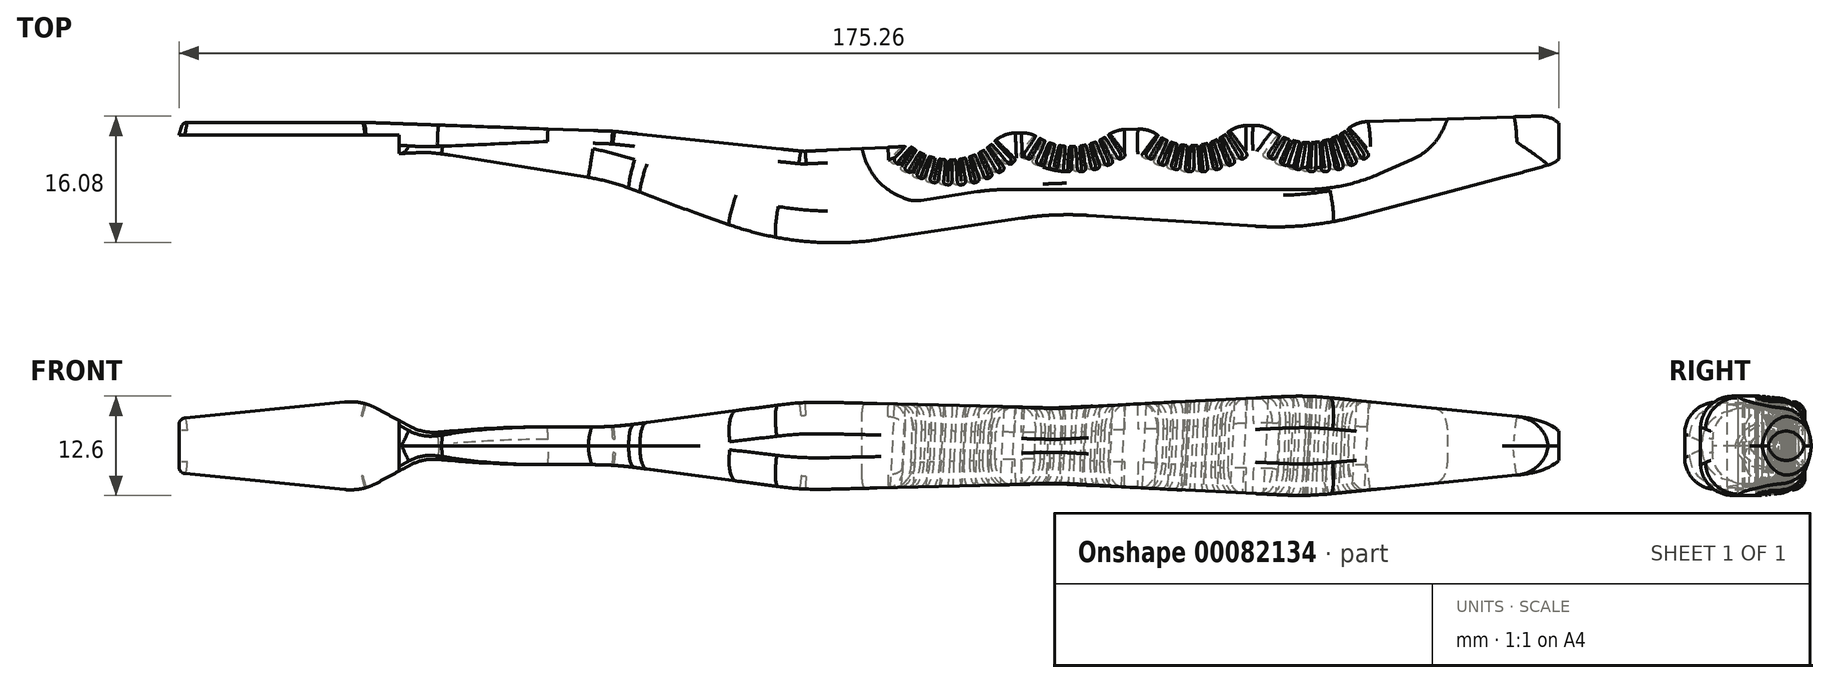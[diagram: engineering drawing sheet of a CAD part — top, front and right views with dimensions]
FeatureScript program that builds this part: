
annotation { "Feature Type Name" : "Feature", "Feature Type Description" : "" }
export const myFeature = defineFeature(function(context is Context, id is Id, definition is map)
    precondition{}
    {
        {
            var Q0;
            Q0=qCreatedBy(makeId("Front.planeOp"),FACE);
            var sketch = newSketch(context, id + "F0", { "sketchPlane" : qUnion([Q0])});
            skLineSegment(sketch, "E0", {"start": v(0, 0) * mm, "end": v(-220, 0) * mm, "construction": true});
            skLineSegment(sketch, "E1", {"start": v(-220, 0) * mm, "end": v(-220, 5) * mm});
            skLineSegment(sketch, "E2", {"start": v(-190, 0) * mm, "end": v(-190, 8) * mm, "construction": true});
            skLineSegment(sketch, "E3", {"start": v(-180, 0) * mm, "end": v(-180, 3) * mm, "construction": true});
            skLineSegment(sketch, "E4", {"start": v(-150, 0) * mm, "end": v(-150, 3) * mm, "construction": true});
            skLineSegment(sketch, "E5", {"start": v(-120, 0) * mm, "end": v(-120, 7) * mm, "construction": true});
            skLineSegment(sketch, "E6", {"start": v(-80, 0) * mm, "end": v(-80, 6) * mm, "construction": true});
            skLineSegment(sketch, "E7", {"start": v(-40, 0) * mm, "end": v(-40, 8) * mm, "construction": true});
            skLineSegment(sketch, "E8", {"start": v(0, 0) * mm, "end": v(0, 4) * mm});
            skLineSegment(sketch, "E9", {"start": v(0, 4) * mm, "end": v(-40, 8) * mm});
            skLineSegment(sketch, "E10", {"start": v(-40, 8) * mm, "end": v(-80, 6) * mm});
            skLineSegment(sketch, "E11", {"start": v(-80, 6) * mm, "end": v(-120, 7) * mm});
            skLineSegment(sketch, "E12", {"start": v(-120, 7) * mm, "end": v(-150, 3) * mm});
            skLineSegment(sketch, "E13", {"start": v(-150, 3) * mm, "end": v(-180, 3) * mm});
            skLineSegment(sketch, "E14", {"start": v(-180, 3) * mm, "end": v(-190, 8) * mm});
            skLineSegment(sketch, "E15", {"start": v(-190, 8) * mm, "end": v(-220, 5) * mm});
            skLineSegment(sketch, "E16.MirrorCS", {"start": v(0, 0) * mm, "end": v(0, -4) * mm});
            skLineSegment(sketch, "E17.MirrorCS", {"start": v(-220, 0) * mm, "end": v(-220, -5) * mm});
            skLineSegment(sketch, "E18.MirrorCS", {"start": v(-190, -8) * mm, "end": v(-220, -5) * mm});
            skLineSegment(sketch, "E19.MirrorCS", {"start": v(-180, -3) * mm, "end": v(-190, -8) * mm});
            skLineSegment(sketch, "E20.MirrorCS", {"start": v(-150, -3) * mm, "end": v(-180, -3) * mm});
            skLineSegment(sketch, "E21.MirrorCS", {"start": v(-120, -7) * mm, "end": v(-150, -3) * mm});
            skLineSegment(sketch, "E22.MirrorCS", {"start": v(-80, -6) * mm, "end": v(-120, -7) * mm});
            skLineSegment(sketch, "E23.MirrorCS", {"start": v(0, -4) * mm, "end": v(-40, -8) * mm});
            skLineSegment(sketch, "E24.MirrorCS", {"start": v(-40, -8) * mm, "end": v(-80, -6) * mm});
            skSolve(sketch);
        }
        {
            var Q0;
            Q0=makeQuery(id+"F0.imprint","IMPRINT",FACE,{"disambiguationData":[TD([[makeQuery(id+"F0.imprint","IMPRINT",EDGE,{"derivedFrom":sQuery(id+"F0.wireOp",EDGE,"E1")}),-1.0]])]});
            extrude(context, id + "F1", {"entities" : qUnion([Q0]), "depth" : 25 * mm});
        }
        {
            var Q0;
            Q0=makeQuery(id+"F1.opExtrude","SWEPT_FACE",FACE,{"disambiguationData":[OSD([sQuery(id+"F0.wireOp",EDGE,"E20.MirrorCS")])]});
            var sketch = newSketch(context, id + "F2", { "sketchPlane" : qUnion([Q0])});
            skLineSegment(sketch, "E25.0", {"start": v(-190, 0) * mm, "end": v(-220, 0) * mm, "construction": true});
            skLineSegment(sketch, "E25.4", {"start": v(-80, 0) * mm, "end": v(-120, 0) * mm, "construction": true});
            skLineSegment(sketch, "E25.5", {"start": v(-40, 0) * mm, "end": v(-80, 0) * mm, "construction": true});
            skLineSegment(sketch, "E25.6", {"start": v(0, 0) * mm, "end": v(-40, 0) * mm, "construction": true});
            skLineSegment(sketch, "E26", {"start": v(-220, 7.68) * mm, "end": v(-218.46, 2.68) * mm});
            skLineSegment(sketch, "E27", {"start": v(-218.46, 2.68) * mm, "end": v(-190, 2.68) * mm});
            skLineSegment(sketch, "E28", {"start": v(-119.9, 7.3) * mm, "end": v(-102.9, 6.47) * mm});
            skLineSegment(sketch, "E29", {"start": v(-119.9, 23.1) * mm, "end": v(-80, 17.11) * mm});
            skLineSegment(sketch, "E30", {"start": v(-80, 17.11) * mm, "end": v(-40, 19.71) * mm});
            skLineSegment(sketch, "E31", {"start": v(-40, 19.71) * mm, "end": v(0, 9.1) * mm});
            skLineSegment(sketch, "E32", {"start": v(0, 9.1) * mm, "end": v(0, 1.58) * mm});
            skArc(sketch, "E33", {"start": v(-88.51, 4.45) * mm, "mid": v(-95.27, 8.57) * mm, "end": v(-102.9, 6.47) * mm});
            skArc(sketch, "E34", {"start": v(-32.26, 2.63) * mm, "mid": v(-39.34, 5.9) * mm, "end": v(-46.62, 3.1) * mm});
            skLineSegment(sketch, "E35", {"start": v(-88.51, 4.45) * mm, "end": v(-83.73, 4.3) * mm});
            skLineSegment(sketch, "E36", {"start": v(-70.5, 3.87) * mm, "end": v(-64.85, 3.69) * mm});
            skArc(sketch, "E37.trimOffspring", {"start": v(-70.5, 3.87) * mm, "mid": v(-77.03, 6.54) * mm, "end": v(-83.73, 4.3) * mm});
            skLineSegment(sketch, "E38.trimOffspring", {"start": v(-51.47, 3.25) * mm, "end": v(-46.62, 3.1) * mm});
            skLineSegment(sketch, "E39.trimOffspring", {"start": v(-32.26, 2.63) * mm, "end": v(0, 1.58) * mm});
            skArc(sketch, "E40.trimOffspring", {"start": v(-51.47, 3.25) * mm, "mid": v(-58.07, 6.39) * mm, "end": v(-64.85, 3.69) * mm});
            skPoint(sketch, "E41.center.orphan", {"position": v(-77.66, -2.25) * mm});
            skPoint(sketch, "E42.center.orphan", {"position": v(-58.66, -3.17) * mm});
            skLineSegment(sketch, "E43.top", {"start": v(-229.41, 31.75) * mm, "end": v(15.55, 31.75) * mm});
            skLineSegment(sketch, "E43.left", {"start": v(-229.41, -17.07) * mm, "end": v(-229.41, 31.75) * mm});
            skLineSegment(sketch, "E43.right", {"start": v(15.55, -17.07) * mm, "end": v(15.55, 31.75) * mm});
            skLineSegment(sketch, "E44", {"start": v(-220, 7.68) * mm, "end": v(-180, 7.68) * mm});
            skLineSegment(sketch, "E45", {"start": v(-180, 7.68) * mm, "end": v(-150, 12.5) * mm});
            skLineSegment(sketch, "E46", {"start": v(-150, 12.5) * mm, "end": v(-119.9, 23.1) * mm});
            skLineSegment(sketch, "E47", {"start": v(-119.9, 7.3) * mm, "end": v(-150, 4.12) * mm});
            skLineSegment(sketch, "E48", {"start": v(-150, 4.12) * mm, "end": v(-190, 2.68) * mm});
            skLineSegment(sketch, "E49", {"start": v(15.55, -17.07) * mm, "end": v(-229.41, -17.07) * mm});
            skSolve(sketch);
        }
        {
            var Q0;
            Q0=makeQuery(id+"F2.imprint","IMPRINT",FACE,{"disambiguationData":[TD([[makeQuery(id+"F2.imprint","IMPRINT",EDGE,{"derivedFrom":sQuery(id+"F2.wireOp",EDGE,"E26")}),-1.0]])]});
            var Q1;
            {var subQ0=sQuery(id+"F2.wireOp",EDGE,"E45");Q1=makeQuery(id+"F2.imprint","IMPRINT",FACE,{"disambiguationData":[TD([[makeQuery(id+"F2.imprint","IMPRINT",EDGE,{"derivedFrom":subQ0}),1.0]])]});}
            var Q2;
            {var subQ1=sQuery(id+"F0.wireOp",EDGE,"E20.MirrorCS");var subQ6=makeQuery(id+"F1.opExtrude","CAP_EDGE",EDGE,{"disambiguationData":[OSD([subQ1])],"isStart":true});Q2=makeQuery(id+"F2.imprint","IMPRINT",FACE,{"disambiguationData":[TD([[makeQuery(id+"F2.imprint","IMPRINT",EDGE,{"derivedFrom":subQ6}),-1.0]])]});}
            extrude(context, id + "F3", {"entities" : qUnion([Q0, Q1, Q2]), "operationType" : NewBodyOperationType.REMOVE, "endBound" : BoundingType.SYMMETRIC, "oppositeDirection" : true, "depth" : 40 * mm});
        }
        {
            var Q0;
            Q0=makeQuery(id+"F3.boolean.opBoolean","COPY",EDGE,{"derivedFrom":makeQuery(id+"F3.opExtrude","SWEPT_EDGE",EDGE,{"disambiguationData":[OSD([sQuery(id+"F2.wireOp",EDGE,"E29"),sQuery(id+"F2.wireOp",EDGE,"E46")])]})});
            var Q1;
            Q1=makeQuery(id+"F3.boolean.opBoolean","COPY",EDGE,{"derivedFrom":makeQuery(id+"F3.opExtrude","SWEPT_EDGE",EDGE,{"disambiguationData":[OSD([sQuery(id+"F2.wireOp",EDGE,"E29"),sQuery(id+"F2.wireOp",EDGE,"E30")])]})});
            var Q2;
            Q2=makeQuery(id+"F3.boolean.opBoolean","COPY",EDGE,{"derivedFrom":makeQuery(id+"F3.opExtrude","SWEPT_EDGE",EDGE,{"disambiguationData":[OSD([sQuery(id+"F2.wireOp",EDGE,"E30"),sQuery(id+"F2.wireOp",EDGE,"E31")])]})});
            var Q3;
            Q3=makeQuery(id+"F3.boolean.opBoolean","COPY",EDGE,{"derivedFrom":makeQuery(id+"F3.opExtrude","SWEPT_EDGE",EDGE,{"disambiguationData":[OSD([sQuery(id+"F0.wireOp",EDGE,"E20.MirrorCS"),sQuery(id+"F0.wireOp",EDGE,"E21.MirrorCS"),sQuery(id+"F2.wireOp",EDGE,"E45"),sQuery(id+"F2.wireOp",EDGE,"E46")])]})});
            var Q4;
            Q4=makeQuery(id+"F3.boolean.opBoolean","COPY",EDGE,{"derivedFrom":makeQuery(id+"F3.opExtrude","SWEPT_EDGE",EDGE,{"disambiguationData":[OSD([sQuery(id+"F0.wireOp",EDGE,"E19.MirrorCS"),sQuery(id+"F0.wireOp",EDGE,"E20.MirrorCS"),sQuery(id+"F2.wireOp",EDGE,"E44"),sQuery(id+"F2.wireOp",EDGE,"E45")])]})});
            fillet(context, id + "F4", {"entities" : qUnion([Q0, Q1, Q2, Q3, Q4]), "radius" : 50 * mm, "tangentPropagation" : true, "allowEdgeOverflow" : false});
        }
        {
            var Q0;
            Q0=makeQuery(id+"F3.boolean.opBoolean","COPY",EDGE,{"derivedFrom":makeQuery(id+"F3.opExtrude","SWEPT_EDGE",EDGE,{"disambiguationData":[OSD([sQuery(id+"F2.wireOp",EDGE,"E27"),sQuery(id+"F2.wireOp",EDGE,"E48")])]})});
            var Q1;
            Q1=makeQuery(id+"F3.boolean.opBoolean","COPY",EDGE,{"derivedFrom":makeQuery(id+"F3.opExtrude","SWEPT_EDGE",EDGE,{"disambiguationData":[OSD([sQuery(id+"F0.wireOp",EDGE,"E20.MirrorCS"),sQuery(id+"F0.wireOp",EDGE,"E21.MirrorCS"),sQuery(id+"F2.wireOp",EDGE,"E47"),sQuery(id+"F2.wireOp",EDGE,"E48")])]})});
            var Q2;
            Q2=makeQuery(id+"F3.boolean.opBoolean","COPY",EDGE,{"derivedFrom":makeQuery(id+"F3.opExtrude","SWEPT_EDGE",EDGE,{"disambiguationData":[OSD([sQuery(id+"F2.wireOp",EDGE,"E28"),sQuery(id+"F2.wireOp",EDGE,"E47")])]})});
            fillet(context, id + "F5", {"entities" : qUnion([Q0, Q1, Q2]), "radius" : 5 * mm, "tangentPropagation" : true, "allowEdgeOverflow" : false});
        }
        {
            var Q0;
            Q0=makeQuery(id+"F1.opExtrude","SWEPT_EDGE",EDGE,{"disambiguationData":[OSD([sQuery(id+"F0.wireOp",EDGE,"E20.MirrorCS"),sQuery(id+"F0.wireOp",EDGE,"E21.MirrorCS")])]});
            var Q1;
            Q1=makeQuery(id+"F1.opExtrude","SWEPT_EDGE",EDGE,{"disambiguationData":[OSD([sQuery(id+"F0.wireOp",EDGE,"E21.MirrorCS"),sQuery(id+"F0.wireOp",EDGE,"E22.MirrorCS")])]});
            var Q2;
            Q2=makeQuery(id+"F1.opExtrude","SWEPT_EDGE",EDGE,{"disambiguationData":[OSD([sQuery(id+"F0.wireOp",EDGE,"E22.MirrorCS"),sQuery(id+"F0.wireOp",EDGE,"E24.MirrorCS")])]});
            var Q3;
            Q3=makeQuery(id+"F1.opExtrude","SWEPT_EDGE",EDGE,{"disambiguationData":[OSD([sQuery(id+"F0.wireOp",EDGE,"E23.MirrorCS"),sQuery(id+"F0.wireOp",EDGE,"E24.MirrorCS")])]});
            var Q4;
            Q4=makeQuery(id+"F1.opExtrude","SWEPT_EDGE",EDGE,{"disambiguationData":[OSD([sQuery(id+"F0.wireOp",EDGE,"E12"),sQuery(id+"F0.wireOp",EDGE,"E13")])]});
            var Q5;
            Q5=makeQuery(id+"F1.opExtrude","SWEPT_EDGE",EDGE,{"disambiguationData":[OSD([sQuery(id+"F0.wireOp",EDGE,"E11"),sQuery(id+"F0.wireOp",EDGE,"E12")])]});
            var Q6;
            Q6=makeQuery(id+"F1.opExtrude","SWEPT_EDGE",EDGE,{"disambiguationData":[OSD([sQuery(id+"F0.wireOp",EDGE,"E10"),sQuery(id+"F0.wireOp",EDGE,"E11")])]});
            var Q7;
            Q7=makeQuery(id+"F1.opExtrude","SWEPT_EDGE",EDGE,{"disambiguationData":[OSD([sQuery(id+"F0.wireOp",EDGE,"E9"),sQuery(id+"F0.wireOp",EDGE,"E10")])]});
            fillet(context, id + "F6", {"entities" : qUnion([Q0, Q1, Q2, Q3, Q4, Q5, Q6, Q7]), "radius" : 50 * mm, "tangentPropagation" : true, "allowEdgeOverflow" : false});
        }
        {
            var Q0;
            Q0=makeQuery(id+"F1.opExtrude","SWEPT_EDGE",EDGE,{"disambiguationData":[OSD([sQuery(id+"F0.wireOp",EDGE,"E18.MirrorCS"),sQuery(id+"F0.wireOp",EDGE,"E19.MirrorCS")])]});
            var Q1;
            Q1=makeQuery(id+"F1.opExtrude","SWEPT_EDGE",EDGE,{"disambiguationData":[OSD([sQuery(id+"F0.wireOp",EDGE,"E19.MirrorCS"),sQuery(id+"F0.wireOp",EDGE,"E20.MirrorCS")])]});
            var Q2;
            Q2=makeQuery(id+"F1.opExtrude","SWEPT_EDGE",EDGE,{"disambiguationData":[OSD([sQuery(id+"F0.wireOp",EDGE,"E13"),sQuery(id+"F0.wireOp",EDGE,"E14")])]});
            var Q3;
            Q3=makeQuery(id+"F1.opExtrude","SWEPT_EDGE",EDGE,{"disambiguationData":[OSD([sQuery(id+"F0.wireOp",EDGE,"E14"),sQuery(id+"F0.wireOp",EDGE,"E15")])]});
            fillet(context, id + "F7", {"entities" : qUnion([Q0, Q1, Q2, Q3]), "radius" : 10 * mm, "tangentPropagation" : true, "allowEdgeOverflow" : false});
        }
        {
            var Q0;
            Q0=makeQuery(id+"F6.opFillet","BLEND_EDGE",EDGE,{"blendedFrom":[makeQuery(id+"F1.opExtrude","SWEPT_EDGE",EDGE,{"disambiguationData":[OSD([sQuery(id+"F0.wireOp",EDGE,"E21.MirrorCS"),sQuery(id+"F0.wireOp",EDGE,"E22.MirrorCS")])]}),makeQuery(id+"F4.opFillet","BLEND_FACE",FACE,{"disambiguationData":[OSD([sQuery(id+"F2.wireOp",EDGE,"E29"),sQuery(id+"F2.wireOp",EDGE,"E46")])]})],"blendedInto":[makeQuery(id+"F4.opFillet","BLEND_FACE",FACE,{"disambiguationData":[OSD([sQuery(id+"F2.wireOp",EDGE,"E29"),sQuery(id+"F2.wireOp",EDGE,"E46")])]})]});
            var Q1;
            Q1=makeQuery(id+"F3.boolean.opBoolean","INTERSECT",EDGE,{"derivedFrom":[makeQuery(id+"F1.opExtrude","SWEPT_FACE",FACE,{"disambiguationData":[OSD([sQuery(id+"F0.wireOp",EDGE,"E11")])]}),makeQuery(id+"F3.opExtrude","SWEPT_FACE",FACE,{"disambiguationData":[OSD([sQuery(id+"F2.wireOp",EDGE,"E29")])]})]});
            fillet(context, id + "F8", {"entities" : qUnion([Q0, Q1]), "radius" : 5 * mm, "tangentPropagation" : true, "allowEdgeOverflow" : false});
        }
        {
            var Q0;
            Q0=makeQuery(id+"F3.boolean.opBoolean","INTERSECT",EDGE,{"derivedFrom":[makeQuery(id+"F1.opExtrude","SWEPT_FACE",FACE,{"disambiguationData":[OSD([sQuery(id+"F0.wireOp",EDGE,"E22.MirrorCS")])]}),makeQuery(id+"F3.opExtrude","SWEPT_FACE",FACE,{"disambiguationData":[OSD([sQuery(id+"F2.wireOp",EDGE,"E33")])]})]});
            var Q1;
            Q1=makeQuery(id+"F6.opFillet","BLEND_EDGE",EDGE,{"blendedFrom":[makeQuery(id+"F1.opExtrude","SWEPT_EDGE",EDGE,{"disambiguationData":[OSD([sQuery(id+"F0.wireOp",EDGE,"E22.MirrorCS"),sQuery(id+"F0.wireOp",EDGE,"E24.MirrorCS")])]}),makeQuery(id+"F3.boolean.opBoolean","COPY",FACE,{"derivedFrom":makeQuery(id+"F3.opExtrude","SWEPT_FACE",FACE,{"disambiguationData":[OSD([sQuery(id+"F2.wireOp",EDGE,"E37.trimOffspring")])]})})],"blendedInto":[makeQuery(id+"F3.boolean.opBoolean","COPY",FACE,{"derivedFrom":makeQuery(id+"F3.opExtrude","SWEPT_FACE",FACE,{"disambiguationData":[OSD([sQuery(id+"F2.wireOp",EDGE,"E37.trimOffspring")])]})})]});
            var Q2;
            Q2=makeQuery(id+"F3.boolean.opBoolean","INTERSECT",EDGE,{"derivedFrom":[makeQuery(id+"F1.opExtrude","SWEPT_FACE",FACE,{"disambiguationData":[OSD([sQuery(id+"F0.wireOp",EDGE,"E24.MirrorCS")])]}),makeQuery(id+"F3.opExtrude","SWEPT_FACE",FACE,{"disambiguationData":[OSD([sQuery(id+"F2.wireOp",EDGE,"E40.trimOffspring")])]})]});
            var Q3;
            Q3=makeQuery(id+"F6.opFillet","BLEND_EDGE",EDGE,{"blendedFrom":[makeQuery(id+"F1.opExtrude","SWEPT_EDGE",EDGE,{"disambiguationData":[OSD([sQuery(id+"F0.wireOp",EDGE,"E23.MirrorCS"),sQuery(id+"F0.wireOp",EDGE,"E24.MirrorCS")])]}),makeQuery(id+"F3.boolean.opBoolean","COPY",FACE,{"derivedFrom":makeQuery(id+"F3.opExtrude","SWEPT_FACE",FACE,{"disambiguationData":[OSD([sQuery(id+"F2.wireOp",EDGE,"E34")])]})})],"blendedInto":[makeQuery(id+"F3.boolean.opBoolean","COPY",FACE,{"derivedFrom":makeQuery(id+"F3.opExtrude","SWEPT_FACE",FACE,{"disambiguationData":[OSD([sQuery(id+"F2.wireOp",EDGE,"E34")])]})})]});
            var Q4;
            Q4=makeQuery(id+"F3.boolean.opBoolean","INTERSECT",EDGE,{"derivedFrom":[makeQuery(id+"F1.opExtrude","SWEPT_FACE",FACE,{"disambiguationData":[OSD([sQuery(id+"F0.wireOp",EDGE,"E22.MirrorCS")])]}),makeQuery(id+"F3.opExtrude","SWEPT_FACE",FACE,{"disambiguationData":[OSD([sQuery(id+"F2.wireOp",EDGE,"E35")])]})]});
            var Q5;
            Q5=makeQuery(id+"F3.boolean.opBoolean","INTERSECT",EDGE,{"derivedFrom":[makeQuery(id+"F1.opExtrude","SWEPT_FACE",FACE,{"disambiguationData":[OSD([sQuery(id+"F0.wireOp",EDGE,"E24.MirrorCS")])]}),makeQuery(id+"F3.opExtrude","SWEPT_FACE",FACE,{"disambiguationData":[OSD([sQuery(id+"F2.wireOp",EDGE,"E36")])]})]});
            var Q6;
            Q6=makeQuery(id+"F3.boolean.opBoolean","INTERSECT",EDGE,{"derivedFrom":[makeQuery(id+"F1.opExtrude","SWEPT_FACE",FACE,{"disambiguationData":[OSD([sQuery(id+"F0.wireOp",EDGE,"E24.MirrorCS")])]}),makeQuery(id+"F3.opExtrude","SWEPT_FACE",FACE,{"disambiguationData":[OSD([sQuery(id+"F2.wireOp",EDGE,"E38.trimOffspring")])]})]});
            var Q7;
            Q7=makeQuery(id+"F3.boolean.opBoolean","INTERSECT",EDGE,{"derivedFrom":[makeQuery(id+"F1.opExtrude","SWEPT_FACE",FACE,{"disambiguationData":[OSD([sQuery(id+"F0.wireOp",EDGE,"E23.MirrorCS")])]}),makeQuery(id+"F3.opExtrude","SWEPT_FACE",FACE,{"disambiguationData":[OSD([sQuery(id+"F2.wireOp",EDGE,"E39.trimOffspring")])]})]});
            var Q8;
            Q8=makeQuery(id+"F3.boolean.opBoolean","INTERSECT",EDGE,{"derivedFrom":[makeQuery(id+"F1.opExtrude","SWEPT_FACE",FACE,{"disambiguationData":[OSD([sQuery(id+"F0.wireOp",EDGE,"E11")])]}),makeQuery(id+"F3.opExtrude","SWEPT_FACE",FACE,{"disambiguationData":[OSD([sQuery(id+"F2.wireOp",EDGE,"E33")])]})]});
            var Q9;
            Q9=makeQuery(id+"F3.boolean.opBoolean","INTERSECT",EDGE,{"derivedFrom":[makeQuery(id+"F1.opExtrude","SWEPT_FACE",FACE,{"disambiguationData":[OSD([sQuery(id+"F0.wireOp",EDGE,"E11")])]}),makeQuery(id+"F3.opExtrude","SWEPT_FACE",FACE,{"disambiguationData":[OSD([sQuery(id+"F2.wireOp",EDGE,"E35")])]})]});
            var Q10;
            Q10=makeQuery(id+"F3.boolean.opBoolean","INTERSECT",EDGE,{"derivedFrom":[makeQuery(id+"F1.opExtrude","SWEPT_FACE",FACE,{"disambiguationData":[OSD([sQuery(id+"F0.wireOp",EDGE,"E10")])]}),makeQuery(id+"F3.opExtrude","SWEPT_FACE",FACE,{"disambiguationData":[OSD([sQuery(id+"F2.wireOp",EDGE,"E37.trimOffspring")])]})]});
            var Q11;
            Q11=makeQuery(id+"F3.boolean.opBoolean","INTERSECT",EDGE,{"derivedFrom":[makeQuery(id+"F1.opExtrude","SWEPT_FACE",FACE,{"disambiguationData":[OSD([sQuery(id+"F0.wireOp",EDGE,"E10")])]}),makeQuery(id+"F3.opExtrude","SWEPT_FACE",FACE,{"disambiguationData":[OSD([sQuery(id+"F2.wireOp",EDGE,"E36")])]})]});
            var Q12;
            Q12=makeQuery(id+"F3.boolean.opBoolean","INTERSECT",EDGE,{"derivedFrom":[makeQuery(id+"F1.opExtrude","SWEPT_FACE",FACE,{"disambiguationData":[OSD([sQuery(id+"F0.wireOp",EDGE,"E10")])]}),makeQuery(id+"F3.opExtrude","SWEPT_FACE",FACE,{"disambiguationData":[OSD([sQuery(id+"F2.wireOp",EDGE,"E40.trimOffspring")])]})]});
            var Q13;
            Q13=makeQuery(id+"F3.boolean.opBoolean","INTERSECT",EDGE,{"derivedFrom":[makeQuery(id+"F1.opExtrude","SWEPT_FACE",FACE,{"disambiguationData":[OSD([sQuery(id+"F0.wireOp",EDGE,"E10")])]}),makeQuery(id+"F3.opExtrude","SWEPT_FACE",FACE,{"disambiguationData":[OSD([sQuery(id+"F2.wireOp",EDGE,"E38.trimOffspring")])]})]});
            var Q14;
            Q14=makeQuery(id+"F6.opFillet","BLEND_EDGE",EDGE,{"blendedFrom":[makeQuery(id+"F1.opExtrude","SWEPT_EDGE",EDGE,{"disambiguationData":[OSD([sQuery(id+"F0.wireOp",EDGE,"E9"),sQuery(id+"F0.wireOp",EDGE,"E10")])]}),makeQuery(id+"F3.boolean.opBoolean","COPY",FACE,{"derivedFrom":makeQuery(id+"F3.opExtrude","SWEPT_FACE",FACE,{"disambiguationData":[OSD([sQuery(id+"F2.wireOp",EDGE,"E34")])]})})],"blendedInto":[makeQuery(id+"F3.boolean.opBoolean","COPY",FACE,{"derivedFrom":makeQuery(id+"F3.opExtrude","SWEPT_FACE",FACE,{"disambiguationData":[OSD([sQuery(id+"F2.wireOp",EDGE,"E34")])]})})]});
            var Q15;
            Q15=makeQuery(id+"F3.boolean.opBoolean","INTERSECT",EDGE,{"derivedFrom":[makeQuery(id+"F1.opExtrude","SWEPT_FACE",FACE,{"disambiguationData":[OSD([sQuery(id+"F0.wireOp",EDGE,"E9")])]}),makeQuery(id+"F3.opExtrude","SWEPT_FACE",FACE,{"disambiguationData":[OSD([sQuery(id+"F2.wireOp",EDGE,"E39.trimOffspring")])]})]});
            fillet(context, id + "F9", {"entities" : qUnion([Q0, Q1, Q2, Q3, Q4, Q5, Q6, Q7, Q8, Q9, Q10, Q11, Q12, Q13, Q14, Q15]), "radius" : 4 * mm, "tangentPropagation" : true, "allowEdgeOverflow" : false});
        }
        {
            var Q0;
            Q0=makeQuery(id+"F3.boolean.opBoolean","INTERSECT",EDGE,{"derivedFrom":[makeQuery(id+"F1.opExtrude","SWEPT_FACE",FACE,{"disambiguationData":[OSD([sQuery(id+"F0.wireOp",EDGE,"E22.MirrorCS")])]}),makeQuery(id+"F3.opExtrude","SWEPT_FACE",FACE,{"disambiguationData":[OSD([sQuery(id+"F2.wireOp",EDGE,"E28")])]})]});
            fillet(context, id + "F10", {"entities" : qUnion([Q0]), "radius" : 2 * mm, "tangentPropagation" : true, "allowEdgeOverflow" : false});
        }
        {
            var Q0;
            Q0=makeQuery(id+"F3.boolean.opBoolean","COPY",EDGE,{"derivedFrom":makeQuery(id+"F3.opExtrude","SWEPT_EDGE",EDGE,{"disambiguationData":[OSD([sQuery(id+"F2.wireOp",EDGE,"E33"),sQuery(id+"F2.wireOp",EDGE,"E35")])]})});
            var Q1;
            Q1=makeQuery(id+"F3.boolean.opBoolean","COPY",EDGE,{"derivedFrom":makeQuery(id+"F3.opExtrude","SWEPT_EDGE",EDGE,{"disambiguationData":[OSD([sQuery(id+"F2.wireOp",EDGE,"E35"),sQuery(id+"F2.wireOp",EDGE,"E37.trimOffspring")])]})});
            var Q2;
            Q2=makeQuery(id+"F3.boolean.opBoolean","COPY",EDGE,{"derivedFrom":makeQuery(id+"F3.opExtrude","SWEPT_EDGE",EDGE,{"disambiguationData":[OSD([sQuery(id+"F2.wireOp",EDGE,"E36"),sQuery(id+"F2.wireOp",EDGE,"E37.trimOffspring")])]})});
            var Q3;
            Q3=makeQuery(id+"F3.boolean.opBoolean","COPY",EDGE,{"derivedFrom":makeQuery(id+"F3.opExtrude","SWEPT_EDGE",EDGE,{"disambiguationData":[OSD([sQuery(id+"F2.wireOp",EDGE,"E36"),sQuery(id+"F2.wireOp",EDGE,"E40.trimOffspring")])]})});
            var Q4;
            Q4=makeQuery(id+"F3.boolean.opBoolean","COPY",EDGE,{"derivedFrom":makeQuery(id+"F3.opExtrude","SWEPT_EDGE",EDGE,{"disambiguationData":[OSD([sQuery(id+"F2.wireOp",EDGE,"E38.trimOffspring"),sQuery(id+"F2.wireOp",EDGE,"E40.trimOffspring")])]})});
            var Q5;
            Q5=makeQuery(id+"F3.boolean.opBoolean","COPY",EDGE,{"derivedFrom":makeQuery(id+"F3.opExtrude","SWEPT_EDGE",EDGE,{"disambiguationData":[OSD([sQuery(id+"F2.wireOp",EDGE,"E34"),sQuery(id+"F2.wireOp",EDGE,"E38.trimOffspring")])]})});
            var Q6;
            Q6=makeQuery(id+"F3.boolean.opBoolean","COPY",EDGE,{"derivedFrom":makeQuery(id+"F3.opExtrude","SWEPT_EDGE",EDGE,{"disambiguationData":[OSD([sQuery(id+"F2.wireOp",EDGE,"E34"),sQuery(id+"F2.wireOp",EDGE,"E39.trimOffspring")])]})});
            fillet(context, id + "F11", {"entities" : qUnion([Q0, Q1, Q2, Q3, Q4, Q5, Q6]), "radius" : 5 * mm, "tangentPropagation" : true, "allowEdgeOverflow" : false});
        }
        {
            var Q0;
            Q0=makeQuery(id+"F8.opFillet","BLEND_EDGE",EDGE,{"blendedFrom":[makeQuery(id+"F3.boolean.opBoolean","INTERSECT",EDGE,{"derivedFrom":[makeQuery(id+"F1.opExtrude","SWEPT_FACE",FACE,{"disambiguationData":[OSD([sQuery(id+"F0.wireOp",EDGE,"E18.MirrorCS")])]}),makeQuery(id+"F3.opExtrude","SWEPT_FACE",FACE,{"disambiguationData":[OSD([sQuery(id+"F2.wireOp",EDGE,"E44")])]})]}),makeQuery(id+"F3.boolean.opBoolean","COPY",FACE,{"derivedFrom":makeQuery(id+"F3.opExtrude","SWEPT_FACE",FACE,{"disambiguationData":[OSD([sQuery(id+"F2.wireOp",EDGE,"E26")])]})})],"blendedInto":[makeQuery(id+"F3.boolean.opBoolean","COPY",FACE,{"derivedFrom":makeQuery(id+"F3.opExtrude","SWEPT_FACE",FACE,{"disambiguationData":[OSD([sQuery(id+"F2.wireOp",EDGE,"E26")])]})})]});
            fillet(context, id + "F12", {"entities" : qUnion([Q0]), "radius" : 1 * mm, "tangentPropagation" : true, "allowEdgeOverflow" : false});
        }
        {
            var Q0;
            Q0=qCreatedBy(makeId("Top.planeOp"),FACE);
            var sketch = newSketch(context, id + "F13", { "sketchPlane" : qUnion([Q0])});
            skLineSegment(sketch, "E50", {"start": v(-111.36, -3.91) * mm, "end": v(-110.38, -7.71) * mm});
            skLineSegment(sketch, "E51", {"start": v(-104.93, -14.29) * mm, "end": v(-104.14, -14.66) * mm});
            skLineSegment(sketch, "E52", {"start": v(-101.27, -15.07) * mm, "end": v(-92.35, -13.7) * mm});
            skLineSegment(sketch, "E53", {"start": v(-87.82, -13.36) * mm, "end": v(-74.2, -13.36) * mm});
            skLineSegment(sketch, "E54", {"start": v(-74.2, -13.36) * mm, "end": v(-53.16, -13.36) * mm});
            skLineSegment(sketch, "E55", {"start": v(-53.16, -13.36) * mm, "end": v(-40.43, -13.36) * mm});
            skLineSegment(sketch, "E56", {"start": v(-28.35, -10.83) * mm, "end": v(-23.32, -8.61) * mm});
            skLineSegment(sketch, "E57", {"start": v(-18.04, -3.12) * mm, "end": v(-16.8, 0) * mm});
            skPoint(sketch, "E58.visualSharp", {"position": v(-109.21, -12.29) * mm});
            skArc(sketch, "E58.filletArc", {"start": v(-110.38, -7.71) * mm, "mid": v(-108.4, -11.61) * mm, "end": v(-104.93, -14.29) * mm});
            skPoint(sketch, "E59.visualSharp", {"position": v(-102.77, -15.3) * mm});
            skArc(sketch, "E59.filletArc", {"start": v(-104.14, -14.66) * mm, "mid": v(-102.74, -15.07) * mm, "end": v(-101.27, -15.07) * mm});
            skPoint(sketch, "E60.visualSharp", {"position": v(-19.55, -6.95) * mm});
            skArc(sketch, "E60.filletArc", {"start": v(-23.32, -8.61) * mm, "mid": v(-20.13, -6.39) * mm, "end": v(-18.04, -3.12) * mm});
            skPoint(sketch, "E61.visualSharp", {"position": v(-34.12, -13.36) * mm});
            skArc(sketch, "E61.filletArc", {"start": v(-40.43, -13.36) * mm, "mid": v(-34.26, -12.72) * mm, "end": v(-28.35, -10.83) * mm});
            skPoint(sketch, "E62.visualSharp", {"position": v(-90.1, -13.36) * mm});
            skArc(sketch, "E62.filletArc", {"start": v(-87.82, -13.36) * mm, "mid": v(-90.1, -13.45) * mm, "end": v(-92.35, -13.7) * mm});
            skLineSegment(sketch, "E63", {"start": v(-111.36, -3.91) * mm, "end": v(-16.8, 0) * mm});
            skSolve(sketch);
        }
        {
            var Q0;
            Q0=makeQuery(id+"F13.imprint","IMPRINT",FACE,{"disambiguationData":[TD([[makeQuery(id+"F13.imprint","IMPRINT",EDGE,{"derivedFrom":sQuery(id+"F13.wireOp",EDGE,"E50")}),1.0]])]});
            extrude(context, id + "F14", {"entities" : qUnion([Q0]), "endBound" : BoundingType.SYMMETRIC, "depth" : 40 * mm});
        }
        {
            var Q0;
            Q0=makeQuery(id+"F14.opExtrude","SWEPT_BODY",BODY,{"disambiguationData":[OSD([sQuery(id+"F13.wireOp",EDGE,"E50"),sQuery(id+"F13.wireOp",EDGE,"E51"),sQuery(id+"F13.wireOp",EDGE,"E52"),sQuery(id+"F13.wireOp",EDGE,"E53"),sQuery(id+"F13.wireOp",EDGE,"E54"),sQuery(id+"F13.wireOp",EDGE,"E55"),sQuery(id+"F13.wireOp",EDGE,"E56"),sQuery(id+"F13.wireOp",EDGE,"E57"),sQuery(id+"F13.wireOp",EDGE,"E58.filletArc"),sQuery(id+"F13.wireOp",EDGE,"E59.filletArc"),sQuery(id+"F13.wireOp",EDGE,"E60.filletArc"),sQuery(id+"F13.wireOp",EDGE,"E61.filletArc"),sQuery(id+"F13.wireOp",EDGE,"E62.filletArc"),sQuery(id+"F13.wireOp",EDGE,"E63")])]});
            var Q1;
            Q1=makeQuery(id+"F1.opExtrude","SWEPT_BODY",BODY,{"disambiguationData":[OSD([sQuery(id+"F0.wireOp",EDGE,"E1"),sQuery(id+"F0.wireOp",EDGE,"E8"),sQuery(id+"F0.wireOp",EDGE,"E9"),sQuery(id+"F0.wireOp",EDGE,"E10"),sQuery(id+"F0.wireOp",EDGE,"E11"),sQuery(id+"F0.wireOp",EDGE,"E12"),sQuery(id+"F0.wireOp",EDGE,"E13"),sQuery(id+"F0.wireOp",EDGE,"E14"),sQuery(id+"F0.wireOp",EDGE,"E15"),sQuery(id+"F0.wireOp",EDGE,"E16.MirrorCS"),sQuery(id+"F0.wireOp",EDGE,"E17.MirrorCS"),sQuery(id+"F0.wireOp",EDGE,"E18.MirrorCS"),sQuery(id+"F0.wireOp",EDGE,"E19.MirrorCS"),sQuery(id+"F0.wireOp",EDGE,"E20.MirrorCS"),sQuery(id+"F0.wireOp",EDGE,"E21.MirrorCS"),sQuery(id+"F0.wireOp",EDGE,"E22.MirrorCS"),sQuery(id+"F0.wireOp",EDGE,"E23.MirrorCS"),sQuery(id+"F0.wireOp",EDGE,"E24.MirrorCS")])]});
            booleanBodies(context, id + "F15", {"operationType" : BooleanOperationType.INTERSECTION, "tools" : qUnion([Q0, Q1]), "keepTools" : true});
        }
        {
            var Q0;
            Q0=makeQuery(id+"F15.opBoolean","INTERSECT",BODY,{"derivedFrom":[makeQuery(id+"F1.opExtrude","SWEPT_BODY",BODY,{"disambiguationData":[OSD([sQuery(id+"F0.wireOp",EDGE,"E1"),sQuery(id+"F0.wireOp",EDGE,"E8"),sQuery(id+"F0.wireOp",EDGE,"E9"),sQuery(id+"F0.wireOp",EDGE,"E10"),sQuery(id+"F0.wireOp",EDGE,"E11"),sQuery(id+"F0.wireOp",EDGE,"E12"),sQuery(id+"F0.wireOp",EDGE,"E13"),sQuery(id+"F0.wireOp",EDGE,"E14"),sQuery(id+"F0.wireOp",EDGE,"E15"),sQuery(id+"F0.wireOp",EDGE,"E16.MirrorCS"),sQuery(id+"F0.wireOp",EDGE,"E17.MirrorCS"),sQuery(id+"F0.wireOp",EDGE,"E18.MirrorCS"),sQuery(id+"F0.wireOp",EDGE,"E19.MirrorCS"),sQuery(id+"F0.wireOp",EDGE,"E20.MirrorCS"),sQuery(id+"F0.wireOp",EDGE,"E21.MirrorCS"),sQuery(id+"F0.wireOp",EDGE,"E22.MirrorCS"),sQuery(id+"F0.wireOp",EDGE,"E23.MirrorCS"),sQuery(id+"F0.wireOp",EDGE,"E24.MirrorCS")])]}),makeQuery(id+"F14.opExtrude","SWEPT_BODY",BODY,{"disambiguationData":[OSD([sQuery(id+"F13.wireOp",EDGE,"E50"),sQuery(id+"F13.wireOp",EDGE,"E51"),sQuery(id+"F13.wireOp",EDGE,"E52"),sQuery(id+"F13.wireOp",EDGE,"E53"),sQuery(id+"F13.wireOp",EDGE,"E54"),sQuery(id+"F13.wireOp",EDGE,"E55"),sQuery(id+"F13.wireOp",EDGE,"E56"),sQuery(id+"F13.wireOp",EDGE,"E57"),sQuery(id+"F13.wireOp",EDGE,"E58.filletArc"),sQuery(id+"F13.wireOp",EDGE,"E59.filletArc"),sQuery(id+"F13.wireOp",EDGE,"E60.filletArc"),sQuery(id+"F13.wireOp",EDGE,"E61.filletArc"),sQuery(id+"F13.wireOp",EDGE,"E62.filletArc"),sQuery(id+"F13.wireOp",EDGE,"E63")])]})]});
            var Q1;
            Q1=makeQuery(id+"F1.opExtrude","SWEPT_BODY",BODY,{"disambiguationData":[OSD([sQuery(id+"F0.wireOp",EDGE,"E1"),sQuery(id+"F0.wireOp",EDGE,"E8"),sQuery(id+"F0.wireOp",EDGE,"E9"),sQuery(id+"F0.wireOp",EDGE,"E10"),sQuery(id+"F0.wireOp",EDGE,"E11"),sQuery(id+"F0.wireOp",EDGE,"E12"),sQuery(id+"F0.wireOp",EDGE,"E13"),sQuery(id+"F0.wireOp",EDGE,"E14"),sQuery(id+"F0.wireOp",EDGE,"E15"),sQuery(id+"F0.wireOp",EDGE,"E16.MirrorCS"),sQuery(id+"F0.wireOp",EDGE,"E17.MirrorCS"),sQuery(id+"F0.wireOp",EDGE,"E18.MirrorCS"),sQuery(id+"F0.wireOp",EDGE,"E19.MirrorCS"),sQuery(id+"F0.wireOp",EDGE,"E20.MirrorCS"),sQuery(id+"F0.wireOp",EDGE,"E21.MirrorCS"),sQuery(id+"F0.wireOp",EDGE,"E22.MirrorCS"),sQuery(id+"F0.wireOp",EDGE,"E23.MirrorCS"),sQuery(id+"F0.wireOp",EDGE,"E24.MirrorCS")])]});
            booleanBodies(context, id + "F16", {"operationType" : BooleanOperationType.SUBTRACTION, "tools" : qUnion([Q0]), "targets" : qUnion([Q1]), "keepTools" : true});
        }
        {
            var Q0;
            Q0=makeQuery(id+"F15.opBoolean","COPY",FACE,{"derivedFrom":makeQuery(id+"F1.opExtrude","SWEPT_FACE",FACE,{"disambiguationData":[OSD([sQuery(id+"F0.wireOp",EDGE,"E24.MirrorCS")])]})});
            var sketch = newSketch(context, id + "F17", { "sketchPlane" : qUnion([Q0])});
            skEllipticalArc(sketch, "E64.0", {});
            skLineSegment(sketch, "E65", {"start": v(-96.12, -1.34) * mm, "end": v(-105.56, 8.28) * mm});
            skLineSegment(sketch, "E66", {"start": v(-96.12, -1.34) * mm, "end": v(-104.6, 9.15) * mm});
            skLineSegment(sketch, "E67.anchor1", {"start": v(-96.12, -1.34) * mm, "end": v(-96.12, -1.34) * mm});
            skLineSegment(sketch, "E67.anchor2", {"start": v(-96.12, -1.34) * mm, "end": v(-96.12, -1.34) * mm});
            skPoint(sketch, "E68.visualSharp", {"position": v(-104.91, 9.54) * mm});
            skArc(sketch, "E68.filletArc", {"start": v(-104.6, 9.15) * mm, "mid": v(-104.94, 9.33) * mm, "end": v(-105.31, 9.2) * mm});
            skPoint(sketch, "E69.visualSharp", {"position": v(-105.91, 8.65) * mm});
            skArc(sketch, "E69.filletArc", {"start": v(-105.54, 9) * mm, "mid": v(-105.7, 8.65) * mm, "end": v(-105.56, 8.28) * mm});
            skLineSegment(sketch, "E70.1.0", {"start": v(-96.12, -1.34) * mm, "end": v(-102.8, 10.37) * mm});
            skLineSegment(sketch, "E70.1.1", {"start": v(-96.12, -1.34) * mm, "end": v(-103.89, 9.68) * mm});
            skArc(sketch, "E70.1.2", {"start": v(-102.8, 10.37) * mm, "mid": v(-103.1, 10.6) * mm, "end": v(-103.5, 10.55) * mm});
            skEllipticalArc(sketch, "E70.1.3", {});
            skArc(sketch, "E70.1.4", {"start": v(-103.75, 10.38) * mm, "mid": v(-103.97, 10.06) * mm, "end": v(-103.89, 9.68) * mm});
            skLineSegment(sketch, "E70.2.0", {"start": v(-96.12, -1.34) * mm, "end": v(-100.83, 11.3) * mm});
            skLineSegment(sketch, "E70.2.1", {"start": v(-96.12, -1.34) * mm, "end": v(-102.01, 10.78) * mm});
            skArc(sketch, "E70.2.2", {"start": v(-100.83, 11.3) * mm, "mid": v(-101.1, 11.58) * mm, "end": v(-101.49, 11.58) * mm});
            skEllipticalArc(sketch, "E70.2.3", {});
            skArc(sketch, "E70.2.4", {"start": v(-101.77, 11.46) * mm, "mid": v(-102.03, 11.17) * mm, "end": v(-102.01, 10.78) * mm});
            skLineSegment(sketch, "E70.3.0", {"start": v(-96.12, -1.34) * mm, "end": v(-98.73, 11.88) * mm});
            skLineSegment(sketch, "E70.3.1", {"start": v(-96.12, -1.34) * mm, "end": v(-99.99, 11.57) * mm});
            skArc(sketch, "E70.3.2", {"start": v(-98.73, 11.88) * mm, "mid": v(-98.95, 12.2) * mm, "end": v(-99.34, 12.27) * mm});
            skEllipticalArc(sketch, "E70.3.3", {});
            skArc(sketch, "E70.3.4", {"start": v(-99.64, 12.2) * mm, "mid": v(-99.94, 11.96) * mm, "end": v(-99.99, 11.57) * mm});
            skLineSegment(sketch, "E70.4.0", {"start": v(-96.12, -1.34) * mm, "end": v(-96.57, 12.13) * mm});
            skLineSegment(sketch, "E70.4.1", {"start": v(-96.12, -1.34) * mm, "end": v(-97.86, 12.03) * mm});
            skArc(sketch, "E70.4.2", {"start": v(-96.57, 12.13) * mm, "mid": v(-96.74, 12.49) * mm, "end": v(-97.1, 12.61) * mm});
            skEllipticalArc(sketch, "E70.4.3", {});
            skArc(sketch, "E70.4.4", {"start": v(-97.41, 12.59) * mm, "mid": v(-97.76, 12.4) * mm, "end": v(-97.86, 12.03) * mm});
            skLineSegment(sketch, "E70.5.0", {"start": v(-96.12, -1.34) * mm, "end": v(-94.4, 12.03) * mm});
            skLineSegment(sketch, "E70.5.1", {"start": v(-96.12, -1.34) * mm, "end": v(-95.69, 12.13) * mm});
            skArc(sketch, "E70.5.2", {"start": v(-94.4, 12.03) * mm, "mid": v(-94.5, 12.4) * mm, "end": v(-94.85, 12.6) * mm});
            skEllipticalArc(sketch, "E70.5.3", {});
            skArc(sketch, "E70.5.4", {"start": v(-95.16, 12.61) * mm, "mid": v(-95.52, 12.49) * mm, "end": v(-95.69, 12.13) * mm});
            skLineSegment(sketch, "E70.6.0", {"start": v(-96.12, -1.34) * mm, "end": v(-92.27, 11.58) * mm});
            skLineSegment(sketch, "E70.6.1", {"start": v(-96.12, -1.34) * mm, "end": v(-93.53, 11.89) * mm});
            skArc(sketch, "E70.6.2", {"start": v(-92.27, 11.58) * mm, "mid": v(-92.32, 11.97) * mm, "end": v(-92.63, 12.2) * mm});
            skEllipticalArc(sketch, "E70.6.3", {});
            skArc(sketch, "E70.6.4", {"start": v(-92.92, 12.28) * mm, "mid": v(-93.3, 12.21) * mm, "end": v(-93.53, 11.89) * mm});
            skLineSegment(sketch, "E70.7.0", {"start": v(-96.12, -1.34) * mm, "end": v(-90.24, 10.8) * mm});
            skLineSegment(sketch, "E70.7.1", {"start": v(-96.12, -1.34) * mm, "end": v(-91.43, 11.3) * mm});
            skArc(sketch, "E70.7.2", {"start": v(-90.24, 10.8) * mm, "mid": v(-90.23, 11.18) * mm, "end": v(-90.5, 11.47) * mm});
            skEllipticalArc(sketch, "E70.7.3", {});
            skArc(sketch, "E70.7.4", {"start": v(-90.78, 11.59) * mm, "mid": v(-91.17, 11.58) * mm, "end": v(-91.43, 11.3) * mm});
            skLineSegment(sketch, "E70.8.0", {"start": v(-96.12, -1.34) * mm, "end": v(-88.37, 9.69) * mm});
            skLineSegment(sketch, "E70.8.1", {"start": v(-96.12, -1.34) * mm, "end": v(-89.46, 10.38) * mm});
            skArc(sketch, "E70.8.2", {"start": v(-88.37, 9.69) * mm, "mid": v(-88.29, 10.07) * mm, "end": v(-88.5, 10.4) * mm});
            skEllipticalArc(sketch, "E70.8.3", {});
            skArc(sketch, "E70.8.4", {"start": v(-88.77, 10.56) * mm, "mid": v(-89.15, 10.62) * mm, "end": v(-89.46, 10.38) * mm});
            skLineSegment(sketch, "E70.9.0", {"start": v(-96.12, -1.34) * mm, "end": v(-86.7, 8.3) * mm});
            skLineSegment(sketch, "E70.9.1", {"start": v(-96.12, -1.34) * mm, "end": v(-87.67, 9.15) * mm});
            skArc(sketch, "E70.9.2", {"start": v(-86.7, 8.3) * mm, "mid": v(-86.56, 8.66) * mm, "end": v(-86.72, 9.02) * mm});
            skEllipticalArc(sketch, "E70.9.3", {});
            skArc(sketch, "E70.9.4", {"start": v(-86.95, 9.22) * mm, "mid": v(-87.32, 9.34) * mm, "end": v(-87.67, 9.15) * mm});
            skPoint(sketch, "E71.center", {"position": v(-77.09, -3.64) * mm});
            skLineSegment(sketch, "E71.anchor1", {"start": v(-77.09, -3.64) * mm, "end": v(-77.09, -3.64) * mm});
            skLineSegment(sketch, "E71.anchor2", {"start": v(-77.09, -3.64) * mm, "end": v(-64.03, -3.64) * mm, "construction": true});
            skPoint(sketch, "E72.visualSharp", {"position": v(-86.02, 7.41) * mm});
            skPoint(sketch, "E73.visualSharp", {"position": v(-87.02, 6.48) * mm});
            skLineSegment(sketch, "E74.1.0", {"start": v(-77.09, -3.64) * mm, "end": v(-83.87, 8.25) * mm});
            skLineSegment(sketch, "E74.1.1", {"start": v(-77.09, -3.64) * mm, "end": v(-84.98, 7.54) * mm});
            skArc(sketch, "E74.1.2", {"start": v(-83.87, 8.25) * mm, "mid": v(-84.19, 8.5) * mm, "end": v(-84.58, 8.42) * mm});
            skEllipticalArc(sketch, "E74.1.3", {});
            skArc(sketch, "E74.1.4", {"start": v(-84.85, 8.24) * mm, "mid": v(-85.06, 7.92) * mm, "end": v(-84.98, 7.54) * mm});
            skLineSegment(sketch, "E74.2.0", {"start": v(-77.09, -3.64) * mm, "end": v(-81.87, 9.19) * mm});
            skLineSegment(sketch, "E74.2.1", {"start": v(-77.09, -3.64) * mm, "end": v(-83.07, 8.67) * mm});
            skArc(sketch, "E74.2.2", {"start": v(-81.87, 9.19) * mm, "mid": v(-82.14, 9.47) * mm, "end": v(-82.54, 9.47) * mm});
            skEllipticalArc(sketch, "E74.2.3", {});
            skArc(sketch, "E74.2.4", {"start": v(-82.84, 9.34) * mm, "mid": v(-83.1, 9.05) * mm, "end": v(-83.07, 8.67) * mm});
            skLineSegment(sketch, "E74.3.0", {"start": v(-77.09, -3.64) * mm, "end": v(-79.74, 9.79) * mm});
            skLineSegment(sketch, "E74.3.1", {"start": v(-77.09, -3.64) * mm, "end": v(-81.02, 9.47) * mm});
            skArc(sketch, "E74.3.2", {"start": v(-79.74, 9.79) * mm, "mid": v(-79.97, 10.12) * mm, "end": v(-80.36, 10.18) * mm});
            skEllipticalArc(sketch, "E74.3.3", {});
            skArc(sketch, "E74.3.4", {"start": v(-80.67, 10.1) * mm, "mid": v(-80.97, 9.85) * mm, "end": v(-81.02, 9.47) * mm});
            skLineSegment(sketch, "E74.4.0", {"start": v(-77.09, -3.64) * mm, "end": v(-77.55, 10.04) * mm});
            skLineSegment(sketch, "E74.4.1", {"start": v(-77.09, -3.64) * mm, "end": v(-78.86, 9.93) * mm});
            skArc(sketch, "E74.4.2", {"start": v(-77.55, 10.04) * mm, "mid": v(-77.71, 10.4) * mm, "end": v(-78.1, 10.52) * mm});
            skEllipticalArc(sketch, "E74.4.3", {});
            skArc(sketch, "E74.4.4", {"start": v(-78.42, 10.49) * mm, "mid": v(-78.75, 10.3) * mm, "end": v(-78.86, 9.93) * mm});
            skLineSegment(sketch, "E74.5.0", {"start": v(-77.09, -3.64) * mm, "end": v(-75.34, 9.94) * mm});
            skLineSegment(sketch, "E74.5.1", {"start": v(-77.09, -3.64) * mm, "end": v(-76.65, 10.04) * mm});
            skArc(sketch, "E74.5.2", {"start": v(-75.34, 9.94) * mm, "mid": v(-75.45, 10.32) * mm, "end": v(-75.8, 10.5) * mm});
            skEllipticalArc(sketch, "E74.5.3", {});
            skArc(sketch, "E74.5.4", {"start": v(-76.12, 10.52) * mm, "mid": v(-76.49, 10.39) * mm, "end": v(-76.65, 10.04) * mm});
            skLineSegment(sketch, "E74.6.0", {"start": v(-77.09, -3.64) * mm, "end": v(-73.18, 9.48) * mm});
            skLineSegment(sketch, "E74.6.1", {"start": v(-77.09, -3.64) * mm, "end": v(-74.45, 9.79) * mm});
            skArc(sketch, "E74.6.2", {"start": v(-73.18, 9.48) * mm, "mid": v(-73.22, 9.87) * mm, "end": v(-73.54, 10.1) * mm});
            skEllipticalArc(sketch, "E74.6.3", {});
            skArc(sketch, "E74.6.4", {"start": v(-73.86, 10.18) * mm, "mid": v(-74.24, 10.1) * mm, "end": v(-74.45, 9.79) * mm});
            skLineSegment(sketch, "E74.7.0", {"start": v(-77.09, -3.64) * mm, "end": v(-71.12, 8.68) * mm});
            skLineSegment(sketch, "E74.7.1", {"start": v(-77.09, -3.64) * mm, "end": v(-72.33, 9.19) * mm});
            skArc(sketch, "E74.7.2", {"start": v(-71.12, 8.68) * mm, "mid": v(-71.1, 9.07) * mm, "end": v(-71.37, 9.36) * mm});
            skEllipticalArc(sketch, "E74.7.3", {});
            skArc(sketch, "E74.7.4", {"start": v(-71.68, 9.48) * mm, "mid": v(-72.06, 9.47) * mm, "end": v(-72.33, 9.19) * mm});
            skLineSegment(sketch, "E74.8.0", {"start": v(-77.09, -3.64) * mm, "end": v(-69.21, 7.56) * mm});
            skLineSegment(sketch, "E74.8.1", {"start": v(-77.09, -3.64) * mm, "end": v(-70.33, 8.25) * mm});
            skArc(sketch, "E74.8.2", {"start": v(-69.21, 7.56) * mm, "mid": v(-69.13, 7.94) * mm, "end": v(-69.36, 8.27) * mm});
            skEllipticalArc(sketch, "E74.8.3", {});
            skArc(sketch, "E74.8.4", {"start": v(-69.64, 8.44) * mm, "mid": v(-70.02, 8.5) * mm, "end": v(-70.33, 8.25) * mm});
            skPoint(sketch, "E75.1.0.0", {"position": v(-57.78, -3.64) * mm});
            skLineSegment(sketch, "E75.1.0.1", {"start": v(-57.78, -3.64) * mm, "end": v(-51.81, 8.68) * mm});
            skLineSegment(sketch, "E75.1.0.2", {"start": v(-57.78, -3.64) * mm, "end": v(-62.56, 9.19) * mm});
            skLineSegment(sketch, "E75.1.0.3", {"start": v(-57.78, -3.64) * mm, "end": v(-57.34, 10.04) * mm});
            skLineSegment(sketch, "E75.1.0.4", {"start": v(-57.78, -3.64) * mm, "end": v(-51.02, 8.25) * mm});
            skLineSegment(sketch, "E75.1.0.5", {"start": v(-57.78, -3.64) * mm, "end": v(-55.15, 9.79) * mm});
            skLineSegment(sketch, "E75.1.0.6", {"start": v(-57.78, -3.64) * mm, "end": v(-49.9, 7.56) * mm});
            skLineSegment(sketch, "E75.1.0.7", {"start": v(-57.78, -3.64) * mm, "end": v(-58.24, 10.04) * mm});
            skLineSegment(sketch, "E75.1.0.8", {"start": v(-57.78, -3.64) * mm, "end": v(-53.02, 9.19) * mm});
            skLineSegment(sketch, "E75.1.0.9", {"start": v(-57.78, -3.64) * mm, "end": v(-65.67, 7.54) * mm});
            skLineSegment(sketch, "E75.1.0.10", {"start": v(-57.78, -3.64) * mm, "end": v(-53.87, 9.48) * mm});
            skLineSegment(sketch, "E75.1.0.11", {"start": v(-57.78, -3.64) * mm, "end": v(-60.44, 9.79) * mm});
            skLineSegment(sketch, "E75.1.0.12", {"start": v(-57.78, -3.64) * mm, "end": v(-61.7, 9.47) * mm});
            skLineSegment(sketch, "E75.1.0.13", {"start": v(-57.78, -3.64) * mm, "end": v(-56.03, 9.94) * mm});
            skLineSegment(sketch, "E75.1.0.14", {"start": v(-57.78, -3.64) * mm, "end": v(-63.77, 8.67) * mm});
            skLineSegment(sketch, "E75.1.0.15", {"start": v(-57.78, -3.64) * mm, "end": v(-59.55, 9.93) * mm});
            skLineSegment(sketch, "E75.1.0.16", {"start": v(-57.78, -3.64) * mm, "end": v(-64.56, 8.25) * mm});
            skPoint(sketch, "E75.1.0.17", {"position": v(-57.78, -3.64) * mm});
            skArc(sketch, "E75.1.0.18", {"start": v(-52.37, 9.48) * mm, "mid": v(-52.76, 9.47) * mm, "end": v(-53.02, 9.19) * mm});
            skEllipticalArc(sketch, "E75.1.0.19", {});
            skArc(sketch, "E75.1.0.20", {"start": v(-65.54, 8.24) * mm, "mid": v(-65.75, 7.92) * mm, "end": v(-65.67, 7.54) * mm});
            skEllipticalArc(sketch, "E75.1.0.21", {});
            skArc(sketch, "E75.1.0.22", {"start": v(-64.56, 8.25) * mm, "mid": v(-64.88, 8.5) * mm, "end": v(-65.27, 8.42) * mm});
            skArc(sketch, "E75.1.0.23", {"start": v(-51.81, 8.68) * mm, "mid": v(-51.8, 9.07) * mm, "end": v(-52.07, 9.36) * mm});
            skArc(sketch, "E75.1.0.24", {"start": v(-60.44, 9.79) * mm, "mid": v(-60.66, 10.12) * mm, "end": v(-61.05, 10.18) * mm});
            skArc(sketch, "E75.1.0.25", {"start": v(-62.56, 9.19) * mm, "mid": v(-62.84, 9.47) * mm, "end": v(-63.23, 9.47) * mm});
            skArc(sketch, "E75.1.0.26", {"start": v(-53.87, 9.48) * mm, "mid": v(-53.92, 9.87) * mm, "end": v(-54.23, 10.1) * mm});
            skEllipticalArc(sketch, "E75.1.0.27", {});
            skEllipticalArc(sketch, "E75.1.0.28", {});
            skArc(sketch, "E75.1.0.29", {"start": v(-54.55, 10.18) * mm, "mid": v(-54.93, 10.1) * mm, "end": v(-55.15, 9.79) * mm});
            skArc(sketch, "E75.1.0.30", {"start": v(-59.1, 10.49) * mm, "mid": v(-59.45, 10.3) * mm, "end": v(-59.55, 9.93) * mm});
            skArc(sketch, "E75.1.0.31", {"start": v(-56.03, 9.94) * mm, "mid": v(-56.14, 10.32) * mm, "end": v(-56.5, 10.5) * mm});
            skEllipticalArc(sketch, "E75.1.0.32", {});
            skArc(sketch, "E75.1.0.33", {"start": v(-61.37, 10.1) * mm, "mid": v(-61.67, 9.85) * mm, "end": v(-61.7, 9.47) * mm});
            skEllipticalArc(sketch, "E75.1.0.34", {});
            skArc(sketch, "E75.1.0.35", {"start": v(-50.33, 8.44) * mm, "mid": v(-50.71, 8.5) * mm, "end": v(-51.02, 8.25) * mm});
            skArc(sketch, "E75.1.0.36", {"start": v(-56.82, 10.52) * mm, "mid": v(-57.18, 10.39) * mm, "end": v(-57.34, 10.04) * mm});
            skArc(sketch, "E75.1.0.37", {"start": v(-58.24, 10.04) * mm, "mid": v(-58.4, 10.4) * mm, "end": v(-58.78, 10.52) * mm});
            skArc(sketch, "E75.1.0.38", {"start": v(-49.9, 7.56) * mm, "mid": v(-49.82, 7.94) * mm, "end": v(-50.05, 8.27) * mm});
            skArc(sketch, "E75.1.0.39", {"start": v(-63.53, 9.34) * mm, "mid": v(-63.79, 9.05) * mm, "end": v(-63.77, 8.67) * mm});
            skEllipticalArc(sketch, "E75.1.0.40", {});
            skPoint(sketch, "E75.2.0.0", {"position": v(-38.48, -3.64) * mm});
            skLineSegment(sketch, "E75.2.0.1", {"start": v(-38.48, -3.64) * mm, "end": v(-32.5, 8.68) * mm});
            skLineSegment(sketch, "E75.2.0.2", {"start": v(-38.48, -3.64) * mm, "end": v(-43.26, 9.19) * mm});
            skLineSegment(sketch, "E75.2.0.3", {"start": v(-38.48, -3.64) * mm, "end": v(-38.04, 10.04) * mm});
            skLineSegment(sketch, "E75.2.0.4", {"start": v(-38.48, -3.64) * mm, "end": v(-31.71, 8.25) * mm});
            skLineSegment(sketch, "E75.2.0.5", {"start": v(-38.48, -3.64) * mm, "end": v(-35.84, 9.79) * mm});
            skLineSegment(sketch, "E75.2.0.6", {"start": v(-38.48, -3.64) * mm, "end": v(-30.6, 7.56) * mm});
            skLineSegment(sketch, "E75.2.0.7", {"start": v(-38.48, -3.64) * mm, "end": v(-38.93, 10.04) * mm});
            skLineSegment(sketch, "E75.2.0.8", {"start": v(-38.48, -3.64) * mm, "end": v(-33.71, 9.19) * mm});
            skLineSegment(sketch, "E75.2.0.9", {"start": v(-38.48, -3.64) * mm, "end": v(-46.36, 7.54) * mm});
            skLineSegment(sketch, "E75.2.0.10", {"start": v(-38.48, -3.64) * mm, "end": v(-34.56, 9.48) * mm});
            skLineSegment(sketch, "E75.2.0.11", {"start": v(-38.48, -3.64) * mm, "end": v(-41.13, 9.79) * mm});
            skLineSegment(sketch, "E75.2.0.12", {"start": v(-38.48, -3.64) * mm, "end": v(-42.4, 9.47) * mm});
            skLineSegment(sketch, "E75.2.0.13", {"start": v(-38.48, -3.64) * mm, "end": v(-36.73, 9.94) * mm});
            skLineSegment(sketch, "E75.2.0.14", {"start": v(-38.48, -3.64) * mm, "end": v(-44.46, 8.67) * mm});
            skLineSegment(sketch, "E75.2.0.15", {"start": v(-38.48, -3.64) * mm, "end": v(-40.24, 9.93) * mm});
            skLineSegment(sketch, "E75.2.0.16", {"start": v(-38.48, -3.64) * mm, "end": v(-45.26, 8.25) * mm});
            skPoint(sketch, "E75.2.0.17", {"position": v(-38.48, -3.64) * mm});
            skArc(sketch, "E75.2.0.18", {"start": v(-33.06, 9.48) * mm, "mid": v(-33.45, 9.47) * mm, "end": v(-33.71, 9.19) * mm});
            skEllipticalArc(sketch, "E75.2.0.19", {});
            skArc(sketch, "E75.2.0.20", {"start": v(-46.24, 8.24) * mm, "mid": v(-46.45, 7.92) * mm, "end": v(-46.36, 7.54) * mm});
            skEllipticalArc(sketch, "E75.2.0.21", {});
            skArc(sketch, "E75.2.0.22", {"start": v(-45.26, 8.25) * mm, "mid": v(-45.57, 8.5) * mm, "end": v(-45.96, 8.42) * mm});
            skArc(sketch, "E75.2.0.23", {"start": v(-32.5, 8.68) * mm, "mid": v(-32.49, 9.07) * mm, "end": v(-32.76, 9.36) * mm});
            skArc(sketch, "E75.2.0.24", {"start": v(-41.13, 9.79) * mm, "mid": v(-41.35, 10.12) * mm, "end": v(-41.74, 10.18) * mm});
            skArc(sketch, "E75.2.0.25", {"start": v(-43.26, 9.19) * mm, "mid": v(-43.53, 9.47) * mm, "end": v(-43.92, 9.47) * mm});
            skArc(sketch, "E75.2.0.26", {"start": v(-34.56, 9.48) * mm, "mid": v(-34.6, 9.87) * mm, "end": v(-34.93, 10.1) * mm});
            skEllipticalArc(sketch, "E75.2.0.27", {});
            skEllipticalArc(sketch, "E75.2.0.28", {});
            skArc(sketch, "E75.2.0.29", {"start": v(-35.25, 10.18) * mm, "mid": v(-35.63, 10.1) * mm, "end": v(-35.84, 9.79) * mm});
            skArc(sketch, "E75.2.0.30", {"start": v(-39.8, 10.49) * mm, "mid": v(-40.14, 10.3) * mm, "end": v(-40.24, 9.93) * mm});
            skArc(sketch, "E75.2.0.31", {"start": v(-36.73, 9.94) * mm, "mid": v(-36.83, 10.32) * mm, "end": v(-37.19, 10.5) * mm});
            skEllipticalArc(sketch, "E75.2.0.32", {});
            skArc(sketch, "E75.2.0.33", {"start": v(-42.06, 10.1) * mm, "mid": v(-42.36, 9.85) * mm, "end": v(-42.4, 9.47) * mm});
            skEllipticalArc(sketch, "E75.2.0.34", {});
            skArc(sketch, "E75.2.0.35", {"start": v(-31.02, 8.44) * mm, "mid": v(-31.4, 8.5) * mm, "end": v(-31.71, 8.25) * mm});
            skArc(sketch, "E75.2.0.36", {"start": v(-37.51, 10.52) * mm, "mid": v(-37.87, 10.39) * mm, "end": v(-38.04, 10.04) * mm});
            skArc(sketch, "E75.2.0.37", {"start": v(-38.93, 10.04) * mm, "mid": v(-39.1, 10.4) * mm, "end": v(-39.48, 10.52) * mm});
            skArc(sketch, "E75.2.0.38", {"start": v(-30.6, 7.56) * mm, "mid": v(-30.52, 7.94) * mm, "end": v(-30.74, 8.27) * mm});
            skArc(sketch, "E75.2.0.39", {"start": v(-44.22, 9.34) * mm, "mid": v(-44.48, 9.05) * mm, "end": v(-44.46, 8.67) * mm});
            skEllipticalArc(sketch, "E75.2.0.40", {});
            skLineSegment(sketch, "E75.direction1", {"start": v(-77.09, -3.64) * mm, "end": v(-57.78, -3.64) * mm, "construction": true});
            skLineSegment(sketch, "E76", {"start": v(-59.1, 10.49) * mm, "end": v(-58.78, 10.52) * mm});
            skLineSegment(sketch, "E77", {"start": v(-39.8, 10.49) * mm, "end": v(-39.48, 10.52) * mm});
            const initialGuessF17  = {"E64.0": [-0.09612256447526175, -0.0013360511020651194, 0, 1, 0.014, 0.013965054578359462, 0.7180546312957505, 0.7398930087092236], "E70.1.3": [-0.09612256447526175, -0.0013360511020651198, 0.16086763624185027, 0.9869759893786473, 0.014, 0.013965054578359462, 0.718054631295751, 0.7398930087092235], "E70.2.3": [-0.09612256447526175, -0.001336051102065118, 0.317544988877609, 0.9482432072199195, 0.014, 0.013965054578359462, 0.718054631295751, 0.7398930087092231], "E70.3.3": [-0.09612256447526175, -0.001336051102065118, 0.4659509228975692, 0.8848105658562762, 0.014, 0.013965054578359462, 0.718054631295751, 0.7398930087092234], "E70.4.3": [-0.09612256447526175, -0.001336051102065118, 0.6022197573798352, 0.7983303600774383, 0.014, 0.01396505457835946, 0.7180546312957504, 0.739893008709224], "E70.5.3": [-0.09612256447526175, -0.0013360511020651194, 0.722801958829093, 0.6910552281206084, 0.014, 0.013965054578359462, 0.718054631295748, 0.7398930087092209], "E70.6.3": [-0.09612256447526175, -0.0013360511020651194, 0.8245565995005028, 0.5657794749018097, 0.014, 0.013965054578359462, 0.7180546312957475, 0.7398930087092203], "E70.7.3": [-0.09612256447526175, -0.0013360511020651194, 0.904833172352311, 0.4257662859020819, 0.014, 0.013965054578359462, 0.718054631295746, 0.7398930087092198], "E70.8.3": [-0.09612256447526175, -0.0013360511020651194, 0.9615406315095817, 0.2746627276427487, 0.014, 0.013965054578359462, 0.7180546312957461, 0.7398930087092197], "E70.9.3": [-0.09612256447526175, -0.0013360511020651194, 0.9932018598715668, 0.11640474881919785, 0.014, 0.013965054578359462, 0.7180546312957454, 0.7398930087092193], "E74.1.3": [-0.07708931073374041, -0.003644061778911401, 0.160867636241799, 0.9869759893786557, 0.014323932052886448, 0.014046620573596253, 0.7265398216981758, 0.7495844923670351], "E74.2.3": [-0.07708931075018732, -0.0036440627026220612, 0.3175448508741828, 0.9482432534341034, 0.014323932052886448, 0.014046620573596253, 0.7265398216981759, 0.7495844923670342], "E74.3.3": [-0.07708931091501504, -0.0036440636116565443, 0.4659506653542021, 0.8848107014813827, 0.014323932052886448, 0.014046620573596253, 0.726539821698176, 0.749584492367036], "E74.4.3": [-0.07708931122393015, -0.003644064482336354, 0.602219408822693, 0.7983306230110719, 0.014323932052886448, 0.014046620573596253, 0.7265398216981779, 0.7495844923670363], "E74.5.3": [-0.07708931166888604, -0.0036440652919820377, 0.7228015565357182, 0.6910556488948941, 0.014323932052886448, 0.014046620573596253, 0.7265398216981772, 0.7495844923670363], "E74.6.3": [-0.07708931223829249, -0.003644066019503976, 0.8245561877942955, 0.5657800749143952, 0.014323932052886448, 0.014046620573596253, 0.7265398216981775, 0.749584492367036], "E74.7.3": [-0.07708931291731765, -0.0036440666459516824, 0.9048328005664158, 0.4257670760159087, 0.014323932052886448, 0.014046620573596253, 0.7265398216981768, 0.7495844923670354], "E74.8.3": [-0.07708931368827424, -0.003644067155007466, 0.9615403516961704, 0.27466370721303013, 0.014323932052886448, 0.014046620573596253, 0.7265398216981767, 0.7495844923670362], "E75.1.0.19": [-0.057782832917317645, -0.0036440666459516824, 0.904832800566416, 0.4257670760159088, 0.014323932052886448, 0.014046620573596253, 0.7265398216981768, 0.7495844923670354], "E75.1.0.21": [-0.05778283073374041, -0.003644061778911401, 0.160867636241799, 0.9869759893786557, 0.014323932052886448, 0.014046620573596253, 0.7265398216981755, 0.7495844923670351], "E75.1.0.27": [-0.05778283166888604, -0.0036440652919820377, 0.7228015565357182, 0.6910556488948941, 0.014323932052886448, 0.014046620573596253, 0.7265398216981772, 0.7495844923670363], "E75.1.0.28": [-0.05778283091501504, -0.0036440636116565443, 0.4659506653542021, 0.8848107014813827, 0.014323932052886448, 0.014046620573596253, 0.726539821698176, 0.749584492367036], "E75.1.0.32": [-0.057782833688274235, -0.003644067155007466, 0.9615403516961704, 0.27466370721303013, 0.014323932052886448, 0.014046620573596253, 0.7265398216981767, 0.7495844923670362], "E75.1.0.34": [-0.05778283075018732, -0.0036440627026220612, 0.3175448508741828, 0.9482432534341034, 0.014323932052886448, 0.014046620573596253, 0.7265398216981759, 0.7495844923670342], "E75.1.0.40": [-0.05778283223829249, -0.003644066019503976, 0.8245561877942955, 0.5657800749143952, 0.014323932052886448, 0.014046620573596253, 0.7265398216981775, 0.749584492367036], "E75.2.0.19": [-0.038476352917317644, -0.0036440666459516824, 0.904832800566416, 0.4257670760159088, 0.014323932052886448, 0.014046620573596253, 0.7265398216981768, 0.7495844923670354], "E75.2.0.21": [-0.03847635073374041, -0.003644061778911401, 0.160867636241799, 0.9869759893786557, 0.014323932052886448, 0.014046620573596253, 0.7265398216981755, 0.7495844923670351], "E75.2.0.27": [-0.038476351668886036, -0.0036440652919820377, 0.7228015565357182, 0.6910556488948941, 0.014323932052886448, 0.014046620573596253, 0.7265398216981772, 0.7495844923670363], "E75.2.0.28": [-0.03847635091501504, -0.0036440636116565443, 0.4659506653542021, 0.8848107014813827, 0.014323932052886448, 0.014046620573596253, 0.726539821698176, 0.749584492367036], "E75.2.0.32": [-0.038476353688274234, -0.003644067155007466, 0.9615403516961704, 0.27466370721303013, 0.014323932052886448, 0.014046620573596253, 0.7265398216981767, 0.7495844923670362], "E75.2.0.34": [-0.03847635075018732, -0.0036440627026220612, 0.3175448508741828, 0.9482432534341034, 0.014323932052886448, 0.014046620573596253, 0.7265398216981759, 0.7495844923670342], "E75.2.0.40": [-0.03847635223829249, -0.003644066019503976, 0.8245561877942955, 0.5657800749143952, 0.014323932052886448, 0.014046620573596253, 0.7265398216981775, 0.749584492367036]};
            skSetInitialGuess(sketch, initialGuessF17);
            skSolve(sketch);
        }
        {
            var Q0;
            Q0=qSketchRegion(id+"F17",true);
            extrude(context, id + "F18", {"entities" : qUnion([Q0]), "operationType" : NewBodyOperationType.REMOVE, "endBound" : BoundingType.SYMMETRIC, "oppositeDirection" : true, "depth" : 40 * mm});
        }
        {
            var Q0;
            Q0=qCreatedBy(makeId("Top.planeOp"),FACE);
            var sketch = newSketch(context, id + "F19", { "sketchPlane" : qUnion([Q0])});
            skLineSegment(sketch, "E78", {"start": v(-184.13, -4.68) * mm, "end": v(-184.13, -15.98) * mm});
            skLineSegment(sketch, "E79", {"start": v(-184.13, -4.68) * mm, "end": v(-231.1, -4.68) * mm});
            skLineSegment(sketch, "E80", {"start": v(-231.1, -15.98) * mm, "end": v(-231.1, -4.68) * mm});
            skLineSegment(sketch, "E81", {"start": v(-231.1, -15.98) * mm, "end": v(-184.13, -15.98) * mm});
            skPoint(sketch, "E82.0", {"position": v(-184.13, -7.66) * mm});
            skSolve(sketch);
        }
        {
            var Q0;
            Q0=makeQuery(id+"F19.imprint","IMPRINT",FACE,{"disambiguationData":[TD([[makeQuery(id+"F19.imprint","IMPRINT",EDGE,{"derivedFrom":sQuery(id+"F19.wireOp",EDGE,"E78")}),-1.0]])]});
            extrude(context, id + "F20", {"entities" : qUnion([Q0]), "endBound" : BoundingType.SYMMETRIC, "depth" : 30 * mm});
        }
        {
            var Q0;
            Q0=makeQuery(id+"F1.opExtrude","SWEPT_BODY",BODY,{"disambiguationData":[OSD([sQuery(id+"F0.wireOp",EDGE,"E1"),sQuery(id+"F0.wireOp",EDGE,"E8"),sQuery(id+"F0.wireOp",EDGE,"E9"),sQuery(id+"F0.wireOp",EDGE,"E10"),sQuery(id+"F0.wireOp",EDGE,"E11"),sQuery(id+"F0.wireOp",EDGE,"E12"),sQuery(id+"F0.wireOp",EDGE,"E13"),sQuery(id+"F0.wireOp",EDGE,"E14"),sQuery(id+"F0.wireOp",EDGE,"E15"),sQuery(id+"F0.wireOp",EDGE,"E16.MirrorCS"),sQuery(id+"F0.wireOp",EDGE,"E17.MirrorCS"),sQuery(id+"F0.wireOp",EDGE,"E18.MirrorCS"),sQuery(id+"F0.wireOp",EDGE,"E19.MirrorCS"),sQuery(id+"F0.wireOp",EDGE,"E20.MirrorCS"),sQuery(id+"F0.wireOp",EDGE,"E21.MirrorCS"),sQuery(id+"F0.wireOp",EDGE,"E22.MirrorCS"),sQuery(id+"F0.wireOp",EDGE,"E23.MirrorCS"),sQuery(id+"F0.wireOp",EDGE,"E24.MirrorCS")])]});
            var Q1;
            Q1=makeQuery(id+"F20.opExtrude","SWEPT_BODY",BODY,{"disambiguationData":[OSD([sQuery(id+"F19.wireOp",EDGE,"E78"),sQuery(id+"F19.wireOp",EDGE,"E79"),sQuery(id+"F19.wireOp",EDGE,"E80"),sQuery(id+"F19.wireOp",EDGE,"E81")])]});
            booleanBodies(context, id + "F21", {"operationType" : BooleanOperationType.INTERSECTION, "tools" : qUnion([Q0, Q1]), "keepTools" : true});
        }
        {
            var Q0;
            Q0=makeQuery(id+"F21.opBoolean","INTERSECT",BODY,{"derivedFrom":[makeQuery(id+"F1.opExtrude","SWEPT_BODY",BODY,{"disambiguationData":[OSD([sQuery(id+"F0.wireOp",EDGE,"E1"),sQuery(id+"F0.wireOp",EDGE,"E8"),sQuery(id+"F0.wireOp",EDGE,"E9"),sQuery(id+"F0.wireOp",EDGE,"E10"),sQuery(id+"F0.wireOp",EDGE,"E11"),sQuery(id+"F0.wireOp",EDGE,"E12"),sQuery(id+"F0.wireOp",EDGE,"E13"),sQuery(id+"F0.wireOp",EDGE,"E14"),sQuery(id+"F0.wireOp",EDGE,"E15"),sQuery(id+"F0.wireOp",EDGE,"E16.MirrorCS"),sQuery(id+"F0.wireOp",EDGE,"E17.MirrorCS"),sQuery(id+"F0.wireOp",EDGE,"E18.MirrorCS"),sQuery(id+"F0.wireOp",EDGE,"E19.MirrorCS"),sQuery(id+"F0.wireOp",EDGE,"E20.MirrorCS"),sQuery(id+"F0.wireOp",EDGE,"E21.MirrorCS"),sQuery(id+"F0.wireOp",EDGE,"E22.MirrorCS"),sQuery(id+"F0.wireOp",EDGE,"E23.MirrorCS"),sQuery(id+"F0.wireOp",EDGE,"E24.MirrorCS")])]}),makeQuery(id+"F20.opExtrude","SWEPT_BODY",BODY,{"disambiguationData":[OSD([sQuery(id+"F19.wireOp",EDGE,"E78"),sQuery(id+"F19.wireOp",EDGE,"E79"),sQuery(id+"F19.wireOp",EDGE,"E80"),sQuery(id+"F19.wireOp",EDGE,"E81")])]})]});
            var Q1;
            Q1=makeQuery(id+"F1.opExtrude","SWEPT_BODY",BODY,{"disambiguationData":[OSD([sQuery(id+"F0.wireOp",EDGE,"E1"),sQuery(id+"F0.wireOp",EDGE,"E8"),sQuery(id+"F0.wireOp",EDGE,"E9"),sQuery(id+"F0.wireOp",EDGE,"E10"),sQuery(id+"F0.wireOp",EDGE,"E11"),sQuery(id+"F0.wireOp",EDGE,"E12"),sQuery(id+"F0.wireOp",EDGE,"E13"),sQuery(id+"F0.wireOp",EDGE,"E14"),sQuery(id+"F0.wireOp",EDGE,"E15"),sQuery(id+"F0.wireOp",EDGE,"E16.MirrorCS"),sQuery(id+"F0.wireOp",EDGE,"E17.MirrorCS"),sQuery(id+"F0.wireOp",EDGE,"E18.MirrorCS"),sQuery(id+"F0.wireOp",EDGE,"E19.MirrorCS"),sQuery(id+"F0.wireOp",EDGE,"E20.MirrorCS"),sQuery(id+"F0.wireOp",EDGE,"E21.MirrorCS"),sQuery(id+"F0.wireOp",EDGE,"E22.MirrorCS"),sQuery(id+"F0.wireOp",EDGE,"E23.MirrorCS"),sQuery(id+"F0.wireOp",EDGE,"E24.MirrorCS")])]});
            booleanBodies(context, id + "F22", {"operationType" : BooleanOperationType.SUBTRACTION, "tools" : qUnion([Q0]), "targets" : qUnion([Q1]), "keepTools" : true});
        }
        {
            var Q0;
            Q0=makeQuery(id+"F21.opBoolean","COPY",FACE,{"derivedFrom":makeQuery(id+"F3.boolean.opBoolean","COPY",FACE,{"derivedFrom":makeQuery(id+"F3.opExtrude","SWEPT_FACE",FACE,{"disambiguationData":[OSD([sQuery(id+"F2.wireOp",EDGE,"E44")])]})})});
            var sketch = newSketch(context, id + "F23", { "sketchPlane" : qUnion([Q0])});
            skCircle(sketch, "E83.2.0.1", {"center": v(-215.28, 3.65) * mm, "radius": 0.5 * mm});
            skCircle(sketch, "E83.2.0.2", {"center": v(-212.5, 3.65) * mm, "radius": 0.5 * mm});
            skCircle(sketch, "E83.2.0.3", {"center": v(-209.71, 3.65) * mm, "radius": 0.5 * mm});
            skCircle(sketch, "E83.2.0.4", {"center": v(-206.93, 3.65) * mm, "radius": 0.5 * mm});
            skCircle(sketch, "E83.2.0.5", {"center": v(-204.15, 3.65) * mm, "radius": 0.5 * mm});
            skCircle(sketch, "E83.2.0.6", {"center": v(-201.36, 3.65) * mm, "radius": 0.5 * mm});
            skCircle(sketch, "E83.2.0.7", {"center": v(-198.58, 3.65) * mm, "radius": 0.5 * mm});
            skCircle(sketch, "E83.2.0.8", {"center": v(-195.8, 3.65) * mm, "radius": 0.5 * mm});
            skCircle(sketch, "E83.2.0.9", {"center": v(-193.01, 3.65) * mm, "radius": 0.5 * mm});
            skCircle(sketch, "E83.2.0.10", {"center": v(-190.23, 3.65) * mm, "radius": 0.5 * mm});
            skCircle(sketch, "E83.2.0.11", {"center": v(-187.45, 3.65) * mm, "radius": 0.5 * mm});
            skCircle(sketch, "E83.3.0.0", {"center": v(-218.08, 1.23) * mm, "radius": 0.5 * mm});
            skCircle(sketch, "E83.3.0.1", {"center": v(-215.3, 1.23) * mm, "radius": 0.5 * mm});
            skCircle(sketch, "E83.3.0.2", {"center": v(-212.51, 1.23) * mm, "radius": 0.5 * mm});
            skCircle(sketch, "E83.3.0.3", {"center": v(-209.73, 1.23) * mm, "radius": 0.5 * mm});
            skCircle(sketch, "E83.3.0.4", {"center": v(-206.94, 1.23) * mm, "radius": 0.5 * mm});
            skCircle(sketch, "E83.3.0.5", {"center": v(-204.16, 1.23) * mm, "radius": 0.5 * mm});
            skCircle(sketch, "E83.3.0.6", {"center": v(-201.38, 1.23) * mm, "radius": 0.5 * mm});
            skCircle(sketch, "E83.3.0.7", {"center": v(-198.6, 1.23) * mm, "radius": 0.5 * mm});
            skCircle(sketch, "E83.3.0.8", {"center": v(-195.81, 1.23) * mm, "radius": 0.5 * mm});
            skCircle(sketch, "E83.3.0.9", {"center": v(-193.03, 1.23) * mm, "radius": 0.5 * mm});
            skCircle(sketch, "E83.3.0.10", {"center": v(-190.25, 1.23) * mm, "radius": 0.5 * mm});
            skCircle(sketch, "E83.3.0.11", {"center": v(-187.46, 1.23) * mm, "radius": 0.5 * mm});
            skCircle(sketch, "E83.4.0.0", {"center": v(-218.1, -1.2) * mm, "radius": 0.5 * mm});
            skCircle(sketch, "E83.4.0.1", {"center": v(-215.3, -1.2) * mm, "radius": 0.5 * mm});
            skCircle(sketch, "E83.4.0.2", {"center": v(-212.53, -1.2) * mm, "radius": 0.5 * mm});
            skCircle(sketch, "E83.4.0.3", {"center": v(-209.74, -1.2) * mm, "radius": 0.5 * mm});
            skCircle(sketch, "E83.4.0.4", {"center": v(-206.96, -1.2) * mm, "radius": 0.5 * mm});
            skCircle(sketch, "E83.4.0.5", {"center": v(-204.18, -1.2) * mm, "radius": 0.5 * mm});
            skCircle(sketch, "E83.4.0.6", {"center": v(-201.4, -1.2) * mm, "radius": 0.5 * mm});
            skCircle(sketch, "E83.4.0.7", {"center": v(-198.61, -1.2) * mm, "radius": 0.5 * mm});
            skCircle(sketch, "E83.4.0.8", {"center": v(-195.83, -1.2) * mm, "radius": 0.5 * mm});
            skCircle(sketch, "E83.4.0.9", {"center": v(-193.04, -1.2) * mm, "radius": 0.5 * mm});
            skCircle(sketch, "E83.4.0.10", {"center": v(-190.26, -1.2) * mm, "radius": 0.5 * mm});
            skCircle(sketch, "E83.4.0.11", {"center": v(-187.48, -1.2) * mm, "radius": 0.5 * mm});
            skCircle(sketch, "E83.5.0.1", {"center": v(-215.33, -3.62) * mm, "radius": 0.5 * mm});
            skCircle(sketch, "E83.5.0.2", {"center": v(-212.54, -3.62) * mm, "radius": 0.5 * mm});
            skCircle(sketch, "E83.5.0.3", {"center": v(-209.76, -3.62) * mm, "radius": 0.5 * mm});
            skCircle(sketch, "E83.5.0.4", {"center": v(-206.98, -3.62) * mm, "radius": 0.5 * mm});
            skCircle(sketch, "E83.5.0.5", {"center": v(-204.2, -3.62) * mm, "radius": 0.5 * mm});
            skCircle(sketch, "E83.5.0.6", {"center": v(-201.41, -3.62) * mm, "radius": 0.5 * mm});
            skCircle(sketch, "E83.5.0.7", {"center": v(-198.63, -3.62) * mm, "radius": 0.5 * mm});
            skCircle(sketch, "E83.5.0.8", {"center": v(-195.84, -3.62) * mm, "radius": 0.5 * mm});
            skCircle(sketch, "E83.5.0.9", {"center": v(-193.06, -3.62) * mm, "radius": 0.5 * mm});
            skCircle(sketch, "E83.5.0.10", {"center": v(-190.28, -3.62) * mm, "radius": 0.5 * mm});
            skCircle(sketch, "E83.5.0.11", {"center": v(-187.5, -3.62) * mm, "radius": 0.5 * mm});
            skCircle(sketch, "E84", {"center": v(-199.98, 5.12) * mm, "radius": 0.53 * mm});
            skCircle(sketch, "E85", {"center": v(-197.32, 5.26) * mm, "radius": 0.53 * mm});
            skCircle(sketch, "E86", {"center": v(-194.56, 5.64) * mm, "radius": 0.52 * mm});
            skCircle(sketch, "E87", {"center": v(-192.15, 5.67) * mm, "radius": 0.52 * mm});
            skCircle(sketch, "E88", {"center": v(-189.5, 5.2) * mm, "radius": 0.53 * mm});
            skCircle(sketch, "E89", {"center": v(-217.48, 3.14) * mm, "radius": 0.5 * mm});
            skLineSegment(sketch, "E90", {"start": v(-185.17, 0) * mm, "end": v(-221.81, 0.11) * mm, "construction": true});
            skCircle(sketch, "E91.MirrorC", {"center": v(-189.53, -5.17) * mm, "radius": 0.53 * mm});
            skCircle(sketch, "E92.MirrorC", {"center": v(-192.18, -5.63) * mm, "radius": 0.52 * mm});
            skCircle(sketch, "E93.MirrorC", {"center": v(-194.6, -5.58) * mm, "radius": 0.52 * mm});
            skCircle(sketch, "E94.MirrorC", {"center": v(-197.35, -5.19) * mm, "radius": 0.53 * mm});
            skCircle(sketch, "E95.MirrorC", {"center": v(-200, -5.03) * mm, "radius": 0.53 * mm});
            skCircle(sketch, "E96.MirrorC", {"center": v(-217.5, -2.94) * mm, "radius": 0.5 * mm});
            skCircle(sketch, "E97", {"center": v(-213.9, 2.44) * mm, "radius": 0.5 * mm});
            skLineSegment(sketch, "E98", {"start": v(-215.28, 3.65) * mm, "end": v(-212.51, 1.23) * mm, "construction": true});
            skLineSegment(sketch, "E99", {"start": v(-215.3, 1.23) * mm, "end": v(-212.5, 3.65) * mm, "construction": true});
            skCircle(sketch, "E100.1.0.0", {"center": v(-211.1, 2.44) * mm, "radius": 0.5 * mm});
            skCircle(sketch, "E100.2.0.0", {"center": v(-208.3, 2.44) * mm, "radius": 0.5 * mm});
            skCircle(sketch, "E100.3.0.0", {"center": v(-205.5, 2.44) * mm, "radius": 0.5 * mm});
            skCircle(sketch, "E100.4.0.0", {"center": v(-202.7, 2.44) * mm, "radius": 0.5 * mm});
            skCircle(sketch, "E100.5.0.0", {"center": v(-199.9, 2.44) * mm, "radius": 0.5 * mm});
            skCircle(sketch, "E100.6.0.0", {"center": v(-197.1, 2.44) * mm, "radius": 0.5 * mm});
            skCircle(sketch, "E100.7.0.0", {"center": v(-194.3, 2.44) * mm, "radius": 0.5 * mm});
            skCircle(sketch, "E100.8.0.0", {"center": v(-191.5, 2.44) * mm, "radius": 0.5 * mm});
            skCircle(sketch, "E100.9.0.0", {"center": v(-188.7, 2.44) * mm, "radius": 0.5 * mm});
            skCircle(sketch, "E100.10.0.0", {"center": v(-185.9, 2.44) * mm, "radius": 0.5 * mm});
            skLineSegment(sketch, "E100.direction1", {"start": v(-213.9, 2.44) * mm, "end": v(-211.1, 2.44) * mm, "construction": true});
            skCircle(sketch, "E101.1.0.0", {"center": v(-213.93, 0.01) * mm, "radius": 0.5 * mm});
            skCircle(sketch, "E101.1.0.1", {"center": v(-211.13, 0.01) * mm, "radius": 0.5 * mm});
            skCircle(sketch, "E101.1.0.2", {"center": v(-208.34, 0.01) * mm, "radius": 0.5 * mm});
            skCircle(sketch, "E101.1.0.3", {"center": v(-205.54, 0.01) * mm, "radius": 0.5 * mm});
            skCircle(sketch, "E101.1.0.4", {"center": v(-202.74, 0.01) * mm, "radius": 0.5 * mm});
            skCircle(sketch, "E101.1.0.5", {"center": v(-199.94, 0.01) * mm, "radius": 0.5 * mm});
            skCircle(sketch, "E101.1.0.6", {"center": v(-197.14, 0.01) * mm, "radius": 0.5 * mm});
            skCircle(sketch, "E101.1.0.7", {"center": v(-194.34, 0.01) * mm, "radius": 0.5 * mm});
            skCircle(sketch, "E101.1.0.8", {"center": v(-191.54, 0.01) * mm, "radius": 0.5 * mm});
            skCircle(sketch, "E101.1.0.9", {"center": v(-188.74, 0.01) * mm, "radius": 0.5 * mm});
            skCircle(sketch, "E101.1.0.10", {"center": v(-185.95, 0.01) * mm, "radius": 0.5 * mm});
            skCircle(sketch, "E101.2.0.0", {"center": v(-213.97, -2.42) * mm, "radius": 0.5 * mm});
            skCircle(sketch, "E101.2.0.1", {"center": v(-211.17, -2.42) * mm, "radius": 0.5 * mm});
            skCircle(sketch, "E101.2.0.2", {"center": v(-208.37, -2.42) * mm, "radius": 0.5 * mm});
            skCircle(sketch, "E101.2.0.3", {"center": v(-205.58, -2.42) * mm, "radius": 0.5 * mm});
            skCircle(sketch, "E101.2.0.4", {"center": v(-202.78, -2.42) * mm, "radius": 0.5 * mm});
            skCircle(sketch, "E101.2.0.5", {"center": v(-199.98, -2.42) * mm, "radius": 0.5 * mm});
            skCircle(sketch, "E101.2.0.6", {"center": v(-197.18, -2.42) * mm, "radius": 0.5 * mm});
            skCircle(sketch, "E101.2.0.7", {"center": v(-194.38, -2.42) * mm, "radius": 0.5 * mm});
            skCircle(sketch, "E101.2.0.8", {"center": v(-191.58, -2.42) * mm, "radius": 0.5 * mm});
            skCircle(sketch, "E101.2.0.9", {"center": v(-188.78, -2.42) * mm, "radius": 0.5 * mm});
            skCircle(sketch, "E101.2.0.10", {"center": v(-185.99, -2.42) * mm, "radius": 0.5 * mm});
            skLineSegment(sketch, "E101.direction1", {"start": v(-213.9, 2.44) * mm, "end": v(-213.93, 0.01) * mm, "construction": true});
            skCircle(sketch, "E102", {"center": v(-202.7, 4.67) * mm, "radius": 0.5 * mm});
            skCircle(sketch, "E103", {"center": v(-205.5, 4.47) * mm, "radius": 0.5 * mm});
            skCircle(sketch, "E104", {"center": v(-208.3, 4.47) * mm, "radius": 0.5 * mm});
            skCircle(sketch, "E105", {"center": v(-216.69, 0.1) * mm, "radius": 0.51 * mm});
            skCircle(sketch, "E106", {"center": v(-216.67, 2.07) * mm, "radius": 0.54 * mm});
            skCircle(sketch, "E107", {"center": v(-216.67, -1.73) * mm, "radius": 0.54 * mm});
            skCircle(sketch, "E108.MirrorC", {"center": v(-208.32, -4.33) * mm, "radius": 0.5 * mm});
            skCircle(sketch, "E109.MirrorC", {"center": v(-205.52, -4.35) * mm, "radius": 0.5 * mm});
            skCircle(sketch, "E110.MirrorC", {"center": v(-202.73, -4.56) * mm, "radius": 0.5 * mm});
            skSolve(sketch);
        }
        {
            var Q0;
            Q0=makeQuery(id+"F23.imprint","IMPRINT",FACE,{"disambiguationData":[TD([[makeQuery(id+"F23.imprint","IMPRINT",EDGE,{"derivedFrom":sQuery(id+"F23.wireOp",EDGE,"E83.2.0.1")}),1.0]])]});
            var Q1;
            Q1=makeQuery(id+"F23.imprint","IMPRINT",FACE,{"disambiguationData":[TD([[makeQuery(id+"F23.imprint","IMPRINT",EDGE,{"derivedFrom":sQuery(id+"F23.wireOp",EDGE,"E83.2.0.2")}),1.0]])]});
            var Q2;
            Q2=makeQuery(id+"F23.imprint","IMPRINT",FACE,{"disambiguationData":[TD([[makeQuery(id+"F23.imprint","IMPRINT",EDGE,{"derivedFrom":sQuery(id+"F23.wireOp",EDGE,"E83.2.0.3")}),1.0]])]});
            var Q3;
            Q3=makeQuery(id+"F23.imprint","IMPRINT",FACE,{"disambiguationData":[TD([[makeQuery(id+"F23.imprint","IMPRINT",EDGE,{"derivedFrom":sQuery(id+"F23.wireOp",EDGE,"E83.2.0.4")}),1.0]])]});
            var Q4;
            Q4=makeQuery(id+"F23.imprint","IMPRINT",FACE,{"disambiguationData":[TD([[makeQuery(id+"F23.imprint","IMPRINT",EDGE,{"derivedFrom":sQuery(id+"F23.wireOp",EDGE,"E83.2.0.5")}),1.0]])]});
            var Q5;
            Q5=makeQuery(id+"F23.imprint","IMPRINT",FACE,{"disambiguationData":[TD([[makeQuery(id+"F23.imprint","IMPRINT",EDGE,{"derivedFrom":sQuery(id+"F23.wireOp",EDGE,"E83.2.0.6")}),1.0]])]});
            var Q6;
            Q6=makeQuery(id+"F23.imprint","IMPRINT",FACE,{"disambiguationData":[TD([[makeQuery(id+"F23.imprint","IMPRINT",EDGE,{"derivedFrom":sQuery(id+"F23.wireOp",EDGE,"E83.2.0.7")}),1.0]])]});
            var Q7;
            Q7=makeQuery(id+"F23.imprint","IMPRINT",FACE,{"disambiguationData":[TD([[makeQuery(id+"F23.imprint","IMPRINT",EDGE,{"derivedFrom":sQuery(id+"F23.wireOp",EDGE,"E83.2.0.8")}),1.0]])]});
            var Q8;
            Q8=makeQuery(id+"F23.imprint","IMPRINT",FACE,{"disambiguationData":[TD([[makeQuery(id+"F23.imprint","IMPRINT",EDGE,{"derivedFrom":sQuery(id+"F23.wireOp",EDGE,"E83.2.0.9")}),1.0]])]});
            var Q9;
            Q9=makeQuery(id+"F23.imprint","IMPRINT",FACE,{"disambiguationData":[TD([[makeQuery(id+"F23.imprint","IMPRINT",EDGE,{"derivedFrom":sQuery(id+"F23.wireOp",EDGE,"E83.2.0.10")}),1.0]])]});
            var Q10;
            Q10=makeQuery(id+"F23.imprint","IMPRINT",FACE,{"disambiguationData":[TD([[makeQuery(id+"F23.imprint","IMPRINT",EDGE,{"derivedFrom":sQuery(id+"F23.wireOp",EDGE,"E83.2.0.11")}),1.0]])]});
            var Q11;
            Q11=makeQuery(id+"F23.imprint","IMPRINT",FACE,{"disambiguationData":[TD([[makeQuery(id+"F23.imprint","IMPRINT",EDGE,{"derivedFrom":sQuery(id+"F23.wireOp",EDGE,"E83.3.0.0")}),1.0]])]});
            var Q12;
            Q12=makeQuery(id+"F23.imprint","IMPRINT",FACE,{"disambiguationData":[TD([[makeQuery(id+"F23.imprint","IMPRINT",EDGE,{"derivedFrom":sQuery(id+"F23.wireOp",EDGE,"E83.3.0.1")}),1.0]])]});
            var Q13;
            Q13=makeQuery(id+"F23.imprint","IMPRINT",FACE,{"disambiguationData":[TD([[makeQuery(id+"F23.imprint","IMPRINT",EDGE,{"derivedFrom":sQuery(id+"F23.wireOp",EDGE,"E83.4.0.0")}),1.0]])]});
            var Q14;
            Q14=makeQuery(id+"F23.imprint","IMPRINT",FACE,{"disambiguationData":[TD([[makeQuery(id+"F23.imprint","IMPRINT",EDGE,{"derivedFrom":sQuery(id+"F23.wireOp",EDGE,"E83.4.0.1")}),1.0]])]});
            var Q15;
            Q15=makeQuery(id+"F23.imprint","IMPRINT",FACE,{"disambiguationData":[TD([[makeQuery(id+"F23.imprint","IMPRINT",EDGE,{"derivedFrom":sQuery(id+"F23.wireOp",EDGE,"E83.5.0.1")}),1.0]])]});
            var Q16;
            Q16=makeQuery(id+"F23.imprint","IMPRINT",FACE,{"disambiguationData":[TD([[makeQuery(id+"F23.imprint","IMPRINT",EDGE,{"derivedFrom":sQuery(id+"F23.wireOp",EDGE,"E83.5.0.2")}),1.0]])]});
            var Q17;
            Q17=makeQuery(id+"F23.imprint","IMPRINT",FACE,{"disambiguationData":[TD([[makeQuery(id+"F23.imprint","IMPRINT",EDGE,{"derivedFrom":sQuery(id+"F23.wireOp",EDGE,"E83.5.0.3")}),1.0]])]});
            var Q18;
            Q18=makeQuery(id+"F23.imprint","IMPRINT",FACE,{"disambiguationData":[TD([[makeQuery(id+"F23.imprint","IMPRINT",EDGE,{"derivedFrom":sQuery(id+"F23.wireOp",EDGE,"E83.5.0.4")}),1.0]])]});
            var Q19;
            Q19=makeQuery(id+"F23.imprint","IMPRINT",FACE,{"disambiguationData":[TD([[makeQuery(id+"F23.imprint","IMPRINT",EDGE,{"derivedFrom":sQuery(id+"F23.wireOp",EDGE,"E83.5.0.5")}),1.0]])]});
            var Q20;
            Q20=makeQuery(id+"F23.imprint","IMPRINT",FACE,{"disambiguationData":[TD([[makeQuery(id+"F23.imprint","IMPRINT",EDGE,{"derivedFrom":sQuery(id+"F23.wireOp",EDGE,"E83.5.0.6")}),1.0]])]});
            var Q21;
            Q21=makeQuery(id+"F23.imprint","IMPRINT",FACE,{"disambiguationData":[TD([[makeQuery(id+"F23.imprint","IMPRINT",EDGE,{"derivedFrom":sQuery(id+"F23.wireOp",EDGE,"E83.5.0.7")}),1.0]])]});
            var Q22;
            Q22=makeQuery(id+"F23.imprint","IMPRINT",FACE,{"disambiguationData":[TD([[makeQuery(id+"F23.imprint","IMPRINT",EDGE,{"derivedFrom":sQuery(id+"F23.wireOp",EDGE,"E83.5.0.8")}),1.0]])]});
            var Q23;
            Q23=makeQuery(id+"F23.imprint","IMPRINT",FACE,{"disambiguationData":[TD([[makeQuery(id+"F23.imprint","IMPRINT",EDGE,{"derivedFrom":sQuery(id+"F23.wireOp",EDGE,"E83.5.0.9")}),1.0]])]});
            var Q24;
            Q24=makeQuery(id+"F23.imprint","IMPRINT",FACE,{"disambiguationData":[TD([[makeQuery(id+"F23.imprint","IMPRINT",EDGE,{"derivedFrom":sQuery(id+"F23.wireOp",EDGE,"E83.5.0.10")}),1.0]])]});
            var Q25;
            Q25=makeQuery(id+"F23.imprint","IMPRINT",FACE,{"disambiguationData":[TD([[makeQuery(id+"F23.imprint","IMPRINT",EDGE,{"derivedFrom":sQuery(id+"F23.wireOp",EDGE,"E83.5.0.11")}),1.0]])]});
            var Q26;
            Q26=makeQuery(id+"F23.imprint","IMPRINT",FACE,{"disambiguationData":[TD([[makeQuery(id+"F23.imprint","IMPRINT",EDGE,{"derivedFrom":sQuery(id+"F23.wireOp",EDGE,"E84")}),1.0]])]});
            var Q27;
            Q27=makeQuery(id+"F23.imprint","IMPRINT",FACE,{"disambiguationData":[TD([[makeQuery(id+"F23.imprint","IMPRINT",EDGE,{"derivedFrom":sQuery(id+"F23.wireOp",EDGE,"E85")}),1.0]])]});
            var Q28;
            Q28=makeQuery(id+"F23.imprint","IMPRINT",FACE,{"disambiguationData":[TD([[makeQuery(id+"F23.imprint","IMPRINT",EDGE,{"derivedFrom":sQuery(id+"F23.wireOp",EDGE,"E86")}),1.0]])]});
            var Q29;
            Q29=makeQuery(id+"F23.imprint","IMPRINT",FACE,{"disambiguationData":[TD([[makeQuery(id+"F23.imprint","IMPRINT",EDGE,{"derivedFrom":sQuery(id+"F23.wireOp",EDGE,"E87")}),1.0]])]});
            var Q30;
            Q30=makeQuery(id+"F23.imprint","IMPRINT",FACE,{"disambiguationData":[TD([[makeQuery(id+"F23.imprint","IMPRINT",EDGE,{"derivedFrom":sQuery(id+"F23.wireOp",EDGE,"E88")}),1.0]])]});
            var Q31;
            Q31=makeQuery(id+"F23.imprint","IMPRINT",FACE,{"disambiguationData":[TD([[makeQuery(id+"F23.imprint","IMPRINT",EDGE,{"derivedFrom":sQuery(id+"F23.wireOp",EDGE,"E89")}),1.0]])]});
            var Q32;
            Q32=makeQuery(id+"F23.imprint","IMPRINT",FACE,{"disambiguationData":[TD([[makeQuery(id+"F23.imprint","IMPRINT",EDGE,{"derivedFrom":sQuery(id+"F23.wireOp",EDGE,"E91.MirrorC")}),-1.0]])]});
            var Q33;
            Q33=makeQuery(id+"F23.imprint","IMPRINT",FACE,{"disambiguationData":[TD([[makeQuery(id+"F23.imprint","IMPRINT",EDGE,{"derivedFrom":sQuery(id+"F23.wireOp",EDGE,"E92.MirrorC")}),-1.0]])]});
            var Q34;
            Q34=makeQuery(id+"F23.imprint","IMPRINT",FACE,{"disambiguationData":[TD([[makeQuery(id+"F23.imprint","IMPRINT",EDGE,{"derivedFrom":sQuery(id+"F23.wireOp",EDGE,"E93.MirrorC")}),-1.0]])]});
            var Q35;
            Q35=makeQuery(id+"F23.imprint","IMPRINT",FACE,{"disambiguationData":[TD([[makeQuery(id+"F23.imprint","IMPRINT",EDGE,{"derivedFrom":sQuery(id+"F23.wireOp",EDGE,"E94.MirrorC")}),-1.0]])]});
            var Q36;
            Q36=makeQuery(id+"F23.imprint","IMPRINT",FACE,{"disambiguationData":[TD([[makeQuery(id+"F23.imprint","IMPRINT",EDGE,{"derivedFrom":sQuery(id+"F23.wireOp",EDGE,"E96.MirrorC")}),-1.0]])]});
            var Q37;
            Q37=makeQuery(id+"F23.imprint","IMPRINT",FACE,{"disambiguationData":[TD([[makeQuery(id+"F23.imprint","IMPRINT",EDGE,{"derivedFrom":sQuery(id+"F23.wireOp",EDGE,"E95.MirrorC")}),-1.0]])]});
            var Q38;
            Q38=makeQuery(id+"F23.imprint","IMPRINT",FACE,{"disambiguationData":[TD([[makeQuery(id+"F23.imprint","IMPRINT",EDGE,{"derivedFrom":sQuery(id+"F23.wireOp",EDGE,"E97")}),1.0]])]});
            var Q39;
            Q39=makeQuery(id+"F23.imprint","IMPRINT",FACE,{"disambiguationData":[TD([[makeQuery(id+"F23.imprint","IMPRINT",EDGE,{"derivedFrom":sQuery(id+"F23.wireOp",EDGE,"E100.1.0.0")}),1.0]])]});
            var Q40;
            Q40=makeQuery(id+"F23.imprint","IMPRINT",FACE,{"disambiguationData":[TD([[makeQuery(id+"F23.imprint","IMPRINT",EDGE,{"derivedFrom":sQuery(id+"F23.wireOp",EDGE,"E100.2.0.0")}),1.0]])]});
            var Q41;
            Q41=makeQuery(id+"F23.imprint","IMPRINT",FACE,{"disambiguationData":[TD([[makeQuery(id+"F23.imprint","IMPRINT",EDGE,{"derivedFrom":sQuery(id+"F23.wireOp",EDGE,"E100.3.0.0")}),1.0]])]});
            var Q42;
            Q42=makeQuery(id+"F23.imprint","IMPRINT",FACE,{"disambiguationData":[TD([[makeQuery(id+"F23.imprint","IMPRINT",EDGE,{"derivedFrom":sQuery(id+"F23.wireOp",EDGE,"E100.4.0.0")}),1.0]])]});
            var Q43;
            Q43=makeQuery(id+"F23.imprint","IMPRINT",FACE,{"disambiguationData":[TD([[makeQuery(id+"F23.imprint","IMPRINT",EDGE,{"derivedFrom":sQuery(id+"F23.wireOp",EDGE,"E100.9.0.0")}),1.0]])]});
            var Q44;
            Q44=makeQuery(id+"F23.imprint","IMPRINT",FACE,{"disambiguationData":[TD([[makeQuery(id+"F23.imprint","IMPRINT",EDGE,{"derivedFrom":sQuery(id+"F23.wireOp",EDGE,"E101.2.0.0")}),1.0]])]});
            var Q45;
            Q45=makeQuery(id+"F23.imprint","IMPRINT",FACE,{"disambiguationData":[TD([[makeQuery(id+"F23.imprint","IMPRINT",EDGE,{"derivedFrom":sQuery(id+"F23.wireOp",EDGE,"E101.2.0.1")}),1.0]])]});
            var Q46;
            Q46=makeQuery(id+"F23.imprint","IMPRINT",FACE,{"disambiguationData":[TD([[makeQuery(id+"F23.imprint","IMPRINT",EDGE,{"derivedFrom":sQuery(id+"F23.wireOp",EDGE,"E101.2.0.2")}),1.0]])]});
            var Q47;
            Q47=makeQuery(id+"F23.imprint","IMPRINT",FACE,{"disambiguationData":[TD([[makeQuery(id+"F23.imprint","IMPRINT",EDGE,{"derivedFrom":sQuery(id+"F23.wireOp",EDGE,"E101.2.0.3")}),1.0]])]});
            var Q48;
            Q48=makeQuery(id+"F23.imprint","IMPRINT",FACE,{"disambiguationData":[TD([[makeQuery(id+"F23.imprint","IMPRINT",EDGE,{"derivedFrom":sQuery(id+"F23.wireOp",EDGE,"E101.2.0.4")}),1.0]])]});
            var Q49;
            Q49=makeQuery(id+"F23.imprint","IMPRINT",FACE,{"disambiguationData":[TD([[makeQuery(id+"F23.imprint","IMPRINT",EDGE,{"derivedFrom":sQuery(id+"F23.wireOp",EDGE,"E101.2.0.9")}),1.0]])]});
            var Q50;
            Q50=makeQuery(id+"F23.imprint","IMPRINT",FACE,{"disambiguationData":[TD([[makeQuery(id+"F23.imprint","IMPRINT",EDGE,{"derivedFrom":sQuery(id+"F23.wireOp",EDGE,"E101.2.0.10")}),1.0]])]});
            var Q51;
            Q51=makeQuery(id+"F23.imprint","IMPRINT",FACE,{"disambiguationData":[TD([[makeQuery(id+"F23.imprint","IMPRINT",EDGE,{"derivedFrom":sQuery(id+"F23.wireOp",EDGE,"E102")}),1.0]])]});
            var Q52;
            Q52=makeQuery(id+"F23.imprint","IMPRINT",FACE,{"disambiguationData":[TD([[makeQuery(id+"F23.imprint","IMPRINT",EDGE,{"derivedFrom":sQuery(id+"F23.wireOp",EDGE,"E103")}),1.0]])]});
            var Q53;
            Q53=makeQuery(id+"F23.imprint","IMPRINT",FACE,{"disambiguationData":[TD([[makeQuery(id+"F23.imprint","IMPRINT",EDGE,{"derivedFrom":sQuery(id+"F23.wireOp",EDGE,"E104")}),1.0]])]});
            var Q54;
            Q54=makeQuery(id+"F23.imprint","IMPRINT",FACE,{"disambiguationData":[TD([[makeQuery(id+"F23.imprint","IMPRINT",EDGE,{"derivedFrom":sQuery(id+"F23.wireOp",EDGE,"E106")}),1.0]])]});
            var Q55;
            Q55=makeQuery(id+"F23.imprint","IMPRINT",FACE,{"disambiguationData":[TD([[makeQuery(id+"F23.imprint","IMPRINT",EDGE,{"derivedFrom":sQuery(id+"F23.wireOp",EDGE,"E107")}),1.0]])]});
            var Q56;
            Q56=makeQuery(id+"F23.imprint","IMPRINT",FACE,{"disambiguationData":[TD([[makeQuery(id+"F23.imprint","IMPRINT",EDGE,{"derivedFrom":sQuery(id+"F23.wireOp",EDGE,"E108.MirrorC")}),-1.0]])]});
            var Q57;
            Q57=makeQuery(id+"F23.imprint","IMPRINT",FACE,{"disambiguationData":[TD([[makeQuery(id+"F23.imprint","IMPRINT",EDGE,{"derivedFrom":sQuery(id+"F23.wireOp",EDGE,"E109.MirrorC")}),-1.0]])]});
            var Q58;
            Q58=makeQuery(id+"F23.imprint","IMPRINT",FACE,{"disambiguationData":[TD([[makeQuery(id+"F23.imprint","IMPRINT",EDGE,{"derivedFrom":sQuery(id+"F23.wireOp",EDGE,"E110.MirrorC")}),-1.0]])]});
            var Q59;
            Q59=makeQuery(id+"F23.imprint","IMPRINT",FACE,{"disambiguationData":[TD([[makeQuery(id+"F23.imprint","IMPRINT",EDGE,{"derivedFrom":sQuery(id+"F23.wireOp",EDGE,"E83.3.0.6")}),1.0]])]});
            var Q60;
            Q60=makeQuery(id+"F23.imprint","IMPRINT",FACE,{"disambiguationData":[TD([[makeQuery(id+"F23.imprint","IMPRINT",EDGE,{"derivedFrom":sQuery(id+"F23.wireOp",EDGE,"E83.3.0.7")}),1.0]])]});
            var Q61;
            Q61=makeQuery(id+"F23.imprint","IMPRINT",FACE,{"disambiguationData":[TD([[makeQuery(id+"F23.imprint","IMPRINT",EDGE,{"derivedFrom":sQuery(id+"F23.wireOp",EDGE,"E83.3.0.8")}),1.0]])]});
            var Q62;
            Q62=makeQuery(id+"F23.imprint","IMPRINT",FACE,{"disambiguationData":[TD([[makeQuery(id+"F23.imprint","IMPRINT",EDGE,{"derivedFrom":sQuery(id+"F23.wireOp",EDGE,"E83.3.0.9")}),1.0]])]});
            var Q63;
            Q63=makeQuery(id+"F23.imprint","IMPRINT",FACE,{"disambiguationData":[TD([[makeQuery(id+"F23.imprint","IMPRINT",EDGE,{"derivedFrom":sQuery(id+"F23.wireOp",EDGE,"E83.3.0.10")}),1.0]])]});
            var Q64;
            Q64=makeQuery(id+"F23.imprint","IMPRINT",FACE,{"disambiguationData":[TD([[makeQuery(id+"F23.imprint","IMPRINT",EDGE,{"derivedFrom":sQuery(id+"F23.wireOp",EDGE,"E83.4.0.6")}),1.0]])]});
            var Q65;
            Q65=makeQuery(id+"F23.imprint","IMPRINT",FACE,{"disambiguationData":[TD([[makeQuery(id+"F23.imprint","IMPRINT",EDGE,{"derivedFrom":sQuery(id+"F23.wireOp",EDGE,"E83.4.0.7")}),1.0]])]});
            var Q66;
            Q66=makeQuery(id+"F23.imprint","IMPRINT",FACE,{"disambiguationData":[TD([[makeQuery(id+"F23.imprint","IMPRINT",EDGE,{"derivedFrom":sQuery(id+"F23.wireOp",EDGE,"E83.4.0.8")}),1.0]])]});
            var Q67;
            Q67=makeQuery(id+"F23.imprint","IMPRINT",FACE,{"disambiguationData":[TD([[makeQuery(id+"F23.imprint","IMPRINT",EDGE,{"derivedFrom":sQuery(id+"F23.wireOp",EDGE,"E83.4.0.9")}),1.0]])]});
            var Q68;
            Q68=makeQuery(id+"F23.imprint","IMPRINT",FACE,{"disambiguationData":[TD([[makeQuery(id+"F23.imprint","IMPRINT",EDGE,{"derivedFrom":sQuery(id+"F23.wireOp",EDGE,"E83.4.0.10")}),1.0]])]});
            var Q69;
            Q69=makeQuery(id+"F23.imprint","IMPRINT",FACE,{"disambiguationData":[TD([[makeQuery(id+"F23.imprint","IMPRINT",EDGE,{"derivedFrom":sQuery(id+"F23.wireOp",EDGE,"E101.1.0.0")}),1.0]])]});
            var Q70;
            Q70=makeQuery(id+"F23.imprint","IMPRINT",FACE,{"disambiguationData":[TD([[makeQuery(id+"F23.imprint","IMPRINT",EDGE,{"derivedFrom":sQuery(id+"F23.wireOp",EDGE,"E101.1.0.1")}),1.0]])]});
            var Q71;
            Q71=makeQuery(id+"F23.imprint","IMPRINT",FACE,{"disambiguationData":[TD([[makeQuery(id+"F23.imprint","IMPRINT",EDGE,{"derivedFrom":sQuery(id+"F23.wireOp",EDGE,"E101.1.0.2")}),1.0]])]});
            var Q72;
            Q72=makeQuery(id+"F23.imprint","IMPRINT",FACE,{"disambiguationData":[TD([[makeQuery(id+"F23.imprint","IMPRINT",EDGE,{"derivedFrom":sQuery(id+"F23.wireOp",EDGE,"E101.1.0.3")}),1.0]])]});
            var Q73;
            Q73=makeQuery(id+"F23.imprint","IMPRINT",FACE,{"disambiguationData":[TD([[makeQuery(id+"F23.imprint","IMPRINT",EDGE,{"derivedFrom":sQuery(id+"F23.wireOp",EDGE,"E101.1.0.4")}),1.0]])]});
            var Q74;
            Q74=makeQuery(id+"F23.imprint","IMPRINT",FACE,{"disambiguationData":[TD([[makeQuery(id+"F23.imprint","IMPRINT",EDGE,{"derivedFrom":sQuery(id+"F23.wireOp",EDGE,"E101.1.0.5")}),1.0]])]});
            var Q75;
            Q75=makeQuery(id+"F23.imprint","IMPRINT",FACE,{"disambiguationData":[TD([[makeQuery(id+"F23.imprint","IMPRINT",EDGE,{"derivedFrom":sQuery(id+"F23.wireOp",EDGE,"E101.1.0.6")}),1.0]])]});
            var Q76;
            Q76=makeQuery(id+"F23.imprint","IMPRINT",FACE,{"disambiguationData":[TD([[makeQuery(id+"F23.imprint","IMPRINT",EDGE,{"derivedFrom":sQuery(id+"F23.wireOp",EDGE,"E101.1.0.7")}),1.0]])]});
            var Q77;
            Q77=makeQuery(id+"F23.imprint","IMPRINT",FACE,{"disambiguationData":[TD([[makeQuery(id+"F23.imprint","IMPRINT",EDGE,{"derivedFrom":sQuery(id+"F23.wireOp",EDGE,"E101.1.0.8")}),1.0]])]});
            var Q78;
            Q78=makeQuery(id+"F23.imprint","IMPRINT",FACE,{"disambiguationData":[TD([[makeQuery(id+"F23.imprint","IMPRINT",EDGE,{"derivedFrom":sQuery(id+"F23.wireOp",EDGE,"E101.1.0.9")}),1.0]])]});
            var Q79;
            {var subQ0=sQuery(id+"F23.wireOp",EDGE,"E83.3.0.2");var subQ1=makeQuery(id+"F3.opExtrude","SWEPT_FACE",FACE,{"disambiguationData":[OSD([sQuery(id+"F2.wireOp",EDGE,"E44")])]});var subQ2=makeQuery(id+"F21.opBoolean","COPY",EDGE,{"derivedFrom":makeQuery(id+"F8.opFillet","BLEND_EDGE",EDGE,{"blendedFrom":[makeQuery(id+"F3.boolean.opBoolean","INTERSECT",EDGE,{"derivedFrom":[makeQuery(id+"F1.opExtrude","SWEPT_FACE",FACE,{"disambiguationData":[OSD([sQuery(id+"F0.wireOp",EDGE,"E15")])]}),subQ1]}),makeQuery(id+"F3.boolean.opBoolean","COPY",FACE,{"derivedFrom":subQ1})],"blendedInto":[makeQuery(id+"F3.boolean.opBoolean","COPY",FACE,{"derivedFrom":subQ1})]})});var subQ3=makeQuery(id+"F23.imprint","INTERSECT",VERTEX,{"disambiguationData":[OD(0.0)],"derivedFrom":[subQ2,subQ0]});Q79=makeQuery(id+"F23.imprint","IMPRINT",FACE,{"disambiguationData":[TD([[makeQuery(id+"F23.imprint","IMPRINT",EDGE,{"disambiguationData":[TD([[subQ3,1.0]])],"derivedFrom":subQ0}),1.0]])]});}
            var Q80;
            {var subQ0=sQuery(id+"F23.wireOp",EDGE,"E83.3.0.3");var subQ1=makeQuery(id+"F3.opExtrude","SWEPT_FACE",FACE,{"disambiguationData":[OSD([sQuery(id+"F2.wireOp",EDGE,"E44")])]});var subQ2=makeQuery(id+"F21.opBoolean","COPY",EDGE,{"derivedFrom":makeQuery(id+"F8.opFillet","BLEND_EDGE",EDGE,{"blendedFrom":[makeQuery(id+"F3.boolean.opBoolean","INTERSECT",EDGE,{"derivedFrom":[makeQuery(id+"F1.opExtrude","SWEPT_FACE",FACE,{"disambiguationData":[OSD([sQuery(id+"F0.wireOp",EDGE,"E15")])]}),subQ1]}),makeQuery(id+"F3.boolean.opBoolean","COPY",FACE,{"derivedFrom":subQ1})],"blendedInto":[makeQuery(id+"F3.boolean.opBoolean","COPY",FACE,{"derivedFrom":subQ1})]})});var subQ3=makeQuery(id+"F23.imprint","INTERSECT",VERTEX,{"disambiguationData":[OD(0.0)],"derivedFrom":[subQ2,subQ0]});Q80=makeQuery(id+"F23.imprint","IMPRINT",FACE,{"disambiguationData":[TD([[makeQuery(id+"F23.imprint","IMPRINT",EDGE,{"disambiguationData":[TD([[subQ3,1.0]])],"derivedFrom":subQ0}),1.0]])]});}
            var Q81;
            {var subQ0=sQuery(id+"F23.wireOp",EDGE,"E83.3.0.4");var subQ1=makeQuery(id+"F3.opExtrude","SWEPT_FACE",FACE,{"disambiguationData":[OSD([sQuery(id+"F2.wireOp",EDGE,"E44")])]});var subQ2=makeQuery(id+"F21.opBoolean","COPY",EDGE,{"derivedFrom":makeQuery(id+"F8.opFillet","BLEND_EDGE",EDGE,{"blendedFrom":[makeQuery(id+"F3.boolean.opBoolean","INTERSECT",EDGE,{"derivedFrom":[makeQuery(id+"F1.opExtrude","SWEPT_FACE",FACE,{"disambiguationData":[OSD([sQuery(id+"F0.wireOp",EDGE,"E15")])]}),subQ1]}),makeQuery(id+"F3.boolean.opBoolean","COPY",FACE,{"derivedFrom":subQ1})],"blendedInto":[makeQuery(id+"F3.boolean.opBoolean","COPY",FACE,{"derivedFrom":subQ1})]})});var subQ3=makeQuery(id+"F23.imprint","INTERSECT",VERTEX,{"disambiguationData":[OD(0.0)],"derivedFrom":[subQ2,subQ0]});Q81=makeQuery(id+"F23.imprint","IMPRINT",FACE,{"disambiguationData":[TD([[makeQuery(id+"F23.imprint","IMPRINT",EDGE,{"disambiguationData":[TD([[subQ3,1.0]])],"derivedFrom":subQ0}),1.0]])]});}
            var Q82;
            {var subQ0=sQuery(id+"F23.wireOp",EDGE,"E83.3.0.5");var subQ1=makeQuery(id+"F3.opExtrude","SWEPT_FACE",FACE,{"disambiguationData":[OSD([sQuery(id+"F2.wireOp",EDGE,"E44")])]});var subQ2=makeQuery(id+"F21.opBoolean","COPY",EDGE,{"derivedFrom":makeQuery(id+"F8.opFillet","BLEND_EDGE",EDGE,{"blendedFrom":[makeQuery(id+"F3.boolean.opBoolean","INTERSECT",EDGE,{"derivedFrom":[makeQuery(id+"F1.opExtrude","SWEPT_FACE",FACE,{"disambiguationData":[OSD([sQuery(id+"F0.wireOp",EDGE,"E15")])]}),subQ1]}),makeQuery(id+"F3.boolean.opBoolean","COPY",FACE,{"derivedFrom":subQ1})],"blendedInto":[makeQuery(id+"F3.boolean.opBoolean","COPY",FACE,{"derivedFrom":subQ1})]})});var subQ3=makeQuery(id+"F23.imprint","INTERSECT",VERTEX,{"disambiguationData":[OD(0.0)],"derivedFrom":[subQ2,subQ0]});Q82=makeQuery(id+"F23.imprint","IMPRINT",FACE,{"disambiguationData":[TD([[makeQuery(id+"F23.imprint","IMPRINT",EDGE,{"disambiguationData":[TD([[subQ3,-1.0]])],"derivedFrom":subQ0}),1.0]])]});}
            var Q83;
            {var subQ0=sQuery(id+"F23.wireOp",EDGE,"E83.3.0.11");var subQ1=sQuery(id+"F2.wireOp",EDGE,"E44");var subQ2=makeQuery(id+"F21.opBoolean","COPY",EDGE,{"derivedFrom":makeQuery(id+"F8.opFillet","BLEND_EDGE",EDGE,{"disambiguationData":[OD(1.0)],"blendedFrom":[makeQuery(id+"F4.opFillet","BLEND_EDGE",EDGE,{"blendedFrom":[makeQuery(id+"F3.boolean.opBoolean","COPY",EDGE,{"derivedFrom":makeQuery(id+"F3.opExtrude","SWEPT_EDGE",EDGE,{"disambiguationData":[OSD([sQuery(id+"F0.wireOp",EDGE,"E19.MirrorCS"),sQuery(id+"F0.wireOp",EDGE,"E20.MirrorCS"),subQ1,sQuery(id+"F2.wireOp",EDGE,"E45")])]})}),makeQuery(id+"F1.opExtrude","SWEPT_FACE",FACE,{"disambiguationData":[OSD([sQuery(id+"F0.wireOp",EDGE,"E13")])]})],"blendedInto":[makeQuery(id+"F1.opExtrude","SWEPT_FACE",FACE,{"disambiguationData":[OSD([sQuery(id+"F0.wireOp",EDGE,"E13")])]})]}),makeQuery(id+"F3.boolean.opBoolean","COPY",FACE,{"derivedFrom":makeQuery(id+"F3.opExtrude","SWEPT_FACE",FACE,{"disambiguationData":[OSD([subQ1])]})})],"blendedInto":[makeQuery(id+"F3.boolean.opBoolean","COPY",FACE,{"derivedFrom":makeQuery(id+"F3.opExtrude","SWEPT_FACE",FACE,{"disambiguationData":[OSD([subQ1])]})})]})});var subQ3=makeQuery(id+"F23.imprint","INTERSECT",VERTEX,{"disambiguationData":[OD(0.0)],"derivedFrom":[subQ2,subQ0]});Q83=makeQuery(id+"F23.imprint","IMPRINT",FACE,{"disambiguationData":[TD([[makeQuery(id+"F23.imprint","IMPRINT",EDGE,{"disambiguationData":[TD([[subQ3,1.0]])],"derivedFrom":subQ0}),1.0]])]});}
            var Q84;
            {var subQ0=sQuery(id+"F23.wireOp",EDGE,"E83.4.0.2");var subQ1=makeQuery(id+"F3.opExtrude","SWEPT_FACE",FACE,{"disambiguationData":[OSD([sQuery(id+"F2.wireOp",EDGE,"E44")])]});var subQ2=makeQuery(id+"F21.opBoolean","COPY",EDGE,{"derivedFrom":makeQuery(id+"F8.opFillet","BLEND_EDGE",EDGE,{"blendedFrom":[makeQuery(id+"F3.boolean.opBoolean","INTERSECT",EDGE,{"derivedFrom":[makeQuery(id+"F1.opExtrude","SWEPT_FACE",FACE,{"disambiguationData":[OSD([sQuery(id+"F0.wireOp",EDGE,"E18.MirrorCS")])]}),subQ1]}),makeQuery(id+"F3.boolean.opBoolean","COPY",FACE,{"derivedFrom":subQ1})],"blendedInto":[makeQuery(id+"F3.boolean.opBoolean","COPY",FACE,{"derivedFrom":subQ1})]})});var subQ3=makeQuery(id+"F23.imprint","INTERSECT",VERTEX,{"disambiguationData":[OD(0.0)],"derivedFrom":[subQ2,subQ0]});Q84=makeQuery(id+"F23.imprint","IMPRINT",FACE,{"disambiguationData":[TD([[makeQuery(id+"F23.imprint","IMPRINT",EDGE,{"disambiguationData":[TD([[subQ3,-1.0]])],"derivedFrom":subQ0}),1.0]])]});}
            var Q85;
            {var subQ0=sQuery(id+"F23.wireOp",EDGE,"E83.4.0.3");var subQ1=makeQuery(id+"F3.opExtrude","SWEPT_FACE",FACE,{"disambiguationData":[OSD([sQuery(id+"F2.wireOp",EDGE,"E44")])]});var subQ2=makeQuery(id+"F21.opBoolean","COPY",EDGE,{"derivedFrom":makeQuery(id+"F8.opFillet","BLEND_EDGE",EDGE,{"blendedFrom":[makeQuery(id+"F3.boolean.opBoolean","INTERSECT",EDGE,{"derivedFrom":[makeQuery(id+"F1.opExtrude","SWEPT_FACE",FACE,{"disambiguationData":[OSD([sQuery(id+"F0.wireOp",EDGE,"E18.MirrorCS")])]}),subQ1]}),makeQuery(id+"F3.boolean.opBoolean","COPY",FACE,{"derivedFrom":subQ1})],"blendedInto":[makeQuery(id+"F3.boolean.opBoolean","COPY",FACE,{"derivedFrom":subQ1})]})});var subQ3=makeQuery(id+"F23.imprint","INTERSECT",VERTEX,{"disambiguationData":[OD(0.0)],"derivedFrom":[subQ2,subQ0]});Q85=makeQuery(id+"F23.imprint","IMPRINT",FACE,{"disambiguationData":[TD([[makeQuery(id+"F23.imprint","IMPRINT",EDGE,{"disambiguationData":[TD([[subQ3,-1.0]])],"derivedFrom":subQ0}),1.0]])]});}
            var Q86;
            {var subQ0=sQuery(id+"F23.wireOp",EDGE,"E83.4.0.4");var subQ1=makeQuery(id+"F3.opExtrude","SWEPT_FACE",FACE,{"disambiguationData":[OSD([sQuery(id+"F2.wireOp",EDGE,"E44")])]});var subQ2=makeQuery(id+"F21.opBoolean","COPY",EDGE,{"derivedFrom":makeQuery(id+"F8.opFillet","BLEND_EDGE",EDGE,{"blendedFrom":[makeQuery(id+"F3.boolean.opBoolean","INTERSECT",EDGE,{"derivedFrom":[makeQuery(id+"F1.opExtrude","SWEPT_FACE",FACE,{"disambiguationData":[OSD([sQuery(id+"F0.wireOp",EDGE,"E18.MirrorCS")])]}),subQ1]}),makeQuery(id+"F3.boolean.opBoolean","COPY",FACE,{"derivedFrom":subQ1})],"blendedInto":[makeQuery(id+"F3.boolean.opBoolean","COPY",FACE,{"derivedFrom":subQ1})]})});var subQ3=makeQuery(id+"F23.imprint","INTERSECT",VERTEX,{"disambiguationData":[OD(0.0)],"derivedFrom":[subQ2,subQ0]});Q86=makeQuery(id+"F23.imprint","IMPRINT",FACE,{"disambiguationData":[TD([[makeQuery(id+"F23.imprint","IMPRINT",EDGE,{"disambiguationData":[TD([[subQ3,-1.0]])],"derivedFrom":subQ0}),1.0]])]});}
            var Q87;
            {var subQ0=sQuery(id+"F23.wireOp",EDGE,"E83.4.0.5");var subQ1=makeQuery(id+"F3.opExtrude","SWEPT_FACE",FACE,{"disambiguationData":[OSD([sQuery(id+"F2.wireOp",EDGE,"E44")])]});var subQ2=makeQuery(id+"F21.opBoolean","COPY",EDGE,{"derivedFrom":makeQuery(id+"F8.opFillet","BLEND_EDGE",EDGE,{"blendedFrom":[makeQuery(id+"F3.boolean.opBoolean","INTERSECT",EDGE,{"derivedFrom":[makeQuery(id+"F1.opExtrude","SWEPT_FACE",FACE,{"disambiguationData":[OSD([sQuery(id+"F0.wireOp",EDGE,"E18.MirrorCS")])]}),subQ1]}),makeQuery(id+"F3.boolean.opBoolean","COPY",FACE,{"derivedFrom":subQ1})],"blendedInto":[makeQuery(id+"F3.boolean.opBoolean","COPY",FACE,{"derivedFrom":subQ1})]})});var subQ3=makeQuery(id+"F23.imprint","INTERSECT",VERTEX,{"disambiguationData":[OD(0.0)],"derivedFrom":[subQ2,subQ0]});Q87=makeQuery(id+"F23.imprint","IMPRINT",FACE,{"disambiguationData":[TD([[makeQuery(id+"F23.imprint","IMPRINT",EDGE,{"disambiguationData":[TD([[subQ3,1.0]])],"derivedFrom":subQ0}),1.0]])]});}
            var Q88;
            {var subQ0=sQuery(id+"F23.wireOp",EDGE,"E83.4.0.11");var subQ1=sQuery(id+"F2.wireOp",EDGE,"E44");var subQ2=sQuery(id+"F0.wireOp",EDGE,"E20.MirrorCS");var subQ3=makeQuery(id+"F21.opBoolean","COPY",EDGE,{"derivedFrom":makeQuery(id+"F8.opFillet","BLEND_EDGE",EDGE,{"disambiguationData":[OD(0.0)],"blendedFrom":[makeQuery(id+"F4.opFillet","BLEND_EDGE",EDGE,{"blendedFrom":[makeQuery(id+"F3.boolean.opBoolean","COPY",EDGE,{"derivedFrom":makeQuery(id+"F3.opExtrude","SWEPT_EDGE",EDGE,{"disambiguationData":[OSD([sQuery(id+"F0.wireOp",EDGE,"E19.MirrorCS"),subQ2,subQ1,sQuery(id+"F2.wireOp",EDGE,"E45")])]})}),makeQuery(id+"F1.opExtrude","SWEPT_FACE",FACE,{"disambiguationData":[OSD([subQ2])]})],"blendedInto":[makeQuery(id+"F1.opExtrude","SWEPT_FACE",FACE,{"disambiguationData":[OSD([subQ2])]})]}),makeQuery(id+"F3.boolean.opBoolean","COPY",FACE,{"derivedFrom":makeQuery(id+"F3.opExtrude","SWEPT_FACE",FACE,{"disambiguationData":[OSD([subQ1])]})})],"blendedInto":[makeQuery(id+"F3.boolean.opBoolean","COPY",FACE,{"derivedFrom":makeQuery(id+"F3.opExtrude","SWEPT_FACE",FACE,{"disambiguationData":[OSD([subQ1])]})})]})});var subQ4=makeQuery(id+"F23.imprint","INTERSECT",VERTEX,{"disambiguationData":[OD(0.0)],"derivedFrom":[subQ3,subQ0]});Q88=makeQuery(id+"F23.imprint","IMPRINT",FACE,{"disambiguationData":[TD([[makeQuery(id+"F23.imprint","IMPRINT",EDGE,{"disambiguationData":[TD([[subQ4,-1.0]])],"derivedFrom":subQ0}),1.0]])]});}
            var Q89;
            {var subQ0=sQuery(id+"F23.wireOp",EDGE,"E100.5.0.0");var subQ1=makeQuery(id+"F3.opExtrude","SWEPT_FACE",FACE,{"disambiguationData":[OSD([sQuery(id+"F2.wireOp",EDGE,"E44")])]});var subQ2=makeQuery(id+"F21.opBoolean","COPY",EDGE,{"derivedFrom":makeQuery(id+"F8.opFillet","BLEND_EDGE",EDGE,{"blendedFrom":[makeQuery(id+"F3.boolean.opBoolean","INTERSECT",EDGE,{"derivedFrom":[makeQuery(id+"F1.opExtrude","SWEPT_FACE",FACE,{"disambiguationData":[OSD([sQuery(id+"F0.wireOp",EDGE,"E15")])]}),subQ1]}),makeQuery(id+"F3.boolean.opBoolean","COPY",FACE,{"derivedFrom":subQ1})],"blendedInto":[makeQuery(id+"F3.boolean.opBoolean","COPY",FACE,{"derivedFrom":subQ1})]})});var subQ3=makeQuery(id+"F23.imprint","INTERSECT",VERTEX,{"disambiguationData":[OD(0.0)],"derivedFrom":[subQ2,subQ0]});Q89=makeQuery(id+"F23.imprint","IMPRINT",FACE,{"disambiguationData":[TD([[makeQuery(id+"F23.imprint","IMPRINT",EDGE,{"disambiguationData":[TD([[subQ3,-1.0]])],"derivedFrom":subQ0}),1.0]])]});}
            var Q90;
            {var subQ0=sQuery(id+"F23.wireOp",EDGE,"E100.6.0.0");var subQ1=makeQuery(id+"F3.opExtrude","SWEPT_FACE",FACE,{"disambiguationData":[OSD([sQuery(id+"F2.wireOp",EDGE,"E44")])]});var subQ2=makeQuery(id+"F21.opBoolean","COPY",EDGE,{"derivedFrom":makeQuery(id+"F8.opFillet","BLEND_EDGE",EDGE,{"blendedFrom":[makeQuery(id+"F3.boolean.opBoolean","INTERSECT",EDGE,{"derivedFrom":[makeQuery(id+"F1.opExtrude","SWEPT_FACE",FACE,{"disambiguationData":[OSD([sQuery(id+"F0.wireOp",EDGE,"E15")])]}),subQ1]}),makeQuery(id+"F3.boolean.opBoolean","COPY",FACE,{"derivedFrom":subQ1})],"blendedInto":[makeQuery(id+"F3.boolean.opBoolean","COPY",FACE,{"derivedFrom":subQ1})]})});var subQ3=makeQuery(id+"F23.imprint","INTERSECT",VERTEX,{"disambiguationData":[OD(0.0)],"derivedFrom":[subQ2,subQ0]});Q90=makeQuery(id+"F23.imprint","IMPRINT",FACE,{"disambiguationData":[TD([[makeQuery(id+"F23.imprint","IMPRINT",EDGE,{"disambiguationData":[TD([[subQ3,-1.0]])],"derivedFrom":subQ0}),1.0]])]});}
            var Q91;
            {var subQ0=sQuery(id+"F23.wireOp",EDGE,"E100.7.0.0");var subQ1=makeQuery(id+"F3.opExtrude","SWEPT_FACE",FACE,{"disambiguationData":[OSD([sQuery(id+"F2.wireOp",EDGE,"E44")])]});var subQ2=makeQuery(id+"F21.opBoolean","COPY",EDGE,{"derivedFrom":makeQuery(id+"F8.opFillet","BLEND_EDGE",EDGE,{"blendedFrom":[makeQuery(id+"F3.boolean.opBoolean","INTERSECT",EDGE,{"derivedFrom":[makeQuery(id+"F1.opExtrude","SWEPT_FACE",FACE,{"disambiguationData":[OSD([sQuery(id+"F0.wireOp",EDGE,"E15")])]}),subQ1]}),makeQuery(id+"F3.boolean.opBoolean","COPY",FACE,{"derivedFrom":subQ1})],"blendedInto":[makeQuery(id+"F3.boolean.opBoolean","COPY",FACE,{"derivedFrom":subQ1})]})});var subQ3=makeQuery(id+"F23.imprint","INTERSECT",VERTEX,{"disambiguationData":[OD(0.0)],"derivedFrom":[subQ2,subQ0]});Q91=makeQuery(id+"F23.imprint","IMPRINT",FACE,{"disambiguationData":[TD([[makeQuery(id+"F23.imprint","IMPRINT",EDGE,{"disambiguationData":[TD([[subQ3,-1.0]])],"derivedFrom":subQ0}),1.0]])]});}
            var Q92;
            {var subQ0=sQuery(id+"F23.wireOp",EDGE,"E100.8.0.0");var subQ1=makeQuery(id+"F3.boolean.opBoolean","COPY",FACE,{"derivedFrom":makeQuery(id+"F3.opExtrude","SWEPT_FACE",FACE,{"disambiguationData":[OSD([sQuery(id+"F2.wireOp",EDGE,"E44")])]})});var subQ2=makeQuery(id+"F21.opBoolean","COPY",EDGE,{"derivedFrom":makeQuery(id+"F8.opFillet","BLEND_EDGE",EDGE,{"disambiguationData":[OD(1.0)],"blendedFrom":[makeQuery(id+"F7.opFillet","BLEND_EDGE",EDGE,{"blendedFrom":[makeQuery(id+"F1.opExtrude","SWEPT_EDGE",EDGE,{"disambiguationData":[OSD([sQuery(id+"F0.wireOp",EDGE,"E14"),sQuery(id+"F0.wireOp",EDGE,"E15")])]}),subQ1],"blendedInto":[subQ1]}),subQ1],"blendedInto":[subQ1]})});var subQ3=makeQuery(id+"F23.imprint","INTERSECT",VERTEX,{"disambiguationData":[OD(0.0)],"derivedFrom":[subQ2,subQ0]});Q92=makeQuery(id+"F23.imprint","IMPRINT",FACE,{"disambiguationData":[TD([[makeQuery(id+"F23.imprint","IMPRINT",EDGE,{"disambiguationData":[TD([[subQ3,1.0]])],"derivedFrom":subQ0}),1.0]])]});}
            var Q93;
            {var subQ0=sQuery(id+"F23.wireOp",EDGE,"E101.2.0.5");var subQ1=makeQuery(id+"F3.opExtrude","SWEPT_FACE",FACE,{"disambiguationData":[OSD([sQuery(id+"F2.wireOp",EDGE,"E44")])]});var subQ2=makeQuery(id+"F21.opBoolean","COPY",EDGE,{"derivedFrom":makeQuery(id+"F8.opFillet","BLEND_EDGE",EDGE,{"blendedFrom":[makeQuery(id+"F3.boolean.opBoolean","INTERSECT",EDGE,{"derivedFrom":[makeQuery(id+"F1.opExtrude","SWEPT_FACE",FACE,{"disambiguationData":[OSD([sQuery(id+"F0.wireOp",EDGE,"E18.MirrorCS")])]}),subQ1]}),makeQuery(id+"F3.boolean.opBoolean","COPY",FACE,{"derivedFrom":subQ1})],"blendedInto":[makeQuery(id+"F3.boolean.opBoolean","COPY",FACE,{"derivedFrom":subQ1})]})});var subQ3=makeQuery(id+"F23.imprint","INTERSECT",VERTEX,{"disambiguationData":[OD(0.0)],"derivedFrom":[subQ2,subQ0]});Q93=makeQuery(id+"F23.imprint","IMPRINT",FACE,{"disambiguationData":[TD([[makeQuery(id+"F23.imprint","IMPRINT",EDGE,{"disambiguationData":[TD([[subQ3,1.0]])],"derivedFrom":subQ0}),1.0]])]});}
            var Q94;
            {var subQ0=sQuery(id+"F23.wireOp",EDGE,"E101.2.0.6");var subQ1=makeQuery(id+"F3.opExtrude","SWEPT_FACE",FACE,{"disambiguationData":[OSD([sQuery(id+"F2.wireOp",EDGE,"E44")])]});var subQ2=makeQuery(id+"F21.opBoolean","COPY",EDGE,{"derivedFrom":makeQuery(id+"F8.opFillet","BLEND_EDGE",EDGE,{"blendedFrom":[makeQuery(id+"F3.boolean.opBoolean","INTERSECT",EDGE,{"derivedFrom":[makeQuery(id+"F1.opExtrude","SWEPT_FACE",FACE,{"disambiguationData":[OSD([sQuery(id+"F0.wireOp",EDGE,"E18.MirrorCS")])]}),subQ1]}),makeQuery(id+"F3.boolean.opBoolean","COPY",FACE,{"derivedFrom":subQ1})],"blendedInto":[makeQuery(id+"F3.boolean.opBoolean","COPY",FACE,{"derivedFrom":subQ1})]})});var subQ3=makeQuery(id+"F23.imprint","INTERSECT",VERTEX,{"disambiguationData":[OD(0.0)],"derivedFrom":[subQ2,subQ0]});Q94=makeQuery(id+"F23.imprint","IMPRINT",FACE,{"disambiguationData":[TD([[makeQuery(id+"F23.imprint","IMPRINT",EDGE,{"disambiguationData":[TD([[subQ3,1.0]])],"derivedFrom":subQ0}),1.0]])]});}
            var Q95;
            {var subQ0=sQuery(id+"F23.wireOp",EDGE,"E101.2.0.7");var subQ1=makeQuery(id+"F3.opExtrude","SWEPT_FACE",FACE,{"disambiguationData":[OSD([sQuery(id+"F2.wireOp",EDGE,"E44")])]});var subQ2=makeQuery(id+"F21.opBoolean","COPY",EDGE,{"derivedFrom":makeQuery(id+"F8.opFillet","BLEND_EDGE",EDGE,{"blendedFrom":[makeQuery(id+"F3.boolean.opBoolean","INTERSECT",EDGE,{"derivedFrom":[makeQuery(id+"F1.opExtrude","SWEPT_FACE",FACE,{"disambiguationData":[OSD([sQuery(id+"F0.wireOp",EDGE,"E18.MirrorCS")])]}),subQ1]}),makeQuery(id+"F3.boolean.opBoolean","COPY",FACE,{"derivedFrom":subQ1})],"blendedInto":[makeQuery(id+"F3.boolean.opBoolean","COPY",FACE,{"derivedFrom":subQ1})]})});var subQ3=makeQuery(id+"F23.imprint","INTERSECT",VERTEX,{"disambiguationData":[OD(0.0)],"derivedFrom":[subQ2,subQ0]});Q95=makeQuery(id+"F23.imprint","IMPRINT",FACE,{"disambiguationData":[TD([[makeQuery(id+"F23.imprint","IMPRINT",EDGE,{"disambiguationData":[TD([[subQ3,1.0]])],"derivedFrom":subQ0}),1.0]])]});}
            var Q96;
            {var subQ0=sQuery(id+"F23.wireOp",EDGE,"E101.2.0.8");var subQ1=makeQuery(id+"F3.boolean.opBoolean","COPY",FACE,{"derivedFrom":makeQuery(id+"F3.opExtrude","SWEPT_FACE",FACE,{"disambiguationData":[OSD([sQuery(id+"F2.wireOp",EDGE,"E44")])]})});var subQ2=makeQuery(id+"F21.opBoolean","COPY",EDGE,{"derivedFrom":makeQuery(id+"F8.opFillet","BLEND_EDGE",EDGE,{"disambiguationData":[OD(0.0)],"blendedFrom":[makeQuery(id+"F7.opFillet","BLEND_EDGE",EDGE,{"blendedFrom":[makeQuery(id+"F1.opExtrude","SWEPT_EDGE",EDGE,{"disambiguationData":[OSD([sQuery(id+"F0.wireOp",EDGE,"E18.MirrorCS"),sQuery(id+"F0.wireOp",EDGE,"E19.MirrorCS")])]}),subQ1],"blendedInto":[subQ1]}),subQ1],"blendedInto":[subQ1]})});var subQ3=makeQuery(id+"F23.imprint","INTERSECT",VERTEX,{"disambiguationData":[OD(0.0)],"derivedFrom":[subQ2,subQ0]});Q96=makeQuery(id+"F23.imprint","IMPRINT",FACE,{"disambiguationData":[TD([[makeQuery(id+"F23.imprint","IMPRINT",EDGE,{"disambiguationData":[TD([[subQ3,-1.0]])],"derivedFrom":subQ0}),1.0]])]});}
            var Q97;
            {var subQ0=sQuery(id+"F23.wireOp",EDGE,"E105");var subQ1=makeQuery(id+"F3.opExtrude","SWEPT_FACE",FACE,{"disambiguationData":[OSD([sQuery(id+"F2.wireOp",EDGE,"E44")])]});var subQ2=makeQuery(id+"F21.opBoolean","COPY",EDGE,{"derivedFrom":makeQuery(id+"F8.opFillet","BLEND_EDGE",EDGE,{"blendedFrom":[makeQuery(id+"F3.boolean.opBoolean","INTERSECT",EDGE,{"derivedFrom":[makeQuery(id+"F1.opExtrude","SWEPT_FACE",FACE,{"disambiguationData":[OSD([sQuery(id+"F0.wireOp",EDGE,"E15")])]}),subQ1]}),makeQuery(id+"F3.boolean.opBoolean","COPY",FACE,{"derivedFrom":subQ1})],"blendedInto":[makeQuery(id+"F3.boolean.opBoolean","COPY",FACE,{"derivedFrom":subQ1})]})});var subQ3=makeQuery(id+"F23.imprint","INTERSECT",VERTEX,{"disambiguationData":[OD(0.0)],"derivedFrom":[subQ2,subQ0]});Q97=makeQuery(id+"F23.imprint","IMPRINT",FACE,{"disambiguationData":[TD([[makeQuery(id+"F23.imprint","IMPRINT",EDGE,{"disambiguationData":[TD([[subQ3,1.0]])],"derivedFrom":subQ0}),1.0]])]});}
            var Q98;
            {var subQ0=sQuery(id+"F23.wireOp",EDGE,"E105");var subQ1=makeQuery(id+"F3.opExtrude","SWEPT_FACE",FACE,{"disambiguationData":[OSD([sQuery(id+"F2.wireOp",EDGE,"E44")])]});var subQ2=makeQuery(id+"F21.opBoolean","COPY",EDGE,{"derivedFrom":makeQuery(id+"F8.opFillet","BLEND_EDGE",EDGE,{"blendedFrom":[makeQuery(id+"F3.boolean.opBoolean","INTERSECT",EDGE,{"derivedFrom":[makeQuery(id+"F1.opExtrude","SWEPT_FACE",FACE,{"disambiguationData":[OSD([sQuery(id+"F0.wireOp",EDGE,"E18.MirrorCS")])]}),subQ1]}),makeQuery(id+"F3.boolean.opBoolean","COPY",FACE,{"derivedFrom":subQ1})],"blendedInto":[makeQuery(id+"F3.boolean.opBoolean","COPY",FACE,{"derivedFrom":subQ1})]})});var subQ3=makeQuery(id+"F23.imprint","INTERSECT",VERTEX,{"disambiguationData":[OD(0.0)],"derivedFrom":[subQ2,subQ0]});Q98=makeQuery(id+"F23.imprint","IMPRINT",FACE,{"disambiguationData":[TD([[makeQuery(id+"F23.imprint","IMPRINT",EDGE,{"disambiguationData":[TD([[subQ3,-1.0]])],"derivedFrom":subQ0}),1.0]])]});}
            var Q99;
            {var subQ0=sQuery(id+"F23.wireOp",EDGE,"E83.3.0.2");var subQ1=makeQuery(id+"F3.opExtrude","SWEPT_FACE",FACE,{"disambiguationData":[OSD([sQuery(id+"F2.wireOp",EDGE,"E44")])]});var subQ2=makeQuery(id+"F21.opBoolean","COPY",EDGE,{"derivedFrom":makeQuery(id+"F8.opFillet","BLEND_EDGE",EDGE,{"blendedFrom":[makeQuery(id+"F3.boolean.opBoolean","INTERSECT",EDGE,{"derivedFrom":[makeQuery(id+"F1.opExtrude","SWEPT_FACE",FACE,{"disambiguationData":[OSD([sQuery(id+"F0.wireOp",EDGE,"E15")])]}),subQ1]}),makeQuery(id+"F3.boolean.opBoolean","COPY",FACE,{"derivedFrom":subQ1})],"blendedInto":[makeQuery(id+"F3.boolean.opBoolean","COPY",FACE,{"derivedFrom":subQ1})]})});var subQ3=makeQuery(id+"F23.imprint","INTERSECT",VERTEX,{"disambiguationData":[OD(0.0)],"derivedFrom":[subQ2,subQ0]});Q99=makeQuery(id+"F23.imprint","IMPRINT",FACE,{"disambiguationData":[TD([[makeQuery(id+"F23.imprint","IMPRINT",EDGE,{"disambiguationData":[TD([[subQ3,-1.0]])],"derivedFrom":subQ0}),1.0]])]});}
            var Q100;
            {var subQ0=sQuery(id+"F23.wireOp",EDGE,"E83.3.0.3");var subQ1=makeQuery(id+"F3.opExtrude","SWEPT_FACE",FACE,{"disambiguationData":[OSD([sQuery(id+"F2.wireOp",EDGE,"E44")])]});var subQ2=makeQuery(id+"F21.opBoolean","COPY",EDGE,{"derivedFrom":makeQuery(id+"F8.opFillet","BLEND_EDGE",EDGE,{"blendedFrom":[makeQuery(id+"F3.boolean.opBoolean","INTERSECT",EDGE,{"derivedFrom":[makeQuery(id+"F1.opExtrude","SWEPT_FACE",FACE,{"disambiguationData":[OSD([sQuery(id+"F0.wireOp",EDGE,"E15")])]}),subQ1]}),makeQuery(id+"F3.boolean.opBoolean","COPY",FACE,{"derivedFrom":subQ1})],"blendedInto":[makeQuery(id+"F3.boolean.opBoolean","COPY",FACE,{"derivedFrom":subQ1})]})});var subQ3=makeQuery(id+"F23.imprint","INTERSECT",VERTEX,{"disambiguationData":[OD(0.0)],"derivedFrom":[subQ2,subQ0]});Q100=makeQuery(id+"F23.imprint","IMPRINT",FACE,{"disambiguationData":[TD([[makeQuery(id+"F23.imprint","IMPRINT",EDGE,{"disambiguationData":[TD([[subQ3,-1.0]])],"derivedFrom":subQ0}),1.0]])]});}
            var Q101;
            {var subQ0=sQuery(id+"F23.wireOp",EDGE,"E83.3.0.4");var subQ1=makeQuery(id+"F3.opExtrude","SWEPT_FACE",FACE,{"disambiguationData":[OSD([sQuery(id+"F2.wireOp",EDGE,"E44")])]});var subQ2=makeQuery(id+"F21.opBoolean","COPY",EDGE,{"derivedFrom":makeQuery(id+"F8.opFillet","BLEND_EDGE",EDGE,{"blendedFrom":[makeQuery(id+"F3.boolean.opBoolean","INTERSECT",EDGE,{"derivedFrom":[makeQuery(id+"F1.opExtrude","SWEPT_FACE",FACE,{"disambiguationData":[OSD([sQuery(id+"F0.wireOp",EDGE,"E15")])]}),subQ1]}),makeQuery(id+"F3.boolean.opBoolean","COPY",FACE,{"derivedFrom":subQ1})],"blendedInto":[makeQuery(id+"F3.boolean.opBoolean","COPY",FACE,{"derivedFrom":subQ1})]})});var subQ3=makeQuery(id+"F23.imprint","INTERSECT",VERTEX,{"disambiguationData":[OD(0.0)],"derivedFrom":[subQ2,subQ0]});Q101=makeQuery(id+"F23.imprint","IMPRINT",FACE,{"disambiguationData":[TD([[makeQuery(id+"F23.imprint","IMPRINT",EDGE,{"disambiguationData":[TD([[subQ3,-1.0]])],"derivedFrom":subQ0}),1.0]])]});}
            var Q102;
            {var subQ0=sQuery(id+"F23.wireOp",EDGE,"E83.3.0.5");var subQ1=makeQuery(id+"F3.opExtrude","SWEPT_FACE",FACE,{"disambiguationData":[OSD([sQuery(id+"F2.wireOp",EDGE,"E44")])]});var subQ2=makeQuery(id+"F21.opBoolean","COPY",EDGE,{"derivedFrom":makeQuery(id+"F8.opFillet","BLEND_EDGE",EDGE,{"blendedFrom":[makeQuery(id+"F3.boolean.opBoolean","INTERSECT",EDGE,{"derivedFrom":[makeQuery(id+"F1.opExtrude","SWEPT_FACE",FACE,{"disambiguationData":[OSD([sQuery(id+"F0.wireOp",EDGE,"E15")])]}),subQ1]}),makeQuery(id+"F3.boolean.opBoolean","COPY",FACE,{"derivedFrom":subQ1})],"blendedInto":[makeQuery(id+"F3.boolean.opBoolean","COPY",FACE,{"derivedFrom":subQ1})]})});var subQ3=makeQuery(id+"F23.imprint","INTERSECT",VERTEX,{"disambiguationData":[OD(0.0)],"derivedFrom":[subQ2,subQ0]});Q102=makeQuery(id+"F23.imprint","IMPRINT",FACE,{"disambiguationData":[TD([[makeQuery(id+"F23.imprint","IMPRINT",EDGE,{"disambiguationData":[TD([[subQ3,1.0]])],"derivedFrom":subQ0}),1.0]])]});}
            var Q103;
            {var subQ0=sQuery(id+"F23.wireOp",EDGE,"E83.3.0.11");var subQ1=sQuery(id+"F2.wireOp",EDGE,"E44");var subQ2=makeQuery(id+"F21.opBoolean","COPY",EDGE,{"derivedFrom":makeQuery(id+"F8.opFillet","BLEND_EDGE",EDGE,{"disambiguationData":[OD(1.0)],"blendedFrom":[makeQuery(id+"F4.opFillet","BLEND_EDGE",EDGE,{"blendedFrom":[makeQuery(id+"F3.boolean.opBoolean","COPY",EDGE,{"derivedFrom":makeQuery(id+"F3.opExtrude","SWEPT_EDGE",EDGE,{"disambiguationData":[OSD([sQuery(id+"F0.wireOp",EDGE,"E19.MirrorCS"),sQuery(id+"F0.wireOp",EDGE,"E20.MirrorCS"),subQ1,sQuery(id+"F2.wireOp",EDGE,"E45")])]})}),makeQuery(id+"F1.opExtrude","SWEPT_FACE",FACE,{"disambiguationData":[OSD([sQuery(id+"F0.wireOp",EDGE,"E13")])]})],"blendedInto":[makeQuery(id+"F1.opExtrude","SWEPT_FACE",FACE,{"disambiguationData":[OSD([sQuery(id+"F0.wireOp",EDGE,"E13")])]})]}),makeQuery(id+"F3.boolean.opBoolean","COPY",FACE,{"derivedFrom":makeQuery(id+"F3.opExtrude","SWEPT_FACE",FACE,{"disambiguationData":[OSD([subQ1])]})})],"blendedInto":[makeQuery(id+"F3.boolean.opBoolean","COPY",FACE,{"derivedFrom":makeQuery(id+"F3.opExtrude","SWEPT_FACE",FACE,{"disambiguationData":[OSD([subQ1])]})})]})});var subQ3=makeQuery(id+"F23.imprint","INTERSECT",VERTEX,{"disambiguationData":[OD(0.0)],"derivedFrom":[subQ2,subQ0]});Q103=makeQuery(id+"F23.imprint","IMPRINT",FACE,{"disambiguationData":[TD([[makeQuery(id+"F23.imprint","IMPRINT",EDGE,{"disambiguationData":[TD([[subQ3,-1.0]])],"derivedFrom":subQ0}),1.0]])]});}
            var Q104;
            {var subQ0=sQuery(id+"F23.wireOp",EDGE,"E83.4.0.2");var subQ1=makeQuery(id+"F3.opExtrude","SWEPT_FACE",FACE,{"disambiguationData":[OSD([sQuery(id+"F2.wireOp",EDGE,"E44")])]});var subQ2=makeQuery(id+"F21.opBoolean","COPY",EDGE,{"derivedFrom":makeQuery(id+"F8.opFillet","BLEND_EDGE",EDGE,{"blendedFrom":[makeQuery(id+"F3.boolean.opBoolean","INTERSECT",EDGE,{"derivedFrom":[makeQuery(id+"F1.opExtrude","SWEPT_FACE",FACE,{"disambiguationData":[OSD([sQuery(id+"F0.wireOp",EDGE,"E18.MirrorCS")])]}),subQ1]}),makeQuery(id+"F3.boolean.opBoolean","COPY",FACE,{"derivedFrom":subQ1})],"blendedInto":[makeQuery(id+"F3.boolean.opBoolean","COPY",FACE,{"derivedFrom":subQ1})]})});var subQ3=makeQuery(id+"F23.imprint","INTERSECT",VERTEX,{"disambiguationData":[OD(0.0)],"derivedFrom":[subQ2,subQ0]});Q104=makeQuery(id+"F23.imprint","IMPRINT",FACE,{"disambiguationData":[TD([[makeQuery(id+"F23.imprint","IMPRINT",EDGE,{"disambiguationData":[TD([[subQ3,1.0]])],"derivedFrom":subQ0}),1.0]])]});}
            var Q105;
            {var subQ0=sQuery(id+"F23.wireOp",EDGE,"E83.4.0.3");var subQ1=makeQuery(id+"F3.opExtrude","SWEPT_FACE",FACE,{"disambiguationData":[OSD([sQuery(id+"F2.wireOp",EDGE,"E44")])]});var subQ2=makeQuery(id+"F21.opBoolean","COPY",EDGE,{"derivedFrom":makeQuery(id+"F8.opFillet","BLEND_EDGE",EDGE,{"blendedFrom":[makeQuery(id+"F3.boolean.opBoolean","INTERSECT",EDGE,{"derivedFrom":[makeQuery(id+"F1.opExtrude","SWEPT_FACE",FACE,{"disambiguationData":[OSD([sQuery(id+"F0.wireOp",EDGE,"E18.MirrorCS")])]}),subQ1]}),makeQuery(id+"F3.boolean.opBoolean","COPY",FACE,{"derivedFrom":subQ1})],"blendedInto":[makeQuery(id+"F3.boolean.opBoolean","COPY",FACE,{"derivedFrom":subQ1})]})});var subQ3=makeQuery(id+"F23.imprint","INTERSECT",VERTEX,{"disambiguationData":[OD(0.0)],"derivedFrom":[subQ2,subQ0]});Q105=makeQuery(id+"F23.imprint","IMPRINT",FACE,{"disambiguationData":[TD([[makeQuery(id+"F23.imprint","IMPRINT",EDGE,{"disambiguationData":[TD([[subQ3,1.0]])],"derivedFrom":subQ0}),1.0]])]});}
            var Q106;
            {var subQ0=sQuery(id+"F23.wireOp",EDGE,"E83.4.0.4");var subQ1=makeQuery(id+"F3.opExtrude","SWEPT_FACE",FACE,{"disambiguationData":[OSD([sQuery(id+"F2.wireOp",EDGE,"E44")])]});var subQ2=makeQuery(id+"F21.opBoolean","COPY",EDGE,{"derivedFrom":makeQuery(id+"F8.opFillet","BLEND_EDGE",EDGE,{"blendedFrom":[makeQuery(id+"F3.boolean.opBoolean","INTERSECT",EDGE,{"derivedFrom":[makeQuery(id+"F1.opExtrude","SWEPT_FACE",FACE,{"disambiguationData":[OSD([sQuery(id+"F0.wireOp",EDGE,"E18.MirrorCS")])]}),subQ1]}),makeQuery(id+"F3.boolean.opBoolean","COPY",FACE,{"derivedFrom":subQ1})],"blendedInto":[makeQuery(id+"F3.boolean.opBoolean","COPY",FACE,{"derivedFrom":subQ1})]})});var subQ3=makeQuery(id+"F23.imprint","INTERSECT",VERTEX,{"disambiguationData":[OD(0.0)],"derivedFrom":[subQ2,subQ0]});Q106=makeQuery(id+"F23.imprint","IMPRINT",FACE,{"disambiguationData":[TD([[makeQuery(id+"F23.imprint","IMPRINT",EDGE,{"disambiguationData":[TD([[subQ3,1.0]])],"derivedFrom":subQ0}),1.0]])]});}
            var Q107;
            {var subQ0=sQuery(id+"F23.wireOp",EDGE,"E83.4.0.5");var subQ1=makeQuery(id+"F3.opExtrude","SWEPT_FACE",FACE,{"disambiguationData":[OSD([sQuery(id+"F2.wireOp",EDGE,"E44")])]});var subQ2=makeQuery(id+"F21.opBoolean","COPY",EDGE,{"derivedFrom":makeQuery(id+"F8.opFillet","BLEND_EDGE",EDGE,{"blendedFrom":[makeQuery(id+"F3.boolean.opBoolean","INTERSECT",EDGE,{"derivedFrom":[makeQuery(id+"F1.opExtrude","SWEPT_FACE",FACE,{"disambiguationData":[OSD([sQuery(id+"F0.wireOp",EDGE,"E18.MirrorCS")])]}),subQ1]}),makeQuery(id+"F3.boolean.opBoolean","COPY",FACE,{"derivedFrom":subQ1})],"blendedInto":[makeQuery(id+"F3.boolean.opBoolean","COPY",FACE,{"derivedFrom":subQ1})]})});var subQ3=makeQuery(id+"F23.imprint","INTERSECT",VERTEX,{"disambiguationData":[OD(0.0)],"derivedFrom":[subQ2,subQ0]});Q107=makeQuery(id+"F23.imprint","IMPRINT",FACE,{"disambiguationData":[TD([[makeQuery(id+"F23.imprint","IMPRINT",EDGE,{"disambiguationData":[TD([[subQ3,-1.0]])],"derivedFrom":subQ0}),1.0]])]});}
            var Q108;
            {var subQ0=sQuery(id+"F23.wireOp",EDGE,"E83.4.0.11");var subQ1=sQuery(id+"F2.wireOp",EDGE,"E44");var subQ2=sQuery(id+"F0.wireOp",EDGE,"E20.MirrorCS");var subQ3=makeQuery(id+"F21.opBoolean","COPY",EDGE,{"derivedFrom":makeQuery(id+"F8.opFillet","BLEND_EDGE",EDGE,{"disambiguationData":[OD(0.0)],"blendedFrom":[makeQuery(id+"F4.opFillet","BLEND_EDGE",EDGE,{"blendedFrom":[makeQuery(id+"F3.boolean.opBoolean","COPY",EDGE,{"derivedFrom":makeQuery(id+"F3.opExtrude","SWEPT_EDGE",EDGE,{"disambiguationData":[OSD([sQuery(id+"F0.wireOp",EDGE,"E19.MirrorCS"),subQ2,subQ1,sQuery(id+"F2.wireOp",EDGE,"E45")])]})}),makeQuery(id+"F1.opExtrude","SWEPT_FACE",FACE,{"disambiguationData":[OSD([subQ2])]})],"blendedInto":[makeQuery(id+"F1.opExtrude","SWEPT_FACE",FACE,{"disambiguationData":[OSD([subQ2])]})]}),makeQuery(id+"F3.boolean.opBoolean","COPY",FACE,{"derivedFrom":makeQuery(id+"F3.opExtrude","SWEPT_FACE",FACE,{"disambiguationData":[OSD([subQ1])]})})],"blendedInto":[makeQuery(id+"F3.boolean.opBoolean","COPY",FACE,{"derivedFrom":makeQuery(id+"F3.opExtrude","SWEPT_FACE",FACE,{"disambiguationData":[OSD([subQ1])]})})]})});var subQ4=makeQuery(id+"F23.imprint","INTERSECT",VERTEX,{"disambiguationData":[OD(0.0)],"derivedFrom":[subQ3,subQ0]});Q108=makeQuery(id+"F23.imprint","IMPRINT",FACE,{"disambiguationData":[TD([[makeQuery(id+"F23.imprint","IMPRINT",EDGE,{"disambiguationData":[TD([[subQ4,1.0]])],"derivedFrom":subQ0}),1.0]])]});}
            var Q109;
            {var subQ0=sQuery(id+"F23.wireOp",EDGE,"E100.5.0.0");var subQ1=makeQuery(id+"F3.opExtrude","SWEPT_FACE",FACE,{"disambiguationData":[OSD([sQuery(id+"F2.wireOp",EDGE,"E44")])]});var subQ2=makeQuery(id+"F21.opBoolean","COPY",EDGE,{"derivedFrom":makeQuery(id+"F8.opFillet","BLEND_EDGE",EDGE,{"blendedFrom":[makeQuery(id+"F3.boolean.opBoolean","INTERSECT",EDGE,{"derivedFrom":[makeQuery(id+"F1.opExtrude","SWEPT_FACE",FACE,{"disambiguationData":[OSD([sQuery(id+"F0.wireOp",EDGE,"E15")])]}),subQ1]}),makeQuery(id+"F3.boolean.opBoolean","COPY",FACE,{"derivedFrom":subQ1})],"blendedInto":[makeQuery(id+"F3.boolean.opBoolean","COPY",FACE,{"derivedFrom":subQ1})]})});var subQ3=makeQuery(id+"F23.imprint","INTERSECT",VERTEX,{"disambiguationData":[OD(0.0)],"derivedFrom":[subQ2,subQ0]});Q109=makeQuery(id+"F23.imprint","IMPRINT",FACE,{"disambiguationData":[TD([[makeQuery(id+"F23.imprint","IMPRINT",EDGE,{"disambiguationData":[TD([[subQ3,1.0]])],"derivedFrom":subQ0}),1.0]])]});}
            var Q110;
            {var subQ0=sQuery(id+"F23.wireOp",EDGE,"E100.6.0.0");var subQ1=makeQuery(id+"F3.opExtrude","SWEPT_FACE",FACE,{"disambiguationData":[OSD([sQuery(id+"F2.wireOp",EDGE,"E44")])]});var subQ2=makeQuery(id+"F21.opBoolean","COPY",EDGE,{"derivedFrom":makeQuery(id+"F8.opFillet","BLEND_EDGE",EDGE,{"blendedFrom":[makeQuery(id+"F3.boolean.opBoolean","INTERSECT",EDGE,{"derivedFrom":[makeQuery(id+"F1.opExtrude","SWEPT_FACE",FACE,{"disambiguationData":[OSD([sQuery(id+"F0.wireOp",EDGE,"E15")])]}),subQ1]}),makeQuery(id+"F3.boolean.opBoolean","COPY",FACE,{"derivedFrom":subQ1})],"blendedInto":[makeQuery(id+"F3.boolean.opBoolean","COPY",FACE,{"derivedFrom":subQ1})]})});var subQ3=makeQuery(id+"F23.imprint","INTERSECT",VERTEX,{"disambiguationData":[OD(0.0)],"derivedFrom":[subQ2,subQ0]});Q110=makeQuery(id+"F23.imprint","IMPRINT",FACE,{"disambiguationData":[TD([[makeQuery(id+"F23.imprint","IMPRINT",EDGE,{"disambiguationData":[TD([[subQ3,1.0]])],"derivedFrom":subQ0}),1.0]])]});}
            var Q111;
            {var subQ0=sQuery(id+"F23.wireOp",EDGE,"E100.7.0.0");var subQ1=makeQuery(id+"F3.opExtrude","SWEPT_FACE",FACE,{"disambiguationData":[OSD([sQuery(id+"F2.wireOp",EDGE,"E44")])]});var subQ2=makeQuery(id+"F21.opBoolean","COPY",EDGE,{"derivedFrom":makeQuery(id+"F8.opFillet","BLEND_EDGE",EDGE,{"blendedFrom":[makeQuery(id+"F3.boolean.opBoolean","INTERSECT",EDGE,{"derivedFrom":[makeQuery(id+"F1.opExtrude","SWEPT_FACE",FACE,{"disambiguationData":[OSD([sQuery(id+"F0.wireOp",EDGE,"E15")])]}),subQ1]}),makeQuery(id+"F3.boolean.opBoolean","COPY",FACE,{"derivedFrom":subQ1})],"blendedInto":[makeQuery(id+"F3.boolean.opBoolean","COPY",FACE,{"derivedFrom":subQ1})]})});var subQ3=makeQuery(id+"F23.imprint","INTERSECT",VERTEX,{"disambiguationData":[OD(0.0)],"derivedFrom":[subQ2,subQ0]});Q111=makeQuery(id+"F23.imprint","IMPRINT",FACE,{"disambiguationData":[TD([[makeQuery(id+"F23.imprint","IMPRINT",EDGE,{"disambiguationData":[TD([[subQ3,1.0]])],"derivedFrom":subQ0}),1.0]])]});}
            var Q112;
            {var subQ0=sQuery(id+"F23.wireOp",EDGE,"E100.8.0.0");var subQ1=makeQuery(id+"F3.boolean.opBoolean","COPY",FACE,{"derivedFrom":makeQuery(id+"F3.opExtrude","SWEPT_FACE",FACE,{"disambiguationData":[OSD([sQuery(id+"F2.wireOp",EDGE,"E44")])]})});var subQ2=makeQuery(id+"F21.opBoolean","COPY",EDGE,{"derivedFrom":makeQuery(id+"F8.opFillet","BLEND_EDGE",EDGE,{"disambiguationData":[OD(1.0)],"blendedFrom":[makeQuery(id+"F7.opFillet","BLEND_EDGE",EDGE,{"blendedFrom":[makeQuery(id+"F1.opExtrude","SWEPT_EDGE",EDGE,{"disambiguationData":[OSD([sQuery(id+"F0.wireOp",EDGE,"E14"),sQuery(id+"F0.wireOp",EDGE,"E15")])]}),subQ1],"blendedInto":[subQ1]}),subQ1],"blendedInto":[subQ1]})});var subQ3=makeQuery(id+"F23.imprint","INTERSECT",VERTEX,{"disambiguationData":[OD(0.0)],"derivedFrom":[subQ2,subQ0]});Q112=makeQuery(id+"F23.imprint","IMPRINT",FACE,{"disambiguationData":[TD([[makeQuery(id+"F23.imprint","IMPRINT",EDGE,{"disambiguationData":[TD([[subQ3,-1.0]])],"derivedFrom":subQ0}),1.0]])]});}
            var Q113;
            {var subQ0=sQuery(id+"F23.wireOp",EDGE,"E101.2.0.5");var subQ1=makeQuery(id+"F3.opExtrude","SWEPT_FACE",FACE,{"disambiguationData":[OSD([sQuery(id+"F2.wireOp",EDGE,"E44")])]});var subQ2=makeQuery(id+"F21.opBoolean","COPY",EDGE,{"derivedFrom":makeQuery(id+"F8.opFillet","BLEND_EDGE",EDGE,{"blendedFrom":[makeQuery(id+"F3.boolean.opBoolean","INTERSECT",EDGE,{"derivedFrom":[makeQuery(id+"F1.opExtrude","SWEPT_FACE",FACE,{"disambiguationData":[OSD([sQuery(id+"F0.wireOp",EDGE,"E18.MirrorCS")])]}),subQ1]}),makeQuery(id+"F3.boolean.opBoolean","COPY",FACE,{"derivedFrom":subQ1})],"blendedInto":[makeQuery(id+"F3.boolean.opBoolean","COPY",FACE,{"derivedFrom":subQ1})]})});var subQ3=makeQuery(id+"F23.imprint","INTERSECT",VERTEX,{"disambiguationData":[OD(0.0)],"derivedFrom":[subQ2,subQ0]});Q113=makeQuery(id+"F23.imprint","IMPRINT",FACE,{"disambiguationData":[TD([[makeQuery(id+"F23.imprint","IMPRINT",EDGE,{"disambiguationData":[TD([[subQ3,-1.0]])],"derivedFrom":subQ0}),1.0]])]});}
            var Q114;
            {var subQ0=sQuery(id+"F23.wireOp",EDGE,"E101.2.0.6");var subQ1=makeQuery(id+"F3.opExtrude","SWEPT_FACE",FACE,{"disambiguationData":[OSD([sQuery(id+"F2.wireOp",EDGE,"E44")])]});var subQ2=makeQuery(id+"F21.opBoolean","COPY",EDGE,{"derivedFrom":makeQuery(id+"F8.opFillet","BLEND_EDGE",EDGE,{"blendedFrom":[makeQuery(id+"F3.boolean.opBoolean","INTERSECT",EDGE,{"derivedFrom":[makeQuery(id+"F1.opExtrude","SWEPT_FACE",FACE,{"disambiguationData":[OSD([sQuery(id+"F0.wireOp",EDGE,"E18.MirrorCS")])]}),subQ1]}),makeQuery(id+"F3.boolean.opBoolean","COPY",FACE,{"derivedFrom":subQ1})],"blendedInto":[makeQuery(id+"F3.boolean.opBoolean","COPY",FACE,{"derivedFrom":subQ1})]})});var subQ3=makeQuery(id+"F23.imprint","INTERSECT",VERTEX,{"disambiguationData":[OD(0.0)],"derivedFrom":[subQ2,subQ0]});Q114=makeQuery(id+"F23.imprint","IMPRINT",FACE,{"disambiguationData":[TD([[makeQuery(id+"F23.imprint","IMPRINT",EDGE,{"disambiguationData":[TD([[subQ3,-1.0]])],"derivedFrom":subQ0}),1.0]])]});}
            var Q115;
            {var subQ0=sQuery(id+"F23.wireOp",EDGE,"E101.2.0.7");var subQ1=makeQuery(id+"F3.opExtrude","SWEPT_FACE",FACE,{"disambiguationData":[OSD([sQuery(id+"F2.wireOp",EDGE,"E44")])]});var subQ2=makeQuery(id+"F21.opBoolean","COPY",EDGE,{"derivedFrom":makeQuery(id+"F8.opFillet","BLEND_EDGE",EDGE,{"blendedFrom":[makeQuery(id+"F3.boolean.opBoolean","INTERSECT",EDGE,{"derivedFrom":[makeQuery(id+"F1.opExtrude","SWEPT_FACE",FACE,{"disambiguationData":[OSD([sQuery(id+"F0.wireOp",EDGE,"E18.MirrorCS")])]}),subQ1]}),makeQuery(id+"F3.boolean.opBoolean","COPY",FACE,{"derivedFrom":subQ1})],"blendedInto":[makeQuery(id+"F3.boolean.opBoolean","COPY",FACE,{"derivedFrom":subQ1})]})});var subQ3=makeQuery(id+"F23.imprint","INTERSECT",VERTEX,{"disambiguationData":[OD(0.0)],"derivedFrom":[subQ2,subQ0]});Q115=makeQuery(id+"F23.imprint","IMPRINT",FACE,{"disambiguationData":[TD([[makeQuery(id+"F23.imprint","IMPRINT",EDGE,{"disambiguationData":[TD([[subQ3,-1.0]])],"derivedFrom":subQ0}),1.0]])]});}
            var Q116;
            {var subQ0=sQuery(id+"F23.wireOp",EDGE,"E101.2.0.8");var subQ1=makeQuery(id+"F3.boolean.opBoolean","COPY",FACE,{"derivedFrom":makeQuery(id+"F3.opExtrude","SWEPT_FACE",FACE,{"disambiguationData":[OSD([sQuery(id+"F2.wireOp",EDGE,"E44")])]})});var subQ2=makeQuery(id+"F21.opBoolean","COPY",EDGE,{"derivedFrom":makeQuery(id+"F8.opFillet","BLEND_EDGE",EDGE,{"disambiguationData":[OD(0.0)],"blendedFrom":[makeQuery(id+"F7.opFillet","BLEND_EDGE",EDGE,{"blendedFrom":[makeQuery(id+"F1.opExtrude","SWEPT_EDGE",EDGE,{"disambiguationData":[OSD([sQuery(id+"F0.wireOp",EDGE,"E18.MirrorCS"),sQuery(id+"F0.wireOp",EDGE,"E19.MirrorCS")])]}),subQ1],"blendedInto":[subQ1]}),subQ1],"blendedInto":[subQ1]})});var subQ3=makeQuery(id+"F23.imprint","INTERSECT",VERTEX,{"disambiguationData":[OD(0.0)],"derivedFrom":[subQ2,subQ0]});Q116=makeQuery(id+"F23.imprint","IMPRINT",FACE,{"disambiguationData":[TD([[makeQuery(id+"F23.imprint","IMPRINT",EDGE,{"disambiguationData":[TD([[subQ3,1.0]])],"derivedFrom":subQ0}),1.0]])]});}
            var Q117;
            {var subQ1=sQuery(id+"F2.wireOp",EDGE,"E44");var subQ2=makeQuery(id+"F3.boolean.opBoolean","COPY",FACE,{"derivedFrom":makeQuery(id+"F3.opExtrude","SWEPT_FACE",FACE,{"disambiguationData":[OSD([subQ1])]})});var subQ9=makeQuery(id+"F21.opBoolean","INTERSECT",EDGE,{"derivedFrom":[subQ2,makeQuery(id+"F20.opExtrude","SWEPT_FACE",FACE,{"disambiguationData":[OSD([sQuery(id+"F19.wireOp",EDGE,"E78")])]})]});Q117=makeQuery(id+"F23.imprint","IMPRINT",FACE,{"disambiguationData":[TD([[makeQuery(id+"F23.imprint","IMPRINT",EDGE,{"derivedFrom":subQ9}),1.0]])]});}
            var Q118;
            {var subQ1=sQuery(id+"F2.wireOp",EDGE,"E44");var subQ2=makeQuery(id+"F3.boolean.opBoolean","COPY",FACE,{"derivedFrom":makeQuery(id+"F3.opExtrude","SWEPT_FACE",FACE,{"disambiguationData":[OSD([subQ1])]})});var subQ9=makeQuery(id+"F21.opBoolean","INTERSECT",EDGE,{"derivedFrom":[subQ2,makeQuery(id+"F20.opExtrude","SWEPT_FACE",FACE,{"disambiguationData":[OSD([sQuery(id+"F19.wireOp",EDGE,"E78")])]})]});Q118=makeQuery(id+"F23.imprint","IMPRINT",FACE,{"disambiguationData":[TD([[makeQuery(id+"F23.imprint","IMPRINT",EDGE,{"derivedFrom":subQ9}),-1.0]])]});}
            var Q119;
            {var subQ0=sQuery(id+"F23.wireOp",EDGE,"E105");var subQ1=makeQuery(id+"F3.opExtrude","SWEPT_FACE",FACE,{"disambiguationData":[OSD([sQuery(id+"F2.wireOp",EDGE,"E44")])]});var subQ2=makeQuery(id+"F3.boolean.opBoolean","COPY",FACE,{"derivedFrom":subQ1});var subQ3=makeQuery(id+"F21.opBoolean","COPY",EDGE,{"derivedFrom":makeQuery(id+"F8.opFillet","BLEND_EDGE",EDGE,{"blendedFrom":[makeQuery(id+"F3.boolean.opBoolean","INTERSECT",EDGE,{"derivedFrom":[makeQuery(id+"F1.opExtrude","SWEPT_FACE",FACE,{"disambiguationData":[OSD([sQuery(id+"F0.wireOp",EDGE,"E15")])]}),subQ1]}),subQ2],"blendedInto":[subQ2]})});var subQ4=makeQuery(id+"F23.imprint","INTERSECT",VERTEX,{"disambiguationData":[OD(0.0)],"derivedFrom":[subQ3,subQ0]});Q119=makeQuery(id+"F23.imprint","IMPRINT",FACE,{"disambiguationData":[TD([[makeQuery(id+"F23.imprint","IMPRINT",EDGE,{"disambiguationData":[TD([[subQ4,-1.0]])],"derivedFrom":subQ0}),1.0]])]});}
            var Q120;
            Q120=makeQuery(id+"F23.imprint","IMPRINT",FACE,{"disambiguationData":[TD([[makeQuery(id+"F23.imprint","IMPRINT",EDGE,{"derivedFrom":sQuery(id+"F23.wireOp",EDGE,"E100.10.0.0")}),1.0]])]});
            extrude(context, id + "F24", {"entities" : qUnion([Q0, Q1, Q2, Q3, Q4, Q5, Q6, Q7, Q8, Q9, Q10, Q11, Q12, Q13, Q14, Q15, Q16, Q17, Q18, Q19, Q20, Q21, Q22, Q23, Q24, Q25, Q26, Q27, Q28, Q29, Q30, Q31, Q32, Q33, Q34, Q35, Q36, Q37, Q38, Q39, Q40, Q41, Q42, Q43, Q44, Q45, Q46, Q47, Q48, Q49, Q50, Q51, Q52, Q53, Q54, Q55, Q56, Q57, Q58, Q59, Q60, Q61, Q62, Q63, Q64, Q65, Q66, Q67, Q68, Q69, Q70, Q71, Q72, Q73, Q74, Q75, Q76, Q77, Q78, Q79, Q80, Q81, Q82, Q83, Q84, Q85, Q86, Q87, Q88, Q89, Q90, Q91, Q92, Q93, Q94, Q95, Q96, Q97, Q98, Q99, Q100, Q101, Q102, Q103, Q104, Q105, Q106, Q107, Q108, Q109, Q110, Q111, Q112, Q113, Q114, Q115, Q116, Q117, Q118, Q119, Q120]), "operationType" : NewBodyOperationType.ADD, "oppositeDirection" : true, "depth" : 2 * mm});
        }
        {
            var Q0;
            Q0=qSketchRegion(id+"F23",true);
            extrude(context, id + "F25", {"entities" : qUnion([Q0]), "operationType" : NewBodyOperationType.ADD, "depth" : 10 * mm});
        }
        {
            var Q0;
            Q0=makeQuery(id+"F1.opExtrude","SWEPT_FACE",FACE,{"disambiguationData":[OSD([sQuery(id+"F0.wireOp",EDGE,"E21.MirrorCS")])]});
            var sketch = newSketch(context, id + "F26", { "sketchPlane" : qUnion([Q0])});
            skLineSegment(sketch, "E111", {"start": v(-218.82, 19.3) * mm, "end": v(-210.27, 15.92) * mm});
            skLineSegment(sketch, "E112", {"start": v(-210.27, 15.92) * mm, "end": v(-200.88, 18.87) * mm});
            skLineSegment(sketch, "E113", {"start": v(-200.88, 18.87) * mm, "end": v(-193.28, 16) * mm});
            skLineSegment(sketch, "E114", {"start": v(-193.28, 16) * mm, "end": v(-184.53, 19.67) * mm});
            skLineSegment(sketch, "E115", {"start": v(-184.53, 19.67) * mm, "end": v(-218.82, 19.3) * mm});
            skSolve(sketch);
        }
        {
            var Q0;
            Q0=makeQuery(id+"F26.imprint","IMPRINT",FACE,{"disambiguationData":[TD([[makeQuery(id+"F26.imprint","IMPRINT",EDGE,{"derivedFrom":sQuery(id+"F26.wireOp",EDGE,"E111")}),1.0]])]});
            extrude(context, id + "F27", {"entities" : qUnion([Q0]), "operationType" : NewBodyOperationType.REMOVE, "endBound" : BoundingType.SYMMETRIC, "oppositeDirection" : true, "depth" : 40 * mm});
        }
        {
            var Q0;
            Q0=makeQuery(id+"F20.opExtrude","SWEPT_BODY",BODY,{"disambiguationData":[OSD([sQuery(id+"F19.wireOp",EDGE,"E78"),sQuery(id+"F19.wireOp",EDGE,"E79"),sQuery(id+"F19.wireOp",EDGE,"E80"),sQuery(id+"F19.wireOp",EDGE,"E81")])]});
            deleteBodies(context, id + "F28", {"entities" : qUnion([Q0])});
        }
        {
            var Q0;
            Q0=makeQuery(id+"F14.opExtrude","SWEPT_BODY",BODY,{"disambiguationData":[OSD([sQuery(id+"F13.wireOp",EDGE,"E50"),sQuery(id+"F13.wireOp",EDGE,"E51"),sQuery(id+"F13.wireOp",EDGE,"E52"),sQuery(id+"F13.wireOp",EDGE,"E53"),sQuery(id+"F13.wireOp",EDGE,"E54"),sQuery(id+"F13.wireOp",EDGE,"E55"),sQuery(id+"F13.wireOp",EDGE,"E56"),sQuery(id+"F13.wireOp",EDGE,"E57"),sQuery(id+"F13.wireOp",EDGE,"E58.filletArc"),sQuery(id+"F13.wireOp",EDGE,"E59.filletArc"),sQuery(id+"F13.wireOp",EDGE,"E60.filletArc"),sQuery(id+"F13.wireOp",EDGE,"E61.filletArc"),sQuery(id+"F13.wireOp",EDGE,"E62.filletArc"),sQuery(id+"F13.wireOp",EDGE,"E63")])]});
            deleteBodies(context, id + "F29", {"entities" : qUnion([Q0])});
        }
        {
            var Q0;
            Q0=makeQuery(id+"F1.opExtrude","SWEPT_BODY",BODY,{"disambiguationData":[OSD([sQuery(id+"F0.wireOp",EDGE,"E1"),sQuery(id+"F0.wireOp",EDGE,"E8"),sQuery(id+"F0.wireOp",EDGE,"E9"),sQuery(id+"F0.wireOp",EDGE,"E10"),sQuery(id+"F0.wireOp",EDGE,"E11"),sQuery(id+"F0.wireOp",EDGE,"E12"),sQuery(id+"F0.wireOp",EDGE,"E13"),sQuery(id+"F0.wireOp",EDGE,"E14"),sQuery(id+"F0.wireOp",EDGE,"E15"),sQuery(id+"F0.wireOp",EDGE,"E16.MirrorCS"),sQuery(id+"F0.wireOp",EDGE,"E17.MirrorCS"),sQuery(id+"F0.wireOp",EDGE,"E18.MirrorCS"),sQuery(id+"F0.wireOp",EDGE,"E19.MirrorCS"),sQuery(id+"F0.wireOp",EDGE,"E20.MirrorCS"),sQuery(id+"F0.wireOp",EDGE,"E21.MirrorCS"),sQuery(id+"F0.wireOp",EDGE,"E22.MirrorCS"),sQuery(id+"F0.wireOp",EDGE,"E23.MirrorCS"),sQuery(id+"F0.wireOp",EDGE,"E24.MirrorCS")])]});
            var Q1;
            Q1=makeQuery(id+"F15.opBoolean","INTERSECT",BODY,{"derivedFrom":[makeQuery(id+"F1.opExtrude","SWEPT_BODY",BODY,{"disambiguationData":[OSD([sQuery(id+"F0.wireOp",EDGE,"E1"),sQuery(id+"F0.wireOp",EDGE,"E8"),sQuery(id+"F0.wireOp",EDGE,"E9"),sQuery(id+"F0.wireOp",EDGE,"E10"),sQuery(id+"F0.wireOp",EDGE,"E11"),sQuery(id+"F0.wireOp",EDGE,"E12"),sQuery(id+"F0.wireOp",EDGE,"E13"),sQuery(id+"F0.wireOp",EDGE,"E14"),sQuery(id+"F0.wireOp",EDGE,"E15"),sQuery(id+"F0.wireOp",EDGE,"E16.MirrorCS"),sQuery(id+"F0.wireOp",EDGE,"E17.MirrorCS"),sQuery(id+"F0.wireOp",EDGE,"E18.MirrorCS"),sQuery(id+"F0.wireOp",EDGE,"E19.MirrorCS"),sQuery(id+"F0.wireOp",EDGE,"E20.MirrorCS"),sQuery(id+"F0.wireOp",EDGE,"E21.MirrorCS"),sQuery(id+"F0.wireOp",EDGE,"E22.MirrorCS"),sQuery(id+"F0.wireOp",EDGE,"E23.MirrorCS"),sQuery(id+"F0.wireOp",EDGE,"E24.MirrorCS")])]}),makeQuery(id+"F14.opExtrude","SWEPT_BODY",BODY,{"disambiguationData":[OSD([sQuery(id+"F13.wireOp",EDGE,"E50"),sQuery(id+"F13.wireOp",EDGE,"E51"),sQuery(id+"F13.wireOp",EDGE,"E52"),sQuery(id+"F13.wireOp",EDGE,"E53"),sQuery(id+"F13.wireOp",EDGE,"E54"),sQuery(id+"F13.wireOp",EDGE,"E55"),sQuery(id+"F13.wireOp",EDGE,"E56"),sQuery(id+"F13.wireOp",EDGE,"E57"),sQuery(id+"F13.wireOp",EDGE,"E58.filletArc"),sQuery(id+"F13.wireOp",EDGE,"E59.filletArc"),sQuery(id+"F13.wireOp",EDGE,"E60.filletArc"),sQuery(id+"F13.wireOp",EDGE,"E61.filletArc"),sQuery(id+"F13.wireOp",EDGE,"E62.filletArc"),sQuery(id+"F13.wireOp",EDGE,"E63")])]})]});
            var Q2;
            Q2=makeQuery(id+"F21.opBoolean","INTERSECT",BODY,{"derivedFrom":[makeQuery(id+"F1.opExtrude","SWEPT_BODY",BODY,{"disambiguationData":[OSD([sQuery(id+"F0.wireOp",EDGE,"E1"),sQuery(id+"F0.wireOp",EDGE,"E8"),sQuery(id+"F0.wireOp",EDGE,"E9"),sQuery(id+"F0.wireOp",EDGE,"E10"),sQuery(id+"F0.wireOp",EDGE,"E11"),sQuery(id+"F0.wireOp",EDGE,"E12"),sQuery(id+"F0.wireOp",EDGE,"E13"),sQuery(id+"F0.wireOp",EDGE,"E14"),sQuery(id+"F0.wireOp",EDGE,"E15"),sQuery(id+"F0.wireOp",EDGE,"E16.MirrorCS"),sQuery(id+"F0.wireOp",EDGE,"E17.MirrorCS"),sQuery(id+"F0.wireOp",EDGE,"E18.MirrorCS"),sQuery(id+"F0.wireOp",EDGE,"E19.MirrorCS"),sQuery(id+"F0.wireOp",EDGE,"E20.MirrorCS"),sQuery(id+"F0.wireOp",EDGE,"E21.MirrorCS"),sQuery(id+"F0.wireOp",EDGE,"E22.MirrorCS"),sQuery(id+"F0.wireOp",EDGE,"E23.MirrorCS"),sQuery(id+"F0.wireOp",EDGE,"E24.MirrorCS")])]}),makeQuery(id+"F20.opExtrude","SWEPT_BODY",BODY,{"disambiguationData":[OSD([sQuery(id+"F19.wireOp",EDGE,"E78"),sQuery(id+"F19.wireOp",EDGE,"E79"),sQuery(id+"F19.wireOp",EDGE,"E80"),sQuery(id+"F19.wireOp",EDGE,"E81")])]})]});
            var Q3;
            {var subQ0=sQuery(id+"F0.wireOp",EDGE,"E20.MirrorCS");var subQ1=makeQuery(id+"F1.opExtrude","SWEPT_FACE",FACE,{"disambiguationData":[OSD([subQ0])]});var subQ2=sQuery(id+"F0.wireOp",EDGE,"E21.MirrorCS");var subQ3=sQuery(id+"F2.wireOp",EDGE,"E46");var subQ4=sQuery(id+"F2.wireOp",EDGE,"E45");Q3=makeQuery(id+"F8.opFillet","BLEND_VERTEX",VERTEX,{"blendedFrom":[makeQuery(id+"F4.opFillet","BLEND_EDGE",EDGE,{"blendedFrom":[makeQuery(id+"F3.boolean.opBoolean","COPY",EDGE,{"derivedFrom":makeQuery(id+"F3.opExtrude","SWEPT_EDGE",EDGE,{"disambiguationData":[OSD([subQ0,subQ2,subQ4,subQ3])]})}),subQ1],"blendedInto":[subQ1]}),makeQuery(id+"F6.opFillet","BLEND_EDGE",EDGE,{"blendedFrom":[makeQuery(id+"F1.opExtrude","SWEPT_EDGE",EDGE,{"disambiguationData":[OSD([subQ0,subQ2])]}),makeQuery(id+"F4.opFillet","BLEND_FACE",FACE,{"disambiguationData":[OSD([subQ0,subQ2,subQ4,subQ3])]})],"blendedInto":[makeQuery(id+"F4.opFillet","BLEND_FACE",FACE,{"disambiguationData":[OSD([subQ0,subQ2,subQ4,subQ3])]})]}),makeQuery(id+"F6.opFillet","BLEND_FACE",FACE,{"disambiguationData":[OSD([subQ0,subQ2])]}),subQ1],"blendedInto":[makeQuery(id+"F6.opFillet","BLEND_FACE",FACE,{"disambiguationData":[OSD([subQ0,subQ2])]}),subQ1]});}
            transform(context, id + "F30", {"entities" : qUnion([Q0, Q1, Q2]), "transformType" : TransformType.SCALE_UNIFORMLY, "scale" : .8, "scalePoint" : qUnion([Q3]), "makeCopy" : false});
        }
    });
